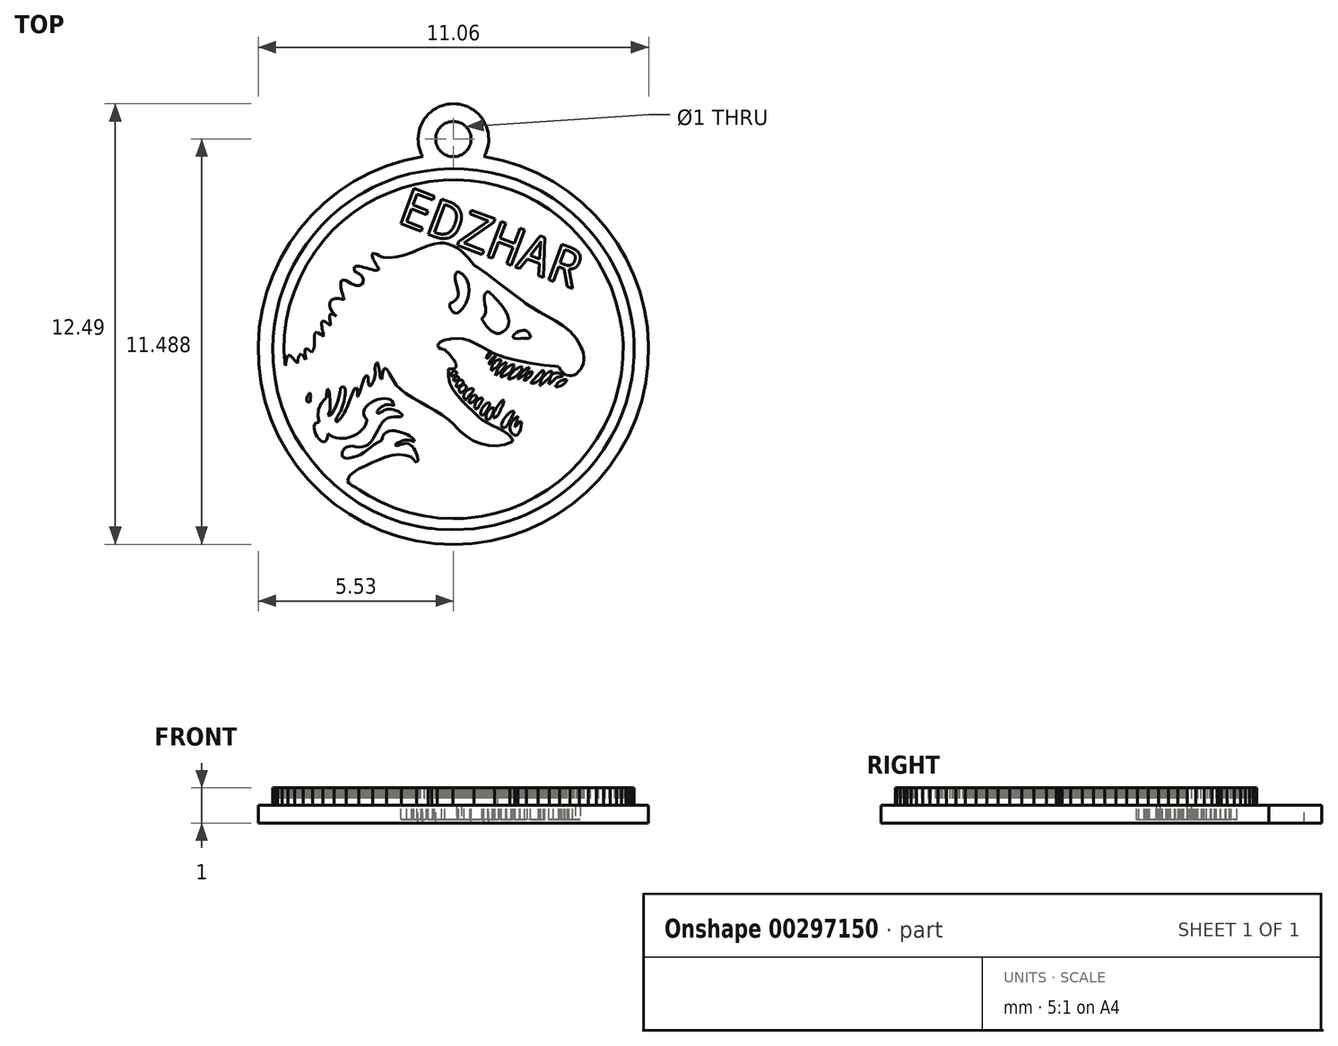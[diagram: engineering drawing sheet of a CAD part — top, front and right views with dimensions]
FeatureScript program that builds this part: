
annotation { "Feature Type Name" : "Feature", "Feature Type Description" : "" }
export const myFeature = defineFeature(function(context is Context, id is Id, definition is map)
    precondition{}
    {
        {
            var Q0;
            Q0=qCreatedBy(makeId("Top.planeOp"),FACE);
            var sketch = newSketch(context, id + "F0", { "sketchPlane" : qUnion([Q0])});
            skLineSegment(sketch, "E0", {"start": v(-0.6, -5.08) * mm, "end": v(-0.71, -5.07) * mm});
            skLineSegment(sketch, "E1", {"start": v(-0.71, -5.07) * mm, "end": v(-1.04, -5.02) * mm});
            skLineSegment(sketch, "E2", {"start": v(-1.04, -5.02) * mm, "end": v(-1.47, -4.9) * mm});
            skLineSegment(sketch, "E3", {"start": v(-1.47, -4.9) * mm, "end": v(-1.9, -4.76) * mm});
            skLineSegment(sketch, "E4", {"start": v(-1.9, -4.76) * mm, "end": v(-2.3, -4.58) * mm});
            skLineSegment(sketch, "E5", {"start": v(-2.3, -4.58) * mm, "end": v(-2.68, -4.36) * mm});
            skLineSegment(sketch, "E6", {"start": v(-2.68, -4.36) * mm, "end": v(-3.04, -4.11) * mm});
            skLineSegment(sketch, "E7", {"start": v(-3.04, -4.11) * mm, "end": v(-3.38, -3.83) * mm});
            skLineSegment(sketch, "E8", {"start": v(-3.38, -3.83) * mm, "end": v(-3.7, -3.52) * mm});
            skLineSegment(sketch, "E9", {"start": v(-3.7, -3.52) * mm, "end": v(-4, -3.2) * mm});
            skLineSegment(sketch, "E10", {"start": v(-4, -3.2) * mm, "end": v(-4.26, -2.84) * mm});
            skLineSegment(sketch, "E11", {"start": v(-4.26, -2.84) * mm, "end": v(-4.49, -2.46) * mm});
            skLineSegment(sketch, "E12", {"start": v(-4.49, -2.46) * mm, "end": v(-4.69, -2.06) * mm});
            skLineSegment(sketch, "E13", {"start": v(-4.69, -2.06) * mm, "end": v(-4.85, -1.65) * mm});
            skLineSegment(sketch, "E14", {"start": v(-4.85, -1.65) * mm, "end": v(-4.98, -1.23) * mm});
            skLineSegment(sketch, "E15", {"start": v(-4.98, -1.23) * mm, "end": v(-5.06, -0.8) * mm});
            skLineSegment(sketch, "E16", {"start": v(-5.06, -0.8) * mm, "end": v(-5.1, -0.46) * mm});
            skLineSegment(sketch, "E17", {"start": v(-5.1, -0.46) * mm, "end": v(-5.1, -0.35) * mm});
            skLineSegment(sketch, "E18", {"start": v(-5.1, -0.35) * mm, "end": v(-5.11, -0.26) * mm});
            skLineSegment(sketch, "E19", {"start": v(-5.11, -0.26) * mm, "end": v(-5.12, 0) * mm});
            skLineSegment(sketch, "E20", {"start": v(-5.12, 0) * mm, "end": v(-5.1, 0.36) * mm});
            skLineSegment(sketch, "E21", {"start": v(-5.1, 0.36) * mm, "end": v(-5.07, 0.7) * mm});
            skLineSegment(sketch, "E22", {"start": v(-5.07, 0.7) * mm, "end": v(-5, 1.05) * mm});
            skLineSegment(sketch, "E23", {"start": v(-5, 1.05) * mm, "end": v(-4.92, 1.4) * mm});
            skLineSegment(sketch, "E24", {"start": v(-4.92, 1.4) * mm, "end": v(-4.82, 1.73) * mm});
            skLineSegment(sketch, "E25", {"start": v(-4.82, 1.73) * mm, "end": v(-4.69, 2.06) * mm});
            skLineSegment(sketch, "E26", {"start": v(-4.69, 2.06) * mm, "end": v(-4.53, 2.38) * mm});
            skLineSegment(sketch, "E27", {"start": v(-4.53, 2.38) * mm, "end": v(-4.36, 2.68) * mm});
            skLineSegment(sketch, "E28", {"start": v(-4.36, 2.68) * mm, "end": v(-4.17, 2.98) * mm});
            skLineSegment(sketch, "E29", {"start": v(-4.17, 2.98) * mm, "end": v(-3.95, 3.26) * mm});
            skLineSegment(sketch, "E30", {"start": v(-3.95, 3.26) * mm, "end": v(-3.72, 3.52) * mm});
            skLineSegment(sketch, "E31", {"start": v(-3.72, 3.52) * mm, "end": v(-3.47, 3.77) * mm});
            skLineSegment(sketch, "E32", {"start": v(-3.47, 3.77) * mm, "end": v(-3.2, 4) * mm});
            skLineSegment(sketch, "E33", {"start": v(-3.2, 4) * mm, "end": v(-2.92, 4.21) * mm});
            skLineSegment(sketch, "E34", {"start": v(-2.92, 4.21) * mm, "end": v(-2.7, 4.36) * mm});
            skLineSegment(sketch, "E35", {"start": v(-2.7, 4.36) * mm, "end": v(-2.62, 4.4) * mm});
            skLineSegment(sketch, "E36", {"start": v(-2.62, 4.4) * mm, "end": v(-2.53, 4.45) * mm});
            skLineSegment(sketch, "E37", {"start": v(-2.53, 4.45) * mm, "end": v(-2.28, 4.59) * mm});
            skLineSegment(sketch, "E38", {"start": v(-2.28, 4.59) * mm, "end": v(-1.93, 4.74) * mm});
            skLineSegment(sketch, "E39", {"start": v(-1.93, 4.74) * mm, "end": v(-1.57, 4.87) * mm});
            skLineSegment(sketch, "E40", {"start": v(-1.57, 4.87) * mm, "end": v(-1.2, 4.98) * mm});
            skLineSegment(sketch, "E41", {"start": v(-1.2, 4.98) * mm, "end": v(-0.83, 5.05) * mm});
            skLineSegment(sketch, "E42", {"start": v(-0.83, 5.05) * mm, "end": v(-0.45, 5.1) * mm});
            skLineSegment(sketch, "E43", {"start": v(-0.45, 5.1) * mm, "end": v(-0.07, 5.12) * mm});
            skLineSegment(sketch, "E44", {"start": v(-0.07, 5.12) * mm, "end": v(0.3, 5.1) * mm});
            skLineSegment(sketch, "E45", {"start": v(0.3, 5.1) * mm, "end": v(0.69, 5.07) * mm});
            skLineSegment(sketch, "E46", {"start": v(0.69, 5.07) * mm, "end": v(1.06, 5.01) * mm});
            skLineSegment(sketch, "E47", {"start": v(1.06, 5.01) * mm, "end": v(1.43, 4.92) * mm});
            skLineSegment(sketch, "E48", {"start": v(1.43, 4.92) * mm, "end": v(1.8, 4.8) * mm});
            skLineSegment(sketch, "E49", {"start": v(1.8, 4.8) * mm, "end": v(2.15, 4.66) * mm});
            skLineSegment(sketch, "E50", {"start": v(2.15, 4.66) * mm, "end": v(2.49, 4.48) * mm});
            skLineSegment(sketch, "E51", {"start": v(2.49, 4.48) * mm, "end": v(2.81, 4.28) * mm});
            skLineSegment(sketch, "E52", {"start": v(2.81, 4.28) * mm, "end": v(3.05, 4.11) * mm});
            skLineSegment(sketch, "E53", {"start": v(3.05, 4.11) * mm, "end": v(3.12, 4.05) * mm});
            skLineSegment(sketch, "E54", {"start": v(3.12, 4.05) * mm, "end": v(3.19, 4) * mm});
            skLineSegment(sketch, "E55", {"start": v(3.19, 4) * mm, "end": v(3.37, 3.85) * mm});
            skLineSegment(sketch, "E56", {"start": v(3.37, 3.85) * mm, "end": v(3.61, 3.63) * mm});
            skLineSegment(sketch, "E57", {"start": v(3.61, 3.63) * mm, "end": v(3.83, 3.4) * mm});
            skLineSegment(sketch, "E58", {"start": v(3.83, 3.4) * mm, "end": v(4.04, 3.15) * mm});
            skLineSegment(sketch, "E59", {"start": v(4.04, 3.15) * mm, "end": v(4.23, 2.89) * mm});
            skLineSegment(sketch, "E60", {"start": v(4.23, 2.89) * mm, "end": v(4.4, 2.62) * mm});
            skLineSegment(sketch, "E61", {"start": v(4.4, 2.62) * mm, "end": v(4.56, 2.33) * mm});
            skLineSegment(sketch, "E62", {"start": v(4.56, 2.33) * mm, "end": v(4.7, 2.04) * mm});
            skLineSegment(sketch, "E63", {"start": v(4.7, 2.04) * mm, "end": v(4.81, 1.75) * mm});
            skLineSegment(sketch, "E64", {"start": v(4.81, 1.75) * mm, "end": v(4.91, 1.44) * mm});
            skLineSegment(sketch, "E65", {"start": v(4.91, 1.44) * mm, "end": v(5, 1.13) * mm});
            skLineSegment(sketch, "E66", {"start": v(5, 1.13) * mm, "end": v(5.06, 0.81) * mm});
            skLineSegment(sketch, "E67", {"start": v(5.06, 0.81) * mm, "end": v(5.1, 0.5) * mm});
            skLineSegment(sketch, "E68", {"start": v(5.1, 0.5) * mm, "end": v(5.12, 0.17) * mm});
            skLineSegment(sketch, "E69", {"start": v(5.12, 0.17) * mm, "end": v(5.12, -0.15) * mm});
            skLineSegment(sketch, "E70", {"start": v(5.12, -0.15) * mm, "end": v(5.1, -0.4) * mm});
            skLineSegment(sketch, "E71", {"start": v(5.1, -0.4) * mm, "end": v(5.1, -0.47) * mm});
            skLineSegment(sketch, "E72", {"start": v(5.1, -0.47) * mm, "end": v(5.09, -0.56) * mm});
            skLineSegment(sketch, "E73", {"start": v(5.09, -0.56) * mm, "end": v(5.05, -0.83) * mm});
            skLineSegment(sketch, "E74", {"start": v(5.05, -0.83) * mm, "end": v(4.98, -1.2) * mm});
            skLineSegment(sketch, "E75", {"start": v(4.98, -1.2) * mm, "end": v(4.89, -1.54) * mm});
            skLineSegment(sketch, "E76", {"start": v(4.89, -1.54) * mm, "end": v(4.76, -1.88) * mm});
            skLineSegment(sketch, "E77", {"start": v(4.76, -1.88) * mm, "end": v(4.62, -2.21) * mm});
            skLineSegment(sketch, "E78", {"start": v(4.62, -2.21) * mm, "end": v(4.45, -2.53) * mm});
            skLineSegment(sketch, "E79", {"start": v(4.45, -2.53) * mm, "end": v(4.26, -2.84) * mm});
            skLineSegment(sketch, "E80", {"start": v(4.26, -2.84) * mm, "end": v(4.05, -3.13) * mm});
            skLineSegment(sketch, "E81", {"start": v(4.05, -3.13) * mm, "end": v(3.82, -3.4) * mm});
            skLineSegment(sketch, "E82", {"start": v(3.82, -3.4) * mm, "end": v(3.57, -3.67) * mm});
            skLineSegment(sketch, "E83", {"start": v(3.57, -3.67) * mm, "end": v(3.3, -3.91) * mm});
            skLineSegment(sketch, "E84", {"start": v(3.3, -3.91) * mm, "end": v(3.02, -4.14) * mm});
            skLineSegment(sketch, "E85", {"start": v(3.02, -4.14) * mm, "end": v(2.72, -4.34) * mm});
            skLineSegment(sketch, "E86", {"start": v(2.72, -4.34) * mm, "end": v(2.4, -4.52) * mm});
            skLineSegment(sketch, "E87", {"start": v(2.4, -4.52) * mm, "end": v(2.08, -4.68) * mm});
            skLineSegment(sketch, "E88", {"start": v(2.08, -4.68) * mm, "end": v(1.82, -4.78) * mm});
            skLineSegment(sketch, "E89", {"start": v(1.82, -4.78) * mm, "end": v(1.74, -4.81) * mm});
            skLineSegment(sketch, "E90", {"start": v(1.74, -4.81) * mm, "end": v(1.6, -4.86) * mm});
            skLineSegment(sketch, "E91", {"start": v(1.6, -4.86) * mm, "end": v(1.17, -4.98) * mm});
            skLineSegment(sketch, "E92", {"start": v(1.17, -4.98) * mm, "end": v(0.58, -5.08) * mm});
            skLineSegment(sketch, "E93", {"start": v(0.58, -5.08) * mm, "end": v(-0.01, -5.12) * mm});
            skLineSegment(sketch, "E94", {"start": v(-0.01, -5.12) * mm, "end": v(-0.46, -5.1) * mm});
            skLineSegment(sketch, "E95", {"start": v(-0.46, -5.1) * mm, "end": v(-0.6, -5.08) * mm});
            skLineSegment(sketch, "E96", {"start": v(0.4, -4.78) * mm, "end": v(0.5, -4.78) * mm});
            skLineSegment(sketch, "E97", {"start": v(0.5, -4.78) * mm, "end": v(0.81, -4.74) * mm});
            skLineSegment(sketch, "E98", {"start": v(0.81, -4.74) * mm, "end": v(1.2, -4.65) * mm});
            skLineSegment(sketch, "E99", {"start": v(1.2, -4.65) * mm, "end": v(1.6, -4.53) * mm});
            skLineSegment(sketch, "E100", {"start": v(1.6, -4.53) * mm, "end": v(1.97, -4.38) * mm});
            skLineSegment(sketch, "E101", {"start": v(1.97, -4.38) * mm, "end": v(2.33, -4.2) * mm});
            skLineSegment(sketch, "E102", {"start": v(2.33, -4.2) * mm, "end": v(2.67, -3.98) * mm});
            skLineSegment(sketch, "E103", {"start": v(2.67, -3.98) * mm, "end": v(3, -3.74) * mm});
            skLineSegment(sketch, "E104", {"start": v(3, -3.74) * mm, "end": v(3.3, -3.47) * mm});
            skLineSegment(sketch, "E105", {"start": v(3.3, -3.47) * mm, "end": v(3.58, -3.18) * mm});
            skLineSegment(sketch, "E106", {"start": v(3.58, -3.18) * mm, "end": v(3.84, -2.87) * mm});
            skLineSegment(sketch, "E107", {"start": v(3.84, -2.87) * mm, "end": v(4.07, -2.54) * mm});
            skLineSegment(sketch, "E108", {"start": v(4.07, -2.54) * mm, "end": v(4.27, -2.19) * mm});
            skLineSegment(sketch, "E109", {"start": v(4.27, -2.19) * mm, "end": v(4.44, -1.82) * mm});
            skLineSegment(sketch, "E110", {"start": v(4.44, -1.82) * mm, "end": v(4.59, -1.45) * mm});
            skLineSegment(sketch, "E111", {"start": v(4.59, -1.45) * mm, "end": v(4.7, -1.06) * mm});
            skLineSegment(sketch, "E112", {"start": v(4.7, -1.06) * mm, "end": v(4.75, -0.76) * mm});
            skLineSegment(sketch, "E113", {"start": v(4.75, -0.76) * mm, "end": v(4.76, -0.65) * mm});
            skLineSegment(sketch, "E114", {"start": v(4.76, -0.65) * mm, "end": v(4.78, -0.55) * mm});
            skLineSegment(sketch, "E115", {"start": v(4.78, -0.55) * mm, "end": v(4.8, -0.25) * mm});
            skLineSegment(sketch, "E116", {"start": v(4.8, -0.25) * mm, "end": v(4.8, 0.16) * mm});
            skLineSegment(sketch, "E117", {"start": v(4.8, 0.16) * mm, "end": v(4.77, 0.57) * mm});
            skLineSegment(sketch, "E118", {"start": v(4.77, 0.57) * mm, "end": v(4.7, 0.97) * mm});
            skLineSegment(sketch, "E119", {"start": v(4.7, 0.97) * mm, "end": v(4.6, 1.36) * mm});
            skLineSegment(sketch, "E120", {"start": v(4.6, 1.36) * mm, "end": v(4.46, 1.75) * mm});
            skLineSegment(sketch, "E121", {"start": v(4.46, 1.75) * mm, "end": v(4.3, 2.12) * mm});
            skLineSegment(sketch, "E122", {"start": v(4.3, 2.12) * mm, "end": v(4.1, 2.48) * mm});
            skLineSegment(sketch, "E123", {"start": v(4.1, 2.48) * mm, "end": v(3.87, 2.82) * mm});
            skLineSegment(sketch, "E124", {"start": v(3.87, 2.82) * mm, "end": v(3.62, 3.14) * mm});
            skLineSegment(sketch, "E125", {"start": v(3.62, 3.14) * mm, "end": v(3.34, 3.44) * mm});
            skLineSegment(sketch, "E126", {"start": v(3.34, 3.44) * mm, "end": v(3.04, 3.71) * mm});
            skLineSegment(sketch, "E127", {"start": v(3.04, 3.71) * mm, "end": v(2.72, 3.96) * mm});
            skLineSegment(sketch, "E128", {"start": v(2.72, 3.96) * mm, "end": v(2.37, 4.18) * mm});
            skLineSegment(sketch, "E129", {"start": v(2.37, 4.18) * mm, "end": v(2, 4.37) * mm});
            skLineSegment(sketch, "E130", {"start": v(2, 4.37) * mm, "end": v(1.73, 4.49) * mm});
            skLineSegment(sketch, "E131", {"start": v(1.73, 4.49) * mm, "end": v(1.63, 4.52) * mm});
            skLineSegment(sketch, "E132", {"start": v(1.63, 4.52) * mm, "end": v(1.54, 4.55) * mm});
            skLineSegment(sketch, "E133", {"start": v(1.54, 4.55) * mm, "end": v(1.25, 4.64) * mm});
            skLineSegment(sketch, "E134", {"start": v(1.25, 4.64) * mm, "end": v(0.87, 4.73) * mm});
            skLineSegment(sketch, "E135", {"start": v(0.87, 4.73) * mm, "end": v(0.49, 4.78) * mm});
            skLineSegment(sketch, "E136", {"start": v(0.49, 4.78) * mm, "end": v(0.1, 4.8) * mm});
            skLineSegment(sketch, "E137", {"start": v(0.1, 4.8) * mm, "end": v(-0.3, 4.8) * mm});
            skLineSegment(sketch, "E138", {"start": v(-0.3, 4.8) * mm, "end": v(-0.68, 4.75) * mm});
            skLineSegment(sketch, "E139", {"start": v(-0.68, 4.75) * mm, "end": v(-1.07, 4.68) * mm});
            skLineSegment(sketch, "E140", {"start": v(-1.07, 4.68) * mm, "end": v(-1.45, 4.57) * mm});
            skLineSegment(sketch, "E141", {"start": v(-1.45, 4.57) * mm, "end": v(-1.81, 4.44) * mm});
            skLineSegment(sketch, "E142", {"start": v(-1.81, 4.44) * mm, "end": v(-2.17, 4.28) * mm});
            skLineSegment(sketch, "E143", {"start": v(-2.17, 4.28) * mm, "end": v(-2.51, 4.1) * mm});
            skLineSegment(sketch, "E144", {"start": v(-2.51, 4.1) * mm, "end": v(-2.84, 3.87) * mm});
            skLineSegment(sketch, "E145", {"start": v(-2.84, 3.87) * mm, "end": v(-3.14, 3.63) * mm});
            skLineSegment(sketch, "E146", {"start": v(-3.14, 3.63) * mm, "end": v(-3.43, 3.36) * mm});
            skLineSegment(sketch, "E147", {"start": v(-3.43, 3.36) * mm, "end": v(-3.69, 3.07) * mm});
            skLineSegment(sketch, "E148", {"start": v(-3.69, 3.07) * mm, "end": v(-3.87, 2.84) * mm});
            skLineSegment(sketch, "E149", {"start": v(-3.87, 2.84) * mm, "end": v(-3.92, 2.75) * mm});
            skLineSegment(sketch, "E150", {"start": v(-3.92, 2.75) * mm, "end": v(-3.98, 2.67) * mm});
            skLineSegment(sketch, "E151", {"start": v(-3.98, 2.67) * mm, "end": v(-4.15, 2.4) * mm});
            skLineSegment(sketch, "E152", {"start": v(-4.15, 2.4) * mm, "end": v(-4.35, 2.02) * mm});
            skLineSegment(sketch, "E153", {"start": v(-4.35, 2.02) * mm, "end": v(-4.51, 1.63) * mm});
            skLineSegment(sketch, "E154", {"start": v(-4.51, 1.63) * mm, "end": v(-4.64, 1.22) * mm});
            skLineSegment(sketch, "E155", {"start": v(-4.64, 1.22) * mm, "end": v(-4.74, 0.8) * mm});
            skLineSegment(sketch, "E156", {"start": v(-4.74, 0.8) * mm, "end": v(-4.79, 0.39) * mm});
            skLineSegment(sketch, "E157", {"start": v(-4.79, 0.39) * mm, "end": v(-4.8, -0.04) * mm});
            skLineSegment(sketch, "E158", {"start": v(-4.8, -0.04) * mm, "end": v(-4.77, -0.36) * mm});
            skLineSegment(sketch, "E159", {"start": v(-4.77, -0.36) * mm, "end": v(-4.76, -0.46) * mm});
            skLineSegment(sketch, "E160", {"start": v(-4.76, -0.46) * mm, "end": v(-4.75, -0.42) * mm});
            skLineSegment(sketch, "E161", {"start": v(-4.75, -0.42) * mm, "end": v(-4.74, -0.31) * mm});
            skLineSegment(sketch, "E162", {"start": v(-4.74, -0.31) * mm, "end": v(-4.71, -0.22) * mm});
            skLineSegment(sketch, "E163", {"start": v(-4.71, -0.22) * mm, "end": v(-4.68, -0.18) * mm});
            skLineSegment(sketch, "E164", {"start": v(-4.68, -0.18) * mm, "end": v(-4.64, -0.17) * mm});
            skLineSegment(sketch, "E165", {"start": v(-4.64, -0.17) * mm, "end": v(-4.6, -0.2) * mm});
            skLineSegment(sketch, "E166", {"start": v(-4.6, -0.2) * mm, "end": v(-4.55, -0.25) * mm});
            skLineSegment(sketch, "E167", {"start": v(-4.55, -0.25) * mm, "end": v(-4.49, -0.32) * mm});
            skLineSegment(sketch, "E168", {"start": v(-4.49, -0.32) * mm, "end": v(-4.44, -0.38) * mm});
            skLineSegment(sketch, "E169", {"start": v(-4.44, -0.38) * mm, "end": v(-4.42, -0.4) * mm});
            skLineSegment(sketch, "E170", {"start": v(-4.42, -0.4) * mm, "end": v(-4.42, -0.38) * mm});
            skLineSegment(sketch, "E171", {"start": v(-4.42, -0.38) * mm, "end": v(-4.4, -0.31) * mm});
            skLineSegment(sketch, "E172", {"start": v(-4.4, -0.31) * mm, "end": v(-4.39, -0.24) * mm});
            skLineSegment(sketch, "E173", {"start": v(-4.39, -0.24) * mm, "end": v(-4.37, -0.18) * mm});
            skLineSegment(sketch, "E174", {"start": v(-4.37, -0.18) * mm, "end": v(-4.35, -0.15) * mm});
            skLineSegment(sketch, "E175", {"start": v(-4.35, -0.15) * mm, "end": v(-4.32, -0.14) * mm});
            skLineSegment(sketch, "E176", {"start": v(-4.32, -0.14) * mm, "end": v(-4.28, -0.16) * mm});
            skLineSegment(sketch, "E177", {"start": v(-4.28, -0.16) * mm, "end": v(-4.23, -0.21) * mm});
            skLineSegment(sketch, "E178", {"start": v(-4.23, -0.21) * mm, "end": v(-4.19, -0.27) * mm});
            skLineSegment(sketch, "E179", {"start": v(-4.19, -0.27) * mm, "end": v(-4.17, -0.3) * mm});
            skLineSegment(sketch, "E180", {"start": v(-4.17, -0.3) * mm, "end": v(-4.18, -0.29) * mm});
            skLineSegment(sketch, "E181", {"start": v(-4.18, -0.29) * mm, "end": v(-4.18, -0.26) * mm});
            skLineSegment(sketch, "E182", {"start": v(-4.18, -0.26) * mm, "end": v(-4.19, -0.22) * mm});
            skLineSegment(sketch, "E183", {"start": v(-4.19, -0.22) * mm, "end": v(-4.2, -0.19) * mm});
            skLineSegment(sketch, "E184", {"start": v(-4.2, -0.19) * mm, "end": v(-4.2, -0.15) * mm});
            skLineSegment(sketch, "E185", {"start": v(-4.2, -0.15) * mm, "end": v(-4.2, -0.11) * mm});
            skLineSegment(sketch, "E186", {"start": v(-4.2, -0.11) * mm, "end": v(-4.2, -0.08) * mm});
            skLineSegment(sketch, "E187", {"start": v(-4.2, -0.08) * mm, "end": v(-4.2, -0.05) * mm});
            skLineSegment(sketch, "E188", {"start": v(-4.2, -0.05) * mm, "end": v(-4.2, -0.03) * mm});
            skLineSegment(sketch, "E189", {"start": v(-4.2, -0.03) * mm, "end": v(-4.2, 0) * mm});
            skLineSegment(sketch, "E190", {"start": v(-4.2, 0) * mm, "end": v(-4.2, 0) * mm});
            skLineSegment(sketch, "E191", {"start": v(-4.2, 0) * mm, "end": v(-4.18, 0.01) * mm});
            skLineSegment(sketch, "E192", {"start": v(-4.18, 0.01) * mm, "end": v(-4.16, 0.01) * mm});
            skLineSegment(sketch, "E193", {"start": v(-4.16, 0.01) * mm, "end": v(-4.14, 0) * mm});
            skLineSegment(sketch, "E194", {"start": v(-4.14, 0) * mm, "end": v(-4.1, -0.02) * mm});
            skLineSegment(sketch, "E195", {"start": v(-4.1, -0.02) * mm, "end": v(-4.06, -0.04) * mm});
            skLineSegment(sketch, "E196", {"start": v(-4.06, -0.04) * mm, "end": v(-4.03, -0.07) * mm});
            skLineSegment(sketch, "E197", {"start": v(-4.03, -0.07) * mm, "end": v(-4.02, -0.08) * mm});
            skLineSegment(sketch, "E198", {"start": v(-4.02, -0.08) * mm, "end": v(-4, -0.08) * mm});
            skLineSegment(sketch, "E199", {"start": v(-4, -0.08) * mm, "end": v(-3.98, -0.05) * mm});
            skLineSegment(sketch, "E200", {"start": v(-3.98, -0.05) * mm, "end": v(-3.96, -0.01) * mm});
            skLineSegment(sketch, "E201", {"start": v(-3.96, -0.01) * mm, "end": v(-3.94, 0.04) * mm});
            skLineSegment(sketch, "E202", {"start": v(-3.94, 0.04) * mm, "end": v(-3.94, 0.1) * mm});
            skLineSegment(sketch, "E203", {"start": v(-3.94, 0.1) * mm, "end": v(-3.94, 0.15) * mm});
            skLineSegment(sketch, "E204", {"start": v(-3.94, 0.15) * mm, "end": v(-3.94, 0.22) * mm});
            skLineSegment(sketch, "E205", {"start": v(-3.94, 0.22) * mm, "end": v(-3.94, 0.28) * mm});
            skLineSegment(sketch, "E206", {"start": v(-3.94, 0.28) * mm, "end": v(-3.94, 0.33) * mm});
            skLineSegment(sketch, "E207", {"start": v(-3.94, 0.33) * mm, "end": v(-3.94, 0.39) * mm});
            skLineSegment(sketch, "E208", {"start": v(-3.94, 0.39) * mm, "end": v(-3.93, 0.43) * mm});
            skLineSegment(sketch, "E209", {"start": v(-3.93, 0.43) * mm, "end": v(-3.92, 0.46) * mm});
            skLineSegment(sketch, "E210", {"start": v(-3.92, 0.46) * mm, "end": v(-3.9, 0.48) * mm});
            skLineSegment(sketch, "E211", {"start": v(-3.9, 0.48) * mm, "end": v(-3.86, 0.48) * mm});
            skLineSegment(sketch, "E212", {"start": v(-3.86, 0.48) * mm, "end": v(-3.82, 0.46) * mm});
            skLineSegment(sketch, "E213", {"start": v(-3.82, 0.46) * mm, "end": v(-3.76, 0.42) * mm});
            skLineSegment(sketch, "E214", {"start": v(-3.76, 0.42) * mm, "end": v(-3.7, 0.37) * mm});
            skLineSegment(sketch, "E215", {"start": v(-3.7, 0.37) * mm, "end": v(-3.68, 0.36) * mm});
            skLineSegment(sketch, "E216", {"start": v(-3.68, 0.36) * mm, "end": v(-3.68, 0.37) * mm});
            skLineSegment(sketch, "E217", {"start": v(-3.68, 0.37) * mm, "end": v(-3.68, 0.4) * mm});
            skLineSegment(sketch, "E218", {"start": v(-3.68, 0.4) * mm, "end": v(-3.69, 0.44) * mm});
            skLineSegment(sketch, "E219", {"start": v(-3.69, 0.44) * mm, "end": v(-3.7, 0.5) * mm});
            skLineSegment(sketch, "E220", {"start": v(-3.7, 0.5) * mm, "end": v(-3.7, 0.54) * mm});
            skLineSegment(sketch, "E221", {"start": v(-3.7, 0.54) * mm, "end": v(-3.72, 0.59) * mm});
            skLineSegment(sketch, "E222", {"start": v(-3.72, 0.59) * mm, "end": v(-3.72, 0.64) * mm});
            skLineSegment(sketch, "E223", {"start": v(-3.72, 0.64) * mm, "end": v(-3.73, 0.68) * mm});
            skLineSegment(sketch, "E224", {"start": v(-3.73, 0.68) * mm, "end": v(-3.73, 0.72) * mm});
            skLineSegment(sketch, "E225", {"start": v(-3.73, 0.72) * mm, "end": v(-3.73, 0.75) * mm});
            skLineSegment(sketch, "E226", {"start": v(-3.73, 0.75) * mm, "end": v(-3.72, 0.78) * mm});
            skLineSegment(sketch, "E227", {"start": v(-3.72, 0.78) * mm, "end": v(-3.7, 0.8) * mm});
            skLineSegment(sketch, "E228", {"start": v(-3.7, 0.8) * mm, "end": v(-3.69, 0.8) * mm});
            skLineSegment(sketch, "E229", {"start": v(-3.69, 0.8) * mm, "end": v(-3.65, 0.8) * mm});
            skLineSegment(sketch, "E230", {"start": v(-3.65, 0.8) * mm, "end": v(-3.6, 0.77) * mm});
            skLineSegment(sketch, "E231", {"start": v(-3.6, 0.77) * mm, "end": v(-3.55, 0.73) * mm});
            skLineSegment(sketch, "E232", {"start": v(-3.55, 0.73) * mm, "end": v(-3.5, 0.7) * mm});
            skLineSegment(sketch, "E233", {"start": v(-3.5, 0.7) * mm, "end": v(-3.48, 0.68) * mm});
            skLineSegment(sketch, "E234", {"start": v(-3.48, 0.68) * mm, "end": v(-3.48, 0.69) * mm});
            skLineSegment(sketch, "E235", {"start": v(-3.48, 0.69) * mm, "end": v(-3.48, 0.73) * mm});
            skLineSegment(sketch, "E236", {"start": v(-3.48, 0.73) * mm, "end": v(-3.49, 0.8) * mm});
            skLineSegment(sketch, "E237", {"start": v(-3.49, 0.8) * mm, "end": v(-3.5, 0.87) * mm});
            skLineSegment(sketch, "E238", {"start": v(-3.5, 0.87) * mm, "end": v(-3.5, 0.93) * mm});
            skLineSegment(sketch, "E239", {"start": v(-3.5, 0.93) * mm, "end": v(-3.5, 0.98) * mm});
            skLineSegment(sketch, "E240", {"start": v(-3.5, 0.98) * mm, "end": v(-3.47, 1) * mm});
            skLineSegment(sketch, "E241", {"start": v(-3.47, 1) * mm, "end": v(-3.41, 1) * mm});
            skLineSegment(sketch, "E242", {"start": v(-3.41, 1) * mm, "end": v(-3.34, 0.95) * mm});
            skLineSegment(sketch, "E243", {"start": v(-3.34, 0.95) * mm, "end": v(-3.32, 0.94) * mm});
            skLineSegment(sketch, "E244", {"start": v(-3.32, 0.94) * mm, "end": v(-3.35, 0.97) * mm});
            skLineSegment(sketch, "E245", {"start": v(-3.35, 0.97) * mm, "end": v(-3.43, 1.06) * mm});
            skLineSegment(sketch, "E246", {"start": v(-3.43, 1.06) * mm, "end": v(-3.49, 1.17) * mm});
            skLineSegment(sketch, "E247", {"start": v(-3.49, 1.17) * mm, "end": v(-3.5, 1.26) * mm});
            skLineSegment(sketch, "E248", {"start": v(-3.5, 1.26) * mm, "end": v(-3.49, 1.34) * mm});
            skLineSegment(sketch, "E249", {"start": v(-3.49, 1.34) * mm, "end": v(-3.44, 1.4) * mm});
            skLineSegment(sketch, "E250", {"start": v(-3.44, 1.4) * mm, "end": v(-3.35, 1.43) * mm});
            skLineSegment(sketch, "E251", {"start": v(-3.35, 1.43) * mm, "end": v(-3.24, 1.43) * mm});
            skLineSegment(sketch, "E252", {"start": v(-3.24, 1.43) * mm, "end": v(-3.13, 1.41) * mm});
            skLineSegment(sketch, "E253", {"start": v(-3.13, 1.41) * mm, "end": v(-3.1, 1.4) * mm});
            skLineSegment(sketch, "E254", {"start": v(-3.1, 1.4) * mm, "end": v(-3.1, 1.41) * mm});
            skLineSegment(sketch, "E255", {"start": v(-3.1, 1.41) * mm, "end": v(-3.11, 1.45) * mm});
            skLineSegment(sketch, "E256", {"start": v(-3.11, 1.45) * mm, "end": v(-3.13, 1.51) * mm});
            skLineSegment(sketch, "E257", {"start": v(-3.13, 1.51) * mm, "end": v(-3.14, 1.57) * mm});
            skLineSegment(sketch, "E258", {"start": v(-3.14, 1.57) * mm, "end": v(-3.16, 1.63) * mm});
            skLineSegment(sketch, "E259", {"start": v(-3.16, 1.63) * mm, "end": v(-3.17, 1.7) * mm});
            skLineSegment(sketch, "E260", {"start": v(-3.17, 1.7) * mm, "end": v(-3.18, 1.75) * mm});
            skLineSegment(sketch, "E261", {"start": v(-3.18, 1.75) * mm, "end": v(-3.2, 1.8) * mm});
            skLineSegment(sketch, "E262", {"start": v(-3.2, 1.8) * mm, "end": v(-3.2, 1.85) * mm});
            skLineSegment(sketch, "E263", {"start": v(-3.2, 1.85) * mm, "end": v(-3.19, 1.9) * mm});
            skLineSegment(sketch, "E264", {"start": v(-3.19, 1.9) * mm, "end": v(-3.18, 1.93) * mm});
            skLineSegment(sketch, "E265", {"start": v(-3.18, 1.93) * mm, "end": v(-3.16, 1.95) * mm});
            skLineSegment(sketch, "E266", {"start": v(-3.16, 1.95) * mm, "end": v(-3.13, 1.96) * mm});
            skLineSegment(sketch, "E267", {"start": v(-3.13, 1.96) * mm, "end": v(-3.09, 1.96) * mm});
            skLineSegment(sketch, "E268", {"start": v(-3.09, 1.96) * mm, "end": v(-3.03, 1.94) * mm});
            skLineSegment(sketch, "E269", {"start": v(-3.03, 1.94) * mm, "end": v(-2.97, 1.91) * mm});
            skLineSegment(sketch, "E270", {"start": v(-2.97, 1.91) * mm, "end": v(-2.9, 1.87) * mm});
            skLineSegment(sketch, "E271", {"start": v(-2.9, 1.87) * mm, "end": v(-2.89, 1.86) * mm});
            skLineSegment(sketch, "E272", {"start": v(-2.89, 1.86) * mm, "end": v(-2.86, 1.84) * mm});
            skLineSegment(sketch, "E273", {"start": v(-2.86, 1.84) * mm, "end": v(-2.76, 1.8) * mm});
            skLineSegment(sketch, "E274", {"start": v(-2.76, 1.8) * mm, "end": v(-2.66, 1.8) * mm});
            skLineSegment(sketch, "E275", {"start": v(-2.66, 1.8) * mm, "end": v(-2.6, 1.84) * mm});
            skLineSegment(sketch, "E276", {"start": v(-2.6, 1.84) * mm, "end": v(-2.56, 1.9) * mm});
            skLineSegment(sketch, "E277", {"start": v(-2.56, 1.9) * mm, "end": v(-2.55, 1.98) * mm});
            skLineSegment(sketch, "E278", {"start": v(-2.55, 1.98) * mm, "end": v(-2.6, 2.07) * mm});
            skLineSegment(sketch, "E279", {"start": v(-2.6, 2.07) * mm, "end": v(-2.67, 2.14) * mm});
            skLineSegment(sketch, "E280", {"start": v(-2.67, 2.14) * mm, "end": v(-2.76, 2.18) * mm});
            skLineSegment(sketch, "E281", {"start": v(-2.76, 2.18) * mm, "end": v(-2.79, 2.2) * mm});
            skLineSegment(sketch, "E282", {"start": v(-2.79, 2.2) * mm, "end": v(-2.8, 2.2) * mm});
            skLineSegment(sketch, "E283", {"start": v(-2.8, 2.2) * mm, "end": v(-2.81, 2.26) * mm});
            skLineSegment(sketch, "E284", {"start": v(-2.81, 2.26) * mm, "end": v(-2.81, 2.3) * mm});
            skLineSegment(sketch, "E285", {"start": v(-2.81, 2.3) * mm, "end": v(-2.8, 2.34) * mm});
            skLineSegment(sketch, "E286", {"start": v(-2.8, 2.34) * mm, "end": v(-2.76, 2.35) * mm});
            skLineSegment(sketch, "E287", {"start": v(-2.76, 2.35) * mm, "end": v(-2.72, 2.36) * mm});
            skLineSegment(sketch, "E288", {"start": v(-2.72, 2.36) * mm, "end": v(-2.66, 2.35) * mm});
            skLineSegment(sketch, "E289", {"start": v(-2.66, 2.35) * mm, "end": v(-2.6, 2.34) * mm});
            skLineSegment(sketch, "E290", {"start": v(-2.6, 2.34) * mm, "end": v(-2.52, 2.32) * mm});
            skLineSegment(sketch, "E291", {"start": v(-2.52, 2.32) * mm, "end": v(-2.45, 2.3) * mm});
            skLineSegment(sketch, "E292", {"start": v(-2.45, 2.3) * mm, "end": v(-2.38, 2.28) * mm});
            skLineSegment(sketch, "E293", {"start": v(-2.38, 2.28) * mm, "end": v(-2.3, 2.26) * mm});
            skLineSegment(sketch, "E294", {"start": v(-2.3, 2.26) * mm, "end": v(-2.25, 2.24) * mm});
            skLineSegment(sketch, "E295", {"start": v(-2.25, 2.24) * mm, "end": v(-2.2, 2.24) * mm});
            skLineSegment(sketch, "E296", {"start": v(-2.2, 2.24) * mm, "end": v(-2.15, 2.24) * mm});
            skLineSegment(sketch, "E297", {"start": v(-2.15, 2.24) * mm, "end": v(-2.12, 2.26) * mm});
            skLineSegment(sketch, "E298", {"start": v(-2.12, 2.26) * mm, "end": v(-2.11, 2.28) * mm});
            skLineSegment(sketch, "E299", {"start": v(-2.11, 2.28) * mm, "end": v(-2.11, 2.29) * mm});
            skLineSegment(sketch, "E300", {"start": v(-2.11, 2.29) * mm, "end": v(-2.12, 2.3) * mm});
            skLineSegment(sketch, "E301", {"start": v(-2.12, 2.3) * mm, "end": v(-2.14, 2.33) * mm});
            skLineSegment(sketch, "E302", {"start": v(-2.14, 2.33) * mm, "end": v(-2.17, 2.37) * mm});
            skLineSegment(sketch, "E303", {"start": v(-2.17, 2.37) * mm, "end": v(-2.2, 2.42) * mm});
            skLineSegment(sketch, "E304", {"start": v(-2.2, 2.42) * mm, "end": v(-2.23, 2.47) * mm});
            skLineSegment(sketch, "E305", {"start": v(-2.23, 2.47) * mm, "end": v(-2.25, 2.51) * mm});
            skLineSegment(sketch, "E306", {"start": v(-2.25, 2.51) * mm, "end": v(-2.27, 2.56) * mm});
            skLineSegment(sketch, "E307", {"start": v(-2.27, 2.56) * mm, "end": v(-2.29, 2.6) * mm});
            skLineSegment(sketch, "E308", {"start": v(-2.29, 2.6) * mm, "end": v(-2.3, 2.64) * mm});
            skLineSegment(sketch, "E309", {"start": v(-2.3, 2.64) * mm, "end": v(-2.3, 2.67) * mm});
            skLineSegment(sketch, "E310", {"start": v(-2.3, 2.67) * mm, "end": v(-2.3, 2.7) * mm});
            skLineSegment(sketch, "E311", {"start": v(-2.3, 2.7) * mm, "end": v(-2.28, 2.7) * mm});
            skLineSegment(sketch, "E312", {"start": v(-2.28, 2.7) * mm, "end": v(-2.26, 2.72) * mm});
            skLineSegment(sketch, "E313", {"start": v(-2.26, 2.72) * mm, "end": v(-2.22, 2.71) * mm});
            skLineSegment(sketch, "E314", {"start": v(-2.22, 2.71) * mm, "end": v(-2.18, 2.7) * mm});
            skLineSegment(sketch, "E315", {"start": v(-2.18, 2.7) * mm, "end": v(-2.11, 2.66) * mm});
            skLineSegment(sketch, "E316", {"start": v(-2.11, 2.66) * mm, "end": v(-2.06, 2.63) * mm});
            skLineSegment(sketch, "E317", {"start": v(-2.06, 2.63) * mm, "end": v(-2.04, 2.61) * mm});
            skLineSegment(sketch, "E318", {"start": v(-2.04, 2.61) * mm, "end": v(-1.99, 2.6) * mm});
            skLineSegment(sketch, "E319", {"start": v(-1.99, 2.6) * mm, "end": v(-1.82, 2.59) * mm});
            skLineSegment(sketch, "E320", {"start": v(-1.82, 2.59) * mm, "end": v(-1.6, 2.61) * mm});
            skLineSegment(sketch, "E321", {"start": v(-1.6, 2.61) * mm, "end": v(-1.39, 2.67) * mm});
            skLineSegment(sketch, "E322", {"start": v(-1.39, 2.67) * mm, "end": v(-1.17, 2.75) * mm});
            skLineSegment(sketch, "E323", {"start": v(-1.17, 2.75) * mm, "end": v(-0.96, 2.84) * mm});
            skLineSegment(sketch, "E324", {"start": v(-0.96, 2.84) * mm, "end": v(-0.75, 2.92) * mm});
            skLineSegment(sketch, "E325", {"start": v(-0.75, 2.92) * mm, "end": v(-0.53, 2.99) * mm});
            skLineSegment(sketch, "E326", {"start": v(-0.53, 2.99) * mm, "end": v(-0.36, 3.02) * mm});
            skLineSegment(sketch, "E327", {"start": v(-0.36, 3.02) * mm, "end": v(-0.3, 3.02) * mm});
            skLineSegment(sketch, "E328", {"start": v(-0.3, 3.02) * mm, "end": v(-0.27, 3.01) * mm});
            skLineSegment(sketch, "E329", {"start": v(-0.27, 3.01) * mm, "end": v(-0.16, 2.99) * mm});
            skLineSegment(sketch, "E330", {"start": v(-0.16, 2.99) * mm, "end": v(-0.03, 2.94) * mm});
            skLineSegment(sketch, "E331", {"start": v(-0.03, 2.94) * mm, "end": v(0.1, 2.87) * mm});
            skLineSegment(sketch, "E332", {"start": v(0.1, 2.87) * mm, "end": v(0.2, 2.8) * mm});
            skLineSegment(sketch, "E333", {"start": v(0.2, 2.8) * mm, "end": v(0.32, 2.7) * mm});
            skLineSegment(sketch, "E334", {"start": v(0.32, 2.7) * mm, "end": v(0.42, 2.6) * mm});
            skLineSegment(sketch, "E335", {"start": v(0.42, 2.6) * mm, "end": v(0.51, 2.48) * mm});
            skLineSegment(sketch, "E336", {"start": v(0.51, 2.48) * mm, "end": v(0.58, 2.4) * mm});
            skLineSegment(sketch, "E337", {"start": v(0.58, 2.4) * mm, "end": v(0.6, 2.37) * mm});
            skLineSegment(sketch, "E338", {"start": v(0.6, 2.37) * mm, "end": v(0.7, 2.31) * mm});
            skLineSegment(sketch, "E339", {"start": v(0.7, 2.31) * mm, "end": v(0.95, 2.13) * mm});
            skLineSegment(sketch, "E340", {"start": v(0.95, 2.13) * mm, "end": v(1.3, 1.87) * mm});
            skLineSegment(sketch, "E341", {"start": v(1.3, 1.87) * mm, "end": v(1.65, 1.6) * mm});
            skLineSegment(sketch, "E342", {"start": v(1.65, 1.6) * mm, "end": v(1.9, 1.4) * mm});
            skLineSegment(sketch, "E343", {"start": v(1.9, 1.4) * mm, "end": v(2, 1.34) * mm});
            skLineSegment(sketch, "E344", {"start": v(2, 1.34) * mm, "end": v(2.05, 1.3) * mm});
            skLineSegment(sketch, "E345", {"start": v(2.05, 1.3) * mm, "end": v(2.2, 1.2) * mm});
            skLineSegment(sketch, "E346", {"start": v(2.2, 1.2) * mm, "end": v(2.43, 1.06) * mm});
            skLineSegment(sketch, "E347", {"start": v(2.43, 1.06) * mm, "end": v(2.66, 0.93) * mm});
            skLineSegment(sketch, "E348", {"start": v(2.66, 0.93) * mm, "end": v(2.9, 0.8) * mm});
            skLineSegment(sketch, "E349", {"start": v(2.9, 0.8) * mm, "end": v(3.11, 0.66) * mm});
            skLineSegment(sketch, "E350", {"start": v(3.11, 0.66) * mm, "end": v(3.31, 0.5) * mm});
            skLineSegment(sketch, "E351", {"start": v(3.31, 0.5) * mm, "end": v(3.48, 0.3) * mm});
            skLineSegment(sketch, "E352", {"start": v(3.48, 0.3) * mm, "end": v(3.58, 0.13) * mm});
            skLineSegment(sketch, "E353", {"start": v(3.58, 0.13) * mm, "end": v(3.6, 0.07) * mm});
            skLineSegment(sketch, "E354", {"start": v(3.6, 0.07) * mm, "end": v(3.62, 0.05) * mm});
            skLineSegment(sketch, "E355", {"start": v(3.62, 0.05) * mm, "end": v(3.66, -0.02) * mm});
            skLineSegment(sketch, "E356", {"start": v(3.66, -0.02) * mm, "end": v(3.69, -0.12) * mm});
            skLineSegment(sketch, "E357", {"start": v(3.69, -0.12) * mm, "end": v(3.7, -0.21) * mm});
            skLineSegment(sketch, "E358", {"start": v(3.7, -0.21) * mm, "end": v(3.7, -0.3) * mm});
            skLineSegment(sketch, "E359", {"start": v(3.7, -0.3) * mm, "end": v(3.68, -0.4) * mm});
            skLineSegment(sketch, "E360", {"start": v(3.68, -0.4) * mm, "end": v(3.64, -0.49) * mm});
            skLineSegment(sketch, "E361", {"start": v(3.64, -0.49) * mm, "end": v(3.6, -0.57) * mm});
            skLineSegment(sketch, "E362", {"start": v(3.6, -0.57) * mm, "end": v(3.55, -0.64) * mm});
            skLineSegment(sketch, "E363", {"start": v(3.55, -0.64) * mm, "end": v(3.49, -0.7) * mm});
            skLineSegment(sketch, "E364", {"start": v(3.49, -0.7) * mm, "end": v(3.42, -0.73) * mm});
            skLineSegment(sketch, "E365", {"start": v(3.42, -0.73) * mm, "end": v(3.35, -0.75) * mm});
            skLineSegment(sketch, "E366", {"start": v(3.35, -0.75) * mm, "end": v(3.27, -0.75) * mm});
            skLineSegment(sketch, "E367", {"start": v(3.27, -0.75) * mm, "end": v(3.2, -0.73) * mm});
            skLineSegment(sketch, "E368", {"start": v(3.2, -0.73) * mm, "end": v(3.12, -0.68) * mm});
            skLineSegment(sketch, "E369", {"start": v(3.12, -0.68) * mm, "end": v(3.05, -0.6) * mm});
            skLineSegment(sketch, "E370", {"start": v(3.05, -0.6) * mm, "end": v(3, -0.52) * mm});
            skLineSegment(sketch, "E371", {"start": v(3, -0.52) * mm, "end": v(2.98, -0.5) * mm});
            skLineSegment(sketch, "E372", {"start": v(2.98, -0.5) * mm, "end": v(2.88, -0.49) * mm});
            skLineSegment(sketch, "E373", {"start": v(2.88, -0.49) * mm, "end": v(2.58, -0.45) * mm});
            skLineSegment(sketch, "E374", {"start": v(2.58, -0.45) * mm, "end": v(2.16, -0.4) * mm});
            skLineSegment(sketch, "E375", {"start": v(2.16, -0.4) * mm, "end": v(1.75, -0.3) * mm});
            skLineSegment(sketch, "E376", {"start": v(1.75, -0.3) * mm, "end": v(1.44, -0.23) * mm});
            skLineSegment(sketch, "E377", {"start": v(1.44, -0.23) * mm, "end": v(1.34, -0.2) * mm});
            skLineSegment(sketch, "E378", {"start": v(1.34, -0.2) * mm, "end": v(1.3, -0.18) * mm});
            skLineSegment(sketch, "E379", {"start": v(1.3, -0.18) * mm, "end": v(1.16, -0.12) * mm});
            skLineSegment(sketch, "E380", {"start": v(1.16, -0.12) * mm, "end": v(0.98, -0.03) * mm});
            skLineSegment(sketch, "E381", {"start": v(0.98, -0.03) * mm, "end": v(0.81, 0.06) * mm});
            skLineSegment(sketch, "E382", {"start": v(0.81, 0.06) * mm, "end": v(0.64, 0.16) * mm});
            skLineSegment(sketch, "E383", {"start": v(0.64, 0.16) * mm, "end": v(0.46, 0.24) * mm});
            skLineSegment(sketch, "E384", {"start": v(0.46, 0.24) * mm, "end": v(0.28, 0.3) * mm});
            skLineSegment(sketch, "E385", {"start": v(0.28, 0.3) * mm, "end": v(0.08, 0.3) * mm});
            skLineSegment(sketch, "E386", {"start": v(0.08, 0.3) * mm, "end": v(-0.07, 0.29) * mm});
            skLineSegment(sketch, "E387", {"start": v(-0.07, 0.29) * mm, "end": v(-0.12, 0.27) * mm});
            skLineSegment(sketch, "E388", {"start": v(-0.12, 0.27) * mm, "end": v(-0.14, 0.28) * mm});
            skLineSegment(sketch, "E389", {"start": v(-0.14, 0.28) * mm, "end": v(-0.21, 0.27) * mm});
            skLineSegment(sketch, "E390", {"start": v(-0.21, 0.27) * mm, "end": v(-0.3, 0.25) * mm});
            skLineSegment(sketch, "E391", {"start": v(-0.3, 0.25) * mm, "end": v(-0.37, 0.2) * mm});
            skLineSegment(sketch, "E392", {"start": v(-0.37, 0.2) * mm, "end": v(-0.42, 0.16) * mm});
            skLineSegment(sketch, "E393", {"start": v(-0.42, 0.16) * mm, "end": v(-0.44, 0.1) * mm});
            skLineSegment(sketch, "E394", {"start": v(-0.44, 0.1) * mm, "end": v(-0.42, 0.06) * mm});
            skLineSegment(sketch, "E395", {"start": v(-0.42, 0.06) * mm, "end": v(-0.36, 0.01) * mm});
            skLineSegment(sketch, "E396", {"start": v(-0.36, 0.01) * mm, "end": v(-0.27, -0.01) * mm});
            skLineSegment(sketch, "E397", {"start": v(-0.27, -0.01) * mm, "end": v(-0.24, -0.02) * mm});
            skLineSegment(sketch, "E398", {"start": v(-0.24, -0.02) * mm, "end": v(-0.23, -0.03) * mm});
            skLineSegment(sketch, "E399", {"start": v(-0.23, -0.03) * mm, "end": v(-0.2, -0.05) * mm});
            skLineSegment(sketch, "E400", {"start": v(-0.2, -0.05) * mm, "end": v(-0.16, -0.1) * mm});
            skLineSegment(sketch, "E401", {"start": v(-0.16, -0.1) * mm, "end": v(-0.12, -0.14) * mm});
            skLineSegment(sketch, "E402", {"start": v(-0.12, -0.14) * mm, "end": v(-0.07, -0.19) * mm});
            skLineSegment(sketch, "E403", {"start": v(-0.07, -0.19) * mm, "end": v(-0.04, -0.24) * mm});
            skLineSegment(sketch, "E404", {"start": v(-0.04, -0.24) * mm, "end": v(0, -0.28) * mm});
            skLineSegment(sketch, "E405", {"start": v(0, -0.28) * mm, "end": v(0.03, -0.33) * mm});
            skLineSegment(sketch, "E406", {"start": v(0.03, -0.33) * mm, "end": v(0.06, -0.38) * mm});
            skLineSegment(sketch, "E407", {"start": v(0.06, -0.38) * mm, "end": v(0.07, -0.42) * mm});
            skLineSegment(sketch, "E408", {"start": v(0.07, -0.42) * mm, "end": v(0.08, -0.46) * mm});
            skLineSegment(sketch, "E409", {"start": v(0.08, -0.46) * mm, "end": v(0.08, -0.5) * mm});
            skLineSegment(sketch, "E410", {"start": v(0.08, -0.5) * mm, "end": v(0.06, -0.52) * mm});
            skLineSegment(sketch, "E411", {"start": v(0.06, -0.52) * mm, "end": v(0.04, -0.54) * mm});
            skLineSegment(sketch, "E412", {"start": v(0.04, -0.54) * mm, "end": v(0, -0.56) * mm});
            skLineSegment(sketch, "E413", {"start": v(0, -0.56) * mm, "end": v(-0.06, -0.56) * mm});
            skLineSegment(sketch, "E414", {"start": v(-0.06, -0.56) * mm, "end": v(-0.12, -0.56) * mm});
            skLineSegment(sketch, "E415", {"start": v(-0.12, -0.56) * mm, "end": v(-0.14, -0.56) * mm});
            skLineSegment(sketch, "E416", {"start": v(-0.14, -0.56) * mm, "end": v(-0.15, -0.6) * mm});
            skLineSegment(sketch, "E417", {"start": v(-0.15, -0.6) * mm, "end": v(-0.15, -0.76) * mm});
            skLineSegment(sketch, "E418", {"start": v(-0.15, -0.76) * mm, "end": v(-0.1, -0.96) * mm});
            skLineSegment(sketch, "E419", {"start": v(-0.1, -0.96) * mm, "end": v(-0.01, -1.14) * mm});
            skLineSegment(sketch, "E420", {"start": v(-0.01, -1.14) * mm, "end": v(0.1, -1.3) * mm});
            skLineSegment(sketch, "E421", {"start": v(0.1, -1.3) * mm, "end": v(0.25, -1.47) * mm});
            skLineSegment(sketch, "E422", {"start": v(0.25, -1.47) * mm, "end": v(0.4, -1.62) * mm});
            skLineSegment(sketch, "E423", {"start": v(0.4, -1.62) * mm, "end": v(0.55, -1.76) * mm});
            skLineSegment(sketch, "E424", {"start": v(0.55, -1.76) * mm, "end": v(0.66, -1.87) * mm});
            skLineSegment(sketch, "E425", {"start": v(0.66, -1.87) * mm, "end": v(0.7, -1.9) * mm});
            skLineSegment(sketch, "E426", {"start": v(0.7, -1.9) * mm, "end": v(0.72, -1.93) * mm});
            skLineSegment(sketch, "E427", {"start": v(0.72, -1.93) * mm, "end": v(0.81, -2) * mm});
            skLineSegment(sketch, "E428", {"start": v(0.81, -2) * mm, "end": v(0.96, -2.09) * mm});
            skLineSegment(sketch, "E429", {"start": v(0.96, -2.09) * mm, "end": v(1.12, -2.16) * mm});
            skLineSegment(sketch, "E430", {"start": v(1.12, -2.16) * mm, "end": v(1.28, -2.24) * mm});
            skLineSegment(sketch, "E431", {"start": v(1.28, -2.24) * mm, "end": v(1.43, -2.32) * mm});
            skLineSegment(sketch, "E432", {"start": v(1.43, -2.32) * mm, "end": v(1.55, -2.4) * mm});
            skLineSegment(sketch, "E433", {"start": v(1.55, -2.4) * mm, "end": v(1.64, -2.5) * mm});
            skLineSegment(sketch, "E434", {"start": v(1.64, -2.5) * mm, "end": v(1.67, -2.59) * mm});
            skLineSegment(sketch, "E435", {"start": v(1.67, -2.59) * mm, "end": v(1.67, -2.62) * mm});
            skLineSegment(sketch, "E436", {"start": v(1.67, -2.62) * mm, "end": v(1.62, -2.64) * mm});
            skLineSegment(sketch, "E437", {"start": v(1.62, -2.64) * mm, "end": v(1.46, -2.7) * mm});
            skLineSegment(sketch, "E438", {"start": v(1.46, -2.7) * mm, "end": v(1.23, -2.74) * mm});
            skLineSegment(sketch, "E439", {"start": v(1.23, -2.74) * mm, "end": v(1, -2.73) * mm});
            skLineSegment(sketch, "E440", {"start": v(1, -2.73) * mm, "end": v(0.79, -2.68) * mm});
            skLineSegment(sketch, "E441", {"start": v(0.79, -2.68) * mm, "end": v(0.57, -2.6) * mm});
            skLineSegment(sketch, "E442", {"start": v(0.57, -2.6) * mm, "end": v(0.38, -2.48) * mm});
            skLineSegment(sketch, "E443", {"start": v(0.38, -2.48) * mm, "end": v(0.2, -2.33) * mm});
            skLineSegment(sketch, "E444", {"start": v(0.2, -2.33) * mm, "end": v(0.08, -2.2) * mm});
            skLineSegment(sketch, "E445", {"start": v(0.08, -2.2) * mm, "end": v(0.04, -2.16) * mm});
            skLineSegment(sketch, "E446", {"start": v(0.04, -2.16) * mm, "end": v(0, -2.12) * mm});
            skLineSegment(sketch, "E447", {"start": v(0, -2.12) * mm, "end": v(-0.13, -2) * mm});
            skLineSegment(sketch, "E448", {"start": v(-0.13, -2) * mm, "end": v(-0.32, -1.86) * mm});
            skLineSegment(sketch, "E449", {"start": v(-0.32, -1.86) * mm, "end": v(-0.52, -1.74) * mm});
            skLineSegment(sketch, "E450", {"start": v(-0.52, -1.74) * mm, "end": v(-0.73, -1.62) * mm});
            skLineSegment(sketch, "E451", {"start": v(-0.73, -1.62) * mm, "end": v(-0.94, -1.5) * mm});
            skLineSegment(sketch, "E452", {"start": v(-0.94, -1.5) * mm, "end": v(-1.15, -1.38) * mm});
            skLineSegment(sketch, "E453", {"start": v(-1.15, -1.38) * mm, "end": v(-1.34, -1.25) * mm});
            skLineSegment(sketch, "E454", {"start": v(-1.34, -1.25) * mm, "end": v(-1.49, -1.14) * mm});
            skLineSegment(sketch, "E455", {"start": v(-1.49, -1.14) * mm, "end": v(-1.53, -1.1) * mm});
            skLineSegment(sketch, "E456", {"start": v(-1.53, -1.1) * mm, "end": v(-1.54, -1.1) * mm});
            skLineSegment(sketch, "E457", {"start": v(-1.54, -1.1) * mm, "end": v(-1.57, -1.07) * mm});
            skLineSegment(sketch, "E458", {"start": v(-1.57, -1.07) * mm, "end": v(-1.61, -1.02) * mm});
            skLineSegment(sketch, "E459", {"start": v(-1.61, -1.02) * mm, "end": v(-1.65, -0.97) * mm});
            skLineSegment(sketch, "E460", {"start": v(-1.65, -0.97) * mm, "end": v(-1.69, -0.9) * mm});
            skLineSegment(sketch, "E461", {"start": v(-1.69, -0.9) * mm, "end": v(-1.73, -0.84) * mm});
            skLineSegment(sketch, "E462", {"start": v(-1.73, -0.84) * mm, "end": v(-1.76, -0.77) * mm});
            skLineSegment(sketch, "E463", {"start": v(-1.76, -0.77) * mm, "end": v(-1.8, -0.7) * mm});
            skLineSegment(sketch, "E464", {"start": v(-1.8, -0.7) * mm, "end": v(-1.83, -0.65) * mm});
            skLineSegment(sketch, "E465", {"start": v(-1.83, -0.65) * mm, "end": v(-1.86, -0.6) * mm});
            skLineSegment(sketch, "E466", {"start": v(-1.86, -0.6) * mm, "end": v(-1.9, -0.56) * mm});
            skLineSegment(sketch, "E467", {"start": v(-1.9, -0.56) * mm, "end": v(-1.92, -0.55) * mm});
            skLineSegment(sketch, "E468", {"start": v(-1.92, -0.55) * mm, "end": v(-1.95, -0.55) * mm});
            skLineSegment(sketch, "E469", {"start": v(-1.95, -0.55) * mm, "end": v(-1.97, -0.57) * mm});
            skLineSegment(sketch, "E470", {"start": v(-1.97, -0.57) * mm, "end": v(-2, -0.62) * mm});
            skLineSegment(sketch, "E471", {"start": v(-2, -0.62) * mm, "end": v(-2, -0.7) * mm});
            skLineSegment(sketch, "E472", {"start": v(-2, -0.7) * mm, "end": v(-2.02, -0.79) * mm});
            skLineSegment(sketch, "E473", {"start": v(-2.02, -0.79) * mm, "end": v(-2.02, -0.82) * mm});
            skLineSegment(sketch, "E474", {"start": v(-2.02, -0.82) * mm, "end": v(-2.03, -0.82) * mm});
            skLineSegment(sketch, "E475", {"start": v(-2.03, -0.82) * mm, "end": v(-2.04, -0.84) * mm});
            skLineSegment(sketch, "E476", {"start": v(-2.04, -0.84) * mm, "end": v(-2.05, -0.84) * mm});
            skLineSegment(sketch, "E477", {"start": v(-2.05, -0.84) * mm, "end": v(-2.06, -0.82) * mm});
            skLineSegment(sketch, "E478", {"start": v(-2.06, -0.82) * mm, "end": v(-2.07, -0.79) * mm});
            skLineSegment(sketch, "E479", {"start": v(-2.07, -0.79) * mm, "end": v(-2.08, -0.73) * mm});
            skLineSegment(sketch, "E480", {"start": v(-2.08, -0.73) * mm, "end": v(-2.09, -0.67) * mm});
            skLineSegment(sketch, "E481", {"start": v(-2.09, -0.67) * mm, "end": v(-2.1, -0.61) * mm});
            skLineSegment(sketch, "E482", {"start": v(-2.1, -0.61) * mm, "end": v(-2.1, -0.55) * mm});
            skLineSegment(sketch, "E483", {"start": v(-2.1, -0.55) * mm, "end": v(-2.12, -0.49) * mm});
            skLineSegment(sketch, "E484", {"start": v(-2.12, -0.49) * mm, "end": v(-2.13, -0.44) * mm});
            skLineSegment(sketch, "E485", {"start": v(-2.13, -0.44) * mm, "end": v(-2.14, -0.4) * mm});
            skLineSegment(sketch, "E486", {"start": v(-2.14, -0.4) * mm, "end": v(-2.16, -0.38) * mm});
            skLineSegment(sketch, "E487", {"start": v(-2.16, -0.38) * mm, "end": v(-2.17, -0.38) * mm});
            skLineSegment(sketch, "E488", {"start": v(-2.17, -0.38) * mm, "end": v(-2.2, -0.4) * mm});
            skLineSegment(sketch, "E489", {"start": v(-2.2, -0.4) * mm, "end": v(-2.21, -0.46) * mm});
            skLineSegment(sketch, "E490", {"start": v(-2.21, -0.46) * mm, "end": v(-2.23, -0.53) * mm});
            skLineSegment(sketch, "E491", {"start": v(-2.23, -0.53) * mm, "end": v(-2.23, -0.55) * mm});
            skLineSegment(sketch, "E492", {"start": v(-2.23, -0.55) * mm, "end": v(-2.23, -0.56) * mm});
            skLineSegment(sketch, "E493", {"start": v(-2.23, -0.56) * mm, "end": v(-2.22, -0.6) * mm});
            skLineSegment(sketch, "E494", {"start": v(-2.22, -0.6) * mm, "end": v(-2.21, -0.64) * mm});
            skLineSegment(sketch, "E495", {"start": v(-2.21, -0.64) * mm, "end": v(-2.21, -0.7) * mm});
            skLineSegment(sketch, "E496", {"start": v(-2.21, -0.7) * mm, "end": v(-2.22, -0.76) * mm});
            skLineSegment(sketch, "E497", {"start": v(-2.22, -0.76) * mm, "end": v(-2.24, -0.81) * mm});
            skLineSegment(sketch, "E498", {"start": v(-2.24, -0.81) * mm, "end": v(-2.25, -0.87) * mm});
            skLineSegment(sketch, "E499", {"start": v(-2.25, -0.87) * mm, "end": v(-2.27, -0.92) * mm});
            skLineSegment(sketch, "E500", {"start": v(-2.27, -0.92) * mm, "end": v(-2.3, -0.97) * mm});
            skLineSegment(sketch, "E501", {"start": v(-2.3, -0.97) * mm, "end": v(-2.32, -1) * mm});
            skLineSegment(sketch, "E502", {"start": v(-2.32, -1) * mm, "end": v(-2.34, -1.03) * mm});
            skLineSegment(sketch, "E503", {"start": v(-2.34, -1.03) * mm, "end": v(-2.36, -1.04) * mm});
            skLineSegment(sketch, "E504", {"start": v(-2.36, -1.04) * mm, "end": v(-2.38, -1.04) * mm});
            skLineSegment(sketch, "E505", {"start": v(-2.38, -1.04) * mm, "end": v(-2.4, -1.01) * mm});
            skLineSegment(sketch, "E506", {"start": v(-2.4, -1.01) * mm, "end": v(-2.4, -0.97) * mm});
            skLineSegment(sketch, "E507", {"start": v(-2.4, -0.97) * mm, "end": v(-2.4, -0.91) * mm});
            skLineSegment(sketch, "E508", {"start": v(-2.4, -0.91) * mm, "end": v(-2.4, -0.85) * mm});
            skLineSegment(sketch, "E509", {"start": v(-2.4, -0.85) * mm, "end": v(-2.4, -0.82) * mm});
            skLineSegment(sketch, "E510", {"start": v(-2.4, -0.82) * mm, "end": v(-2.41, -0.8) * mm});
            skLineSegment(sketch, "E511", {"start": v(-2.41, -0.8) * mm, "end": v(-2.43, -0.76) * mm});
            skLineSegment(sketch, "E512", {"start": v(-2.43, -0.76) * mm, "end": v(-2.45, -0.74) * mm});
            skLineSegment(sketch, "E513", {"start": v(-2.45, -0.74) * mm, "end": v(-2.48, -0.76) * mm});
            skLineSegment(sketch, "E514", {"start": v(-2.48, -0.76) * mm, "end": v(-2.5, -0.8) * mm});
            skLineSegment(sketch, "E515", {"start": v(-2.5, -0.8) * mm, "end": v(-2.54, -0.86) * mm});
            skLineSegment(sketch, "E516", {"start": v(-2.54, -0.86) * mm, "end": v(-2.57, -0.93) * mm});
            skLineSegment(sketch, "E517", {"start": v(-2.57, -0.93) * mm, "end": v(-2.6, -1.02) * mm});
            skLineSegment(sketch, "E518", {"start": v(-2.6, -1.02) * mm, "end": v(-2.62, -1.1) * mm});
            skLineSegment(sketch, "E519", {"start": v(-2.62, -1.1) * mm, "end": v(-2.65, -1.18) * mm});
            skLineSegment(sketch, "E520", {"start": v(-2.65, -1.18) * mm, "end": v(-2.67, -1.25) * mm});
            skLineSegment(sketch, "E521", {"start": v(-2.67, -1.25) * mm, "end": v(-2.69, -1.3) * mm});
            skLineSegment(sketch, "E522", {"start": v(-2.69, -1.3) * mm, "end": v(-2.7, -1.34) * mm});
            skLineSegment(sketch, "E523", {"start": v(-2.7, -1.34) * mm, "end": v(-2.71, -1.35) * mm});
            skLineSegment(sketch, "E524", {"start": v(-2.71, -1.35) * mm, "end": v(-2.72, -1.31) * mm});
            skLineSegment(sketch, "E525", {"start": v(-2.72, -1.31) * mm, "end": v(-2.72, -1.24) * mm});
            skLineSegment(sketch, "E526", {"start": v(-2.72, -1.24) * mm, "end": v(-2.71, -1.15) * mm});
            skLineSegment(sketch, "E527", {"start": v(-2.71, -1.15) * mm, "end": v(-2.71, -1.12) * mm});
            skLineSegment(sketch, "E528", {"start": v(-2.71, -1.12) * mm, "end": v(-2.72, -1.11) * mm});
            skLineSegment(sketch, "E529", {"start": v(-2.72, -1.11) * mm, "end": v(-2.76, -1.1) * mm});
            skLineSegment(sketch, "E530", {"start": v(-2.76, -1.1) * mm, "end": v(-2.8, -1.13) * mm});
            skLineSegment(sketch, "E531", {"start": v(-2.8, -1.13) * mm, "end": v(-2.85, -1.22) * mm});
            skLineSegment(sketch, "E532", {"start": v(-2.85, -1.22) * mm, "end": v(-2.9, -1.34) * mm});
            skLineSegment(sketch, "E533", {"start": v(-2.9, -1.34) * mm, "end": v(-2.95, -1.48) * mm});
            skLineSegment(sketch, "E534", {"start": v(-2.95, -1.48) * mm, "end": v(-3, -1.6) * mm});
            skLineSegment(sketch, "E535", {"start": v(-3, -1.6) * mm, "end": v(-3.05, -1.72) * mm});
            skLineSegment(sketch, "E536", {"start": v(-3.05, -1.72) * mm, "end": v(-3.09, -1.78) * mm});
            skLineSegment(sketch, "E537", {"start": v(-3.09, -1.78) * mm, "end": v(-3.1, -1.8) * mm});
            skLineSegment(sketch, "E538", {"start": v(-3.1, -1.8) * mm, "end": v(-3.1, -1.8) * mm});
            skLineSegment(sketch, "E539", {"start": v(-3.1, -1.8) * mm, "end": v(-3.12, -1.84) * mm});
            skLineSegment(sketch, "E540", {"start": v(-3.12, -1.84) * mm, "end": v(-3.14, -1.88) * mm});
            skLineSegment(sketch, "E541", {"start": v(-3.14, -1.88) * mm, "end": v(-3.16, -1.91) * mm});
            skLineSegment(sketch, "E542", {"start": v(-3.16, -1.91) * mm, "end": v(-3.18, -1.95) * mm});
            skLineSegment(sketch, "E543", {"start": v(-3.18, -1.95) * mm, "end": v(-3.21, -1.98) * mm});
            skLineSegment(sketch, "E544", {"start": v(-3.21, -1.98) * mm, "end": v(-3.24, -2) * mm});
            skLineSegment(sketch, "E545", {"start": v(-3.24, -2) * mm, "end": v(-3.26, -2.03) * mm});
            skLineSegment(sketch, "E546", {"start": v(-3.26, -2.03) * mm, "end": v(-3.28, -2.04) * mm});
            skLineSegment(sketch, "E547", {"start": v(-3.28, -2.04) * mm, "end": v(-3.3, -2.05) * mm});
            skLineSegment(sketch, "E548", {"start": v(-3.3, -2.05) * mm, "end": v(-3.32, -2.05) * mm});
            skLineSegment(sketch, "E549", {"start": v(-3.32, -2.05) * mm, "end": v(-3.33, -2.05) * mm});
            skLineSegment(sketch, "E550", {"start": v(-3.33, -2.05) * mm, "end": v(-3.33, -2.03) * mm});
            skLineSegment(sketch, "E551", {"start": v(-3.33, -2.03) * mm, "end": v(-3.33, -2) * mm});
            skLineSegment(sketch, "E552", {"start": v(-3.33, -2) * mm, "end": v(-3.31, -1.97) * mm});
            skLineSegment(sketch, "E553", {"start": v(-3.31, -1.97) * mm, "end": v(-3.3, -1.92) * mm});
            skLineSegment(sketch, "E554", {"start": v(-3.3, -1.92) * mm, "end": v(-3.27, -1.87) * mm});
            skLineSegment(sketch, "E555", {"start": v(-3.27, -1.87) * mm, "end": v(-3.26, -1.86) * mm});
            skLineSegment(sketch, "E556", {"start": v(-3.26, -1.86) * mm, "end": v(-3.25, -1.85) * mm});
            skLineSegment(sketch, "E557", {"start": v(-3.25, -1.85) * mm, "end": v(-3.23, -1.82) * mm});
            skLineSegment(sketch, "E558", {"start": v(-3.23, -1.82) * mm, "end": v(-3.2, -1.77) * mm});
            skLineSegment(sketch, "E559", {"start": v(-3.2, -1.77) * mm, "end": v(-3.18, -1.7) * mm});
            skLineSegment(sketch, "E560", {"start": v(-3.18, -1.7) * mm, "end": v(-3.15, -1.64) * mm});
            skLineSegment(sketch, "E561", {"start": v(-3.15, -1.64) * mm, "end": v(-3.13, -1.56) * mm});
            skLineSegment(sketch, "E562", {"start": v(-3.13, -1.56) * mm, "end": v(-3.1, -1.49) * mm});
            skLineSegment(sketch, "E563", {"start": v(-3.1, -1.49) * mm, "end": v(-3.08, -1.41) * mm});
            skLineSegment(sketch, "E564", {"start": v(-3.08, -1.41) * mm, "end": v(-3.07, -1.33) * mm});
            skLineSegment(sketch, "E565", {"start": v(-3.07, -1.33) * mm, "end": v(-3.06, -1.26) * mm});
            skLineSegment(sketch, "E566", {"start": v(-3.06, -1.26) * mm, "end": v(-3.06, -1.2) * mm});
            skLineSegment(sketch, "E567", {"start": v(-3.06, -1.2) * mm, "end": v(-3.06, -1.15) * mm});
            skLineSegment(sketch, "E568", {"start": v(-3.06, -1.15) * mm, "end": v(-3.07, -1.1) * mm});
            skLineSegment(sketch, "E569", {"start": v(-3.07, -1.1) * mm, "end": v(-3.1, -1.08) * mm});
            skLineSegment(sketch, "E570", {"start": v(-3.1, -1.08) * mm, "end": v(-3.12, -1.07) * mm});
            skLineSegment(sketch, "E571", {"start": v(-3.12, -1.07) * mm, "end": v(-3.16, -1.08) * mm});
            skLineSegment(sketch, "E572", {"start": v(-3.16, -1.08) * mm, "end": v(-3.2, -1.1) * mm});
            skLineSegment(sketch, "E573", {"start": v(-3.2, -1.1) * mm, "end": v(-3.2, -1.11) * mm});
            skLineSegment(sketch, "E574", {"start": v(-3.2, -1.11) * mm, "end": v(-3.2, -1.14) * mm});
            skLineSegment(sketch, "E575", {"start": v(-3.2, -1.14) * mm, "end": v(-3.2, -1.21) * mm});
            skLineSegment(sketch, "E576", {"start": v(-3.2, -1.21) * mm, "end": v(-3.23, -1.34) * mm});
            skLineSegment(sketch, "E577", {"start": v(-3.23, -1.34) * mm, "end": v(-3.28, -1.48) * mm});
            skLineSegment(sketch, "E578", {"start": v(-3.28, -1.48) * mm, "end": v(-3.33, -1.62) * mm});
            skLineSegment(sketch, "E579", {"start": v(-3.33, -1.62) * mm, "end": v(-3.39, -1.74) * mm});
            skLineSegment(sketch, "E580", {"start": v(-3.39, -1.74) * mm, "end": v(-3.45, -1.84) * mm});
            skLineSegment(sketch, "E581", {"start": v(-3.45, -1.84) * mm, "end": v(-3.5, -1.88) * mm});
            skLineSegment(sketch, "E582", {"start": v(-3.5, -1.88) * mm, "end": v(-3.54, -1.88) * mm});
            skLineSegment(sketch, "E583", {"start": v(-3.54, -1.88) * mm, "end": v(-3.55, -1.87) * mm});
            skLineSegment(sketch, "E584", {"start": v(-3.55, -1.87) * mm, "end": v(-3.54, -1.86) * mm});
            skLineSegment(sketch, "E585", {"start": v(-3.54, -1.86) * mm, "end": v(-3.53, -1.82) * mm});
            skLineSegment(sketch, "E586", {"start": v(-3.53, -1.82) * mm, "end": v(-3.5, -1.76) * mm});
            skLineSegment(sketch, "E587", {"start": v(-3.5, -1.76) * mm, "end": v(-3.5, -1.68) * mm});
            skLineSegment(sketch, "E588", {"start": v(-3.5, -1.68) * mm, "end": v(-3.5, -1.6) * mm});
            skLineSegment(sketch, "E589", {"start": v(-3.5, -1.6) * mm, "end": v(-3.5, -1.52) * mm});
            skLineSegment(sketch, "E590", {"start": v(-3.5, -1.52) * mm, "end": v(-3.5, -1.43) * mm});
            skLineSegment(sketch, "E591", {"start": v(-3.5, -1.43) * mm, "end": v(-3.5, -1.35) * mm});
            skLineSegment(sketch, "E592", {"start": v(-3.5, -1.35) * mm, "end": v(-3.51, -1.28) * mm});
            skLineSegment(sketch, "E593", {"start": v(-3.51, -1.28) * mm, "end": v(-3.52, -1.21) * mm});
            skLineSegment(sketch, "E594", {"start": v(-3.52, -1.21) * mm, "end": v(-3.54, -1.17) * mm});
            skLineSegment(sketch, "E595", {"start": v(-3.54, -1.17) * mm, "end": v(-3.55, -1.14) * mm});
            skLineSegment(sketch, "E596", {"start": v(-3.55, -1.14) * mm, "end": v(-3.56, -1.13) * mm});
            skLineSegment(sketch, "E597", {"start": v(-3.56, -1.13) * mm, "end": v(-3.58, -1.14) * mm});
            skLineSegment(sketch, "E598", {"start": v(-3.58, -1.14) * mm, "end": v(-3.59, -1.2) * mm});
            skLineSegment(sketch, "E599", {"start": v(-3.59, -1.2) * mm, "end": v(-3.6, -1.27) * mm});
            skLineSegment(sketch, "E600", {"start": v(-3.6, -1.27) * mm, "end": v(-3.6, -1.35) * mm});
            skLineSegment(sketch, "E601", {"start": v(-3.6, -1.35) * mm, "end": v(-3.6, -1.38) * mm});
            skLineSegment(sketch, "E602", {"start": v(-3.6, -1.38) * mm, "end": v(-3.64, -1.42) * mm});
            skLineSegment(sketch, "E603", {"start": v(-3.64, -1.42) * mm, "end": v(-3.75, -1.54) * mm});
            skLineSegment(sketch, "E604", {"start": v(-3.75, -1.54) * mm, "end": v(-3.83, -1.71) * mm});
            skLineSegment(sketch, "E605", {"start": v(-3.83, -1.71) * mm, "end": v(-3.84, -1.9) * mm});
            skLineSegment(sketch, "E606", {"start": v(-3.84, -1.9) * mm, "end": v(-3.81, -2.03) * mm});
            skLineSegment(sketch, "E607", {"start": v(-3.81, -2.03) * mm, "end": v(-3.8, -2.07) * mm});
            skLineSegment(sketch, "E608", {"start": v(-3.8, -2.07) * mm, "end": v(-3.81, -2.07) * mm});
            skLineSegment(sketch, "E609", {"start": v(-3.81, -2.07) * mm, "end": v(-3.86, -2.07) * mm});
            skLineSegment(sketch, "E610", {"start": v(-3.86, -2.07) * mm, "end": v(-3.91, -2.1) * mm});
            skLineSegment(sketch, "E611", {"start": v(-3.91, -2.1) * mm, "end": v(-3.94, -2.15) * mm});
            skLineSegment(sketch, "E612", {"start": v(-3.94, -2.15) * mm, "end": v(-3.95, -2.2) * mm});
            skLineSegment(sketch, "E613", {"start": v(-3.95, -2.2) * mm, "end": v(-3.94, -2.27) * mm});
            skLineSegment(sketch, "E614", {"start": v(-3.94, -2.27) * mm, "end": v(-3.93, -2.34) * mm});
            skLineSegment(sketch, "E615", {"start": v(-3.93, -2.34) * mm, "end": v(-3.9, -2.4) * mm});
            skLineSegment(sketch, "E616", {"start": v(-3.9, -2.4) * mm, "end": v(-3.86, -2.47) * mm});
            skLineSegment(sketch, "E617", {"start": v(-3.86, -2.47) * mm, "end": v(-3.82, -2.53) * mm});
            skLineSegment(sketch, "E618", {"start": v(-3.82, -2.53) * mm, "end": v(-3.77, -2.58) * mm});
            skLineSegment(sketch, "E619", {"start": v(-3.77, -2.58) * mm, "end": v(-3.73, -2.6) * mm});
            skLineSegment(sketch, "E620", {"start": v(-3.73, -2.6) * mm, "end": v(-3.68, -2.62) * mm});
            skLineSegment(sketch, "E621", {"start": v(-3.68, -2.62) * mm, "end": v(-3.64, -2.61) * mm});
            skLineSegment(sketch, "E622", {"start": v(-3.64, -2.61) * mm, "end": v(-3.6, -2.57) * mm});
            skLineSegment(sketch, "E623", {"start": v(-3.6, -2.57) * mm, "end": v(-3.57, -2.5) * mm});
            skLineSegment(sketch, "E624", {"start": v(-3.57, -2.5) * mm, "end": v(-3.56, -2.43) * mm});
            skLineSegment(sketch, "E625", {"start": v(-3.56, -2.43) * mm, "end": v(-3.55, -2.4) * mm});
            skLineSegment(sketch, "E626", {"start": v(-3.55, -2.4) * mm, "end": v(-3.54, -2.41) * mm});
            skLineSegment(sketch, "E627", {"start": v(-3.54, -2.41) * mm, "end": v(-3.48, -2.45) * mm});
            skLineSegment(sketch, "E628", {"start": v(-3.48, -2.45) * mm, "end": v(-3.4, -2.49) * mm});
            skLineSegment(sketch, "E629", {"start": v(-3.4, -2.49) * mm, "end": v(-3.32, -2.52) * mm});
            skLineSegment(sketch, "E630", {"start": v(-3.32, -2.52) * mm, "end": v(-3.23, -2.53) * mm});
            skLineSegment(sketch, "E631", {"start": v(-3.23, -2.53) * mm, "end": v(-3.14, -2.53) * mm});
            skLineSegment(sketch, "E632", {"start": v(-3.14, -2.53) * mm, "end": v(-3.05, -2.52) * mm});
            skLineSegment(sketch, "E633", {"start": v(-3.05, -2.52) * mm, "end": v(-2.96, -2.5) * mm});
            skLineSegment(sketch, "E634", {"start": v(-2.96, -2.5) * mm, "end": v(-2.88, -2.47) * mm});
            skLineSegment(sketch, "E635", {"start": v(-2.88, -2.47) * mm, "end": v(-2.8, -2.44) * mm});
            skLineSegment(sketch, "E636", {"start": v(-2.8, -2.44) * mm, "end": v(-2.72, -2.4) * mm});
            skLineSegment(sketch, "E637", {"start": v(-2.72, -2.4) * mm, "end": v(-2.65, -2.34) * mm});
            skLineSegment(sketch, "E638", {"start": v(-2.65, -2.34) * mm, "end": v(-2.59, -2.28) * mm});
            skLineSegment(sketch, "E639", {"start": v(-2.59, -2.28) * mm, "end": v(-2.53, -2.22) * mm});
            skLineSegment(sketch, "E640", {"start": v(-2.53, -2.22) * mm, "end": v(-2.5, -2.15) * mm});
            skLineSegment(sketch, "E641", {"start": v(-2.5, -2.15) * mm, "end": v(-2.47, -2.07) * mm});
            skLineSegment(sketch, "E642", {"start": v(-2.47, -2.07) * mm, "end": v(-2.45, -2.02) * mm});
            skLineSegment(sketch, "E643", {"start": v(-2.45, -2.02) * mm, "end": v(-2.45, -2) * mm});
            skLineSegment(sketch, "E644", {"start": v(-2.45, -2) * mm, "end": v(-2.47, -1.98) * mm});
            skLineSegment(sketch, "E645", {"start": v(-2.47, -1.98) * mm, "end": v(-2.52, -1.92) * mm});
            skLineSegment(sketch, "E646", {"start": v(-2.52, -1.92) * mm, "end": v(-2.55, -1.84) * mm});
            skLineSegment(sketch, "E647", {"start": v(-2.55, -1.84) * mm, "end": v(-2.54, -1.76) * mm});
            skLineSegment(sketch, "E648", {"start": v(-2.54, -1.76) * mm, "end": v(-2.52, -1.69) * mm});
            skLineSegment(sketch, "E649", {"start": v(-2.52, -1.69) * mm, "end": v(-2.47, -1.62) * mm});
            skLineSegment(sketch, "E650", {"start": v(-2.47, -1.62) * mm, "end": v(-2.4, -1.56) * mm});
            skLineSegment(sketch, "E651", {"start": v(-2.4, -1.56) * mm, "end": v(-2.32, -1.5) * mm});
            skLineSegment(sketch, "E652", {"start": v(-2.32, -1.5) * mm, "end": v(-2.23, -1.46) * mm});
            skLineSegment(sketch, "E653", {"start": v(-2.23, -1.46) * mm, "end": v(-2.14, -1.42) * mm});
            skLineSegment(sketch, "E654", {"start": v(-2.14, -1.42) * mm, "end": v(-2.05, -1.4) * mm});
            skLineSegment(sketch, "E655", {"start": v(-2.05, -1.4) * mm, "end": v(-1.95, -1.4) * mm});
            skLineSegment(sketch, "E656", {"start": v(-1.95, -1.4) * mm, "end": v(-1.87, -1.4) * mm});
            skLineSegment(sketch, "E657", {"start": v(-1.87, -1.4) * mm, "end": v(-1.8, -1.43) * mm});
            skLineSegment(sketch, "E658", {"start": v(-1.8, -1.43) * mm, "end": v(-1.74, -1.47) * mm});
            skLineSegment(sketch, "E659", {"start": v(-1.74, -1.47) * mm, "end": v(-1.7, -1.53) * mm});
            skLineSegment(sketch, "E660", {"start": v(-1.7, -1.53) * mm, "end": v(-1.69, -1.6) * mm});
            skLineSegment(sketch, "E661", {"start": v(-1.69, -1.6) * mm, "end": v(-1.69, -1.61) * mm});
            skLineSegment(sketch, "E662", {"start": v(-1.69, -1.61) * mm, "end": v(-1.7, -1.6) * mm});
            skLineSegment(sketch, "E663", {"start": v(-1.7, -1.6) * mm, "end": v(-1.74, -1.58) * mm});
            skLineSegment(sketch, "E664", {"start": v(-1.74, -1.58) * mm, "end": v(-1.8, -1.57) * mm});
            skLineSegment(sketch, "E665", {"start": v(-1.8, -1.57) * mm, "end": v(-1.86, -1.57) * mm});
            skLineSegment(sketch, "E666", {"start": v(-1.86, -1.57) * mm, "end": v(-1.91, -1.58) * mm});
            skLineSegment(sketch, "E667", {"start": v(-1.91, -1.58) * mm, "end": v(-1.97, -1.6) * mm});
            skLineSegment(sketch, "E668", {"start": v(-1.97, -1.6) * mm, "end": v(-2.02, -1.63) * mm});
            skLineSegment(sketch, "E669", {"start": v(-2.02, -1.63) * mm, "end": v(-2.07, -1.66) * mm});
            skLineSegment(sketch, "E670", {"start": v(-2.07, -1.66) * mm, "end": v(-2.1, -1.7) * mm});
            skLineSegment(sketch, "E671", {"start": v(-2.1, -1.7) * mm, "end": v(-2.14, -1.73) * mm});
            skLineSegment(sketch, "E672", {"start": v(-2.14, -1.73) * mm, "end": v(-2.16, -1.76) * mm});
            skLineSegment(sketch, "E673", {"start": v(-2.16, -1.76) * mm, "end": v(-2.17, -1.79) * mm});
            skLineSegment(sketch, "E674", {"start": v(-2.17, -1.79) * mm, "end": v(-2.16, -1.8) * mm});
            skLineSegment(sketch, "E675", {"start": v(-2.16, -1.8) * mm, "end": v(-2.14, -1.81) * mm});
            skLineSegment(sketch, "E676", {"start": v(-2.14, -1.81) * mm, "end": v(-2.11, -1.8) * mm});
            skLineSegment(sketch, "E677", {"start": v(-2.11, -1.8) * mm, "end": v(-2.06, -1.79) * mm});
            skLineSegment(sketch, "E678", {"start": v(-2.06, -1.79) * mm, "end": v(-2, -1.76) * mm});
            skLineSegment(sketch, "E679", {"start": v(-2, -1.76) * mm, "end": v(-1.99, -1.75) * mm});
            skLineSegment(sketch, "E680", {"start": v(-1.99, -1.75) * mm, "end": v(-1.98, -1.74) * mm});
            skLineSegment(sketch, "E681", {"start": v(-1.98, -1.74) * mm, "end": v(-1.94, -1.72) * mm});
            skLineSegment(sketch, "E682", {"start": v(-1.94, -1.72) * mm, "end": v(-1.89, -1.7) * mm});
            skLineSegment(sketch, "E683", {"start": v(-1.89, -1.7) * mm, "end": v(-1.83, -1.7) * mm});
            skLineSegment(sketch, "E684", {"start": v(-1.83, -1.7) * mm, "end": v(-1.76, -1.7) * mm});
            skLineSegment(sketch, "E685", {"start": v(-1.76, -1.7) * mm, "end": v(-1.7, -1.72) * mm});
            skLineSegment(sketch, "E686", {"start": v(-1.7, -1.72) * mm, "end": v(-1.64, -1.73) * mm});
            skLineSegment(sketch, "E687", {"start": v(-1.64, -1.73) * mm, "end": v(-1.58, -1.76) * mm});
            skLineSegment(sketch, "E688", {"start": v(-1.58, -1.76) * mm, "end": v(-1.53, -1.78) * mm});
            skLineSegment(sketch, "E689", {"start": v(-1.53, -1.78) * mm, "end": v(-1.5, -1.8) * mm});
            skLineSegment(sketch, "E690", {"start": v(-1.5, -1.8) * mm, "end": v(-1.47, -1.83) * mm});
            skLineSegment(sketch, "E691", {"start": v(-1.47, -1.83) * mm, "end": v(-1.45, -1.86) * mm});
            skLineSegment(sketch, "E692", {"start": v(-1.45, -1.86) * mm, "end": v(-1.45, -1.88) * mm});
            skLineSegment(sketch, "E693", {"start": v(-1.45, -1.88) * mm, "end": v(-1.47, -1.9) * mm});
            skLineSegment(sketch, "E694", {"start": v(-1.47, -1.9) * mm, "end": v(-1.51, -1.91) * mm});
            skLineSegment(sketch, "E695", {"start": v(-1.51, -1.91) * mm, "end": v(-1.58, -1.92) * mm});
            skLineSegment(sketch, "E696", {"start": v(-1.58, -1.92) * mm, "end": v(-1.65, -1.92) * mm});
            skLineSegment(sketch, "E697", {"start": v(-1.65, -1.92) * mm, "end": v(-1.67, -1.92) * mm});
            skLineSegment(sketch, "E698", {"start": v(-1.67, -1.92) * mm, "end": v(-1.7, -1.92) * mm});
            skLineSegment(sketch, "E699", {"start": v(-1.7, -1.92) * mm, "end": v(-1.77, -1.93) * mm});
            skLineSegment(sketch, "E700", {"start": v(-1.77, -1.93) * mm, "end": v(-1.86, -1.96) * mm});
            skLineSegment(sketch, "E701", {"start": v(-1.86, -1.96) * mm, "end": v(-1.94, -2) * mm});
            skLineSegment(sketch, "E702", {"start": v(-1.94, -2) * mm, "end": v(-2, -2.07) * mm});
            skLineSegment(sketch, "E703", {"start": v(-2, -2.07) * mm, "end": v(-2.06, -2.15) * mm});
            skLineSegment(sketch, "E704", {"start": v(-2.06, -2.15) * mm, "end": v(-2.1, -2.23) * mm});
            skLineSegment(sketch, "E705", {"start": v(-2.1, -2.23) * mm, "end": v(-2.15, -2.31) * mm});
            skLineSegment(sketch, "E706", {"start": v(-2.15, -2.31) * mm, "end": v(-2.2, -2.4) * mm});
            skLineSegment(sketch, "E707", {"start": v(-2.2, -2.4) * mm, "end": v(-2.24, -2.49) * mm});
            skLineSegment(sketch, "E708", {"start": v(-2.24, -2.49) * mm, "end": v(-2.3, -2.57) * mm});
            skLineSegment(sketch, "E709", {"start": v(-2.3, -2.57) * mm, "end": v(-2.35, -2.64) * mm});
            skLineSegment(sketch, "E710", {"start": v(-2.35, -2.64) * mm, "end": v(-2.41, -2.7) * mm});
            skLineSegment(sketch, "E711", {"start": v(-2.41, -2.7) * mm, "end": v(-2.49, -2.74) * mm});
            skLineSegment(sketch, "E712", {"start": v(-2.49, -2.74) * mm, "end": v(-2.58, -2.77) * mm});
            skLineSegment(sketch, "E713", {"start": v(-2.58, -2.77) * mm, "end": v(-2.68, -2.78) * mm});
            skLineSegment(sketch, "E714", {"start": v(-2.68, -2.78) * mm, "end": v(-2.77, -2.77) * mm});
            skLineSegment(sketch, "E715", {"start": v(-2.77, -2.77) * mm, "end": v(-2.8, -2.76) * mm});
            skLineSegment(sketch, "E716", {"start": v(-2.8, -2.76) * mm, "end": v(-2.82, -2.75) * mm});
            skLineSegment(sketch, "E717", {"start": v(-2.82, -2.75) * mm, "end": v(-2.87, -2.75) * mm});
            skLineSegment(sketch, "E718", {"start": v(-2.87, -2.75) * mm, "end": v(-2.94, -2.75) * mm});
            skLineSegment(sketch, "E719", {"start": v(-2.94, -2.75) * mm, "end": v(-3, -2.76) * mm});
            skLineSegment(sketch, "E720", {"start": v(-3, -2.76) * mm, "end": v(-3.04, -2.78) * mm});
            skLineSegment(sketch, "E721", {"start": v(-3.04, -2.78) * mm, "end": v(-3.08, -2.81) * mm});
            skLineSegment(sketch, "E722", {"start": v(-3.08, -2.81) * mm, "end": v(-3.11, -2.85) * mm});
            skLineSegment(sketch, "E723", {"start": v(-3.11, -2.85) * mm, "end": v(-3.14, -2.89) * mm});
            skLineSegment(sketch, "E724", {"start": v(-3.14, -2.89) * mm, "end": v(-3.15, -2.93) * mm});
            skLineSegment(sketch, "E725", {"start": v(-3.15, -2.93) * mm, "end": v(-3.15, -2.97) * mm});
            skLineSegment(sketch, "E726", {"start": v(-3.15, -2.97) * mm, "end": v(-3.15, -3) * mm});
            skLineSegment(sketch, "E727", {"start": v(-3.15, -3) * mm, "end": v(-3.13, -3.04) * mm});
            skLineSegment(sketch, "E728", {"start": v(-3.13, -3.04) * mm, "end": v(-3.1, -3.07) * mm});
            skLineSegment(sketch, "E729", {"start": v(-3.1, -3.07) * mm, "end": v(-3.06, -3.08) * mm});
            skLineSegment(sketch, "E730", {"start": v(-3.06, -3.08) * mm, "end": v(-3.01, -3.1) * mm});
            skLineSegment(sketch, "E731", {"start": v(-3.01, -3.1) * mm, "end": v(-2.95, -3.08) * mm});
            skLineSegment(sketch, "E732", {"start": v(-2.95, -3.08) * mm, "end": v(-2.89, -3.07) * mm});
            skLineSegment(sketch, "E733", {"start": v(-2.89, -3.07) * mm, "end": v(-2.87, -3.06) * mm});
            skLineSegment(sketch, "E734", {"start": v(-2.87, -3.06) * mm, "end": v(-2.84, -3.06) * mm});
            skLineSegment(sketch, "E735", {"start": v(-2.84, -3.06) * mm, "end": v(-2.75, -3.04) * mm});
            skLineSegment(sketch, "E736", {"start": v(-2.75, -3.04) * mm, "end": v(-2.64, -2.99) * mm});
            skLineSegment(sketch, "E737", {"start": v(-2.64, -2.99) * mm, "end": v(-2.54, -2.93) * mm});
            skLineSegment(sketch, "E738", {"start": v(-2.54, -2.93) * mm, "end": v(-2.44, -2.85) * mm});
            skLineSegment(sketch, "E739", {"start": v(-2.44, -2.85) * mm, "end": v(-2.34, -2.77) * mm});
            skLineSegment(sketch, "E740", {"start": v(-2.34, -2.77) * mm, "end": v(-2.24, -2.7) * mm});
            skLineSegment(sketch, "E741", {"start": v(-2.24, -2.7) * mm, "end": v(-2.14, -2.63) * mm});
            skLineSegment(sketch, "E742", {"start": v(-2.14, -2.63) * mm, "end": v(-2.05, -2.6) * mm});
            skLineSegment(sketch, "E743", {"start": v(-2.05, -2.6) * mm, "end": v(-2.02, -2.58) * mm});
            skLineSegment(sketch, "E744", {"start": v(-2.02, -2.58) * mm, "end": v(-2.02, -2.56) * mm});
            skLineSegment(sketch, "E745", {"start": v(-2.02, -2.56) * mm, "end": v(-2, -2.48) * mm});
            skLineSegment(sketch, "E746", {"start": v(-2, -2.48) * mm, "end": v(-1.96, -2.4) * mm});
            skLineSegment(sketch, "E747", {"start": v(-1.96, -2.4) * mm, "end": v(-1.9, -2.35) * mm});
            skLineSegment(sketch, "E748", {"start": v(-1.9, -2.35) * mm, "end": v(-1.83, -2.32) * mm});
            skLineSegment(sketch, "E749", {"start": v(-1.83, -2.32) * mm, "end": v(-1.75, -2.31) * mm});
            skLineSegment(sketch, "E750", {"start": v(-1.75, -2.31) * mm, "end": v(-1.66, -2.31) * mm});
            skLineSegment(sketch, "E751", {"start": v(-1.66, -2.31) * mm, "end": v(-1.57, -2.33) * mm});
            skLineSegment(sketch, "E752", {"start": v(-1.57, -2.33) * mm, "end": v(-1.47, -2.35) * mm});
            skLineSegment(sketch, "E753", {"start": v(-1.47, -2.35) * mm, "end": v(-1.38, -2.39) * mm});
            skLineSegment(sketch, "E754", {"start": v(-1.38, -2.39) * mm, "end": v(-1.3, -2.43) * mm});
            skLineSegment(sketch, "E755", {"start": v(-1.3, -2.43) * mm, "end": v(-1.23, -2.47) * mm});
            skLineSegment(sketch, "E756", {"start": v(-1.23, -2.47) * mm, "end": v(-1.17, -2.5) * mm});
            skLineSegment(sketch, "E757", {"start": v(-1.17, -2.5) * mm, "end": v(-1.12, -2.54) * mm});
            skLineSegment(sketch, "E758", {"start": v(-1.12, -2.54) * mm, "end": v(-1.1, -2.58) * mm});
            skLineSegment(sketch, "E759", {"start": v(-1.1, -2.58) * mm, "end": v(-1.1, -2.6) * mm});
            skLineSegment(sketch, "E760", {"start": v(-1.1, -2.6) * mm, "end": v(-1.13, -2.62) * mm});
            skLineSegment(sketch, "E761", {"start": v(-1.13, -2.62) * mm, "end": v(-1.14, -2.62) * mm});
            skLineSegment(sketch, "E762", {"start": v(-1.14, -2.62) * mm, "end": v(-1.15, -2.6) * mm});
            skLineSegment(sketch, "E763", {"start": v(-1.15, -2.6) * mm, "end": v(-1.2, -2.6) * mm});
            skLineSegment(sketch, "E764", {"start": v(-1.2, -2.6) * mm, "end": v(-1.25, -2.58) * mm});
            skLineSegment(sketch, "E765", {"start": v(-1.25, -2.58) * mm, "end": v(-1.3, -2.58) * mm});
            skLineSegment(sketch, "E766", {"start": v(-1.3, -2.58) * mm, "end": v(-1.37, -2.58) * mm});
            skLineSegment(sketch, "E767", {"start": v(-1.37, -2.58) * mm, "end": v(-1.43, -2.6) * mm});
            skLineSegment(sketch, "E768", {"start": v(-1.43, -2.6) * mm, "end": v(-1.49, -2.61) * mm});
            skLineSegment(sketch, "E769", {"start": v(-1.49, -2.61) * mm, "end": v(-1.54, -2.63) * mm});
            skLineSegment(sketch, "E770", {"start": v(-1.54, -2.63) * mm, "end": v(-1.58, -2.66) * mm});
            skLineSegment(sketch, "E771", {"start": v(-1.58, -2.66) * mm, "end": v(-1.62, -2.68) * mm});
            skLineSegment(sketch, "E772", {"start": v(-1.62, -2.68) * mm, "end": v(-1.64, -2.7) * mm});
            skLineSegment(sketch, "E773", {"start": v(-1.64, -2.7) * mm, "end": v(-1.65, -2.72) * mm});
            skLineSegment(sketch, "E774", {"start": v(-1.65, -2.72) * mm, "end": v(-1.64, -2.73) * mm});
            skLineSegment(sketch, "E775", {"start": v(-1.64, -2.73) * mm, "end": v(-1.61, -2.73) * mm});
            skLineSegment(sketch, "E776", {"start": v(-1.61, -2.73) * mm, "end": v(-1.57, -2.73) * mm});
            skLineSegment(sketch, "E777", {"start": v(-1.57, -2.73) * mm, "end": v(-1.5, -2.7) * mm});
            skLineSegment(sketch, "E778", {"start": v(-1.5, -2.7) * mm, "end": v(-1.43, -2.69) * mm});
            skLineSegment(sketch, "E779", {"start": v(-1.43, -2.69) * mm, "end": v(-1.4, -2.68) * mm});
            skLineSegment(sketch, "E780", {"start": v(-1.4, -2.68) * mm, "end": v(-1.4, -2.67) * mm});
            skLineSegment(sketch, "E781", {"start": v(-1.4, -2.67) * mm, "end": v(-1.34, -2.67) * mm});
            skLineSegment(sketch, "E782", {"start": v(-1.34, -2.67) * mm, "end": v(-1.28, -2.68) * mm});
            skLineSegment(sketch, "E783", {"start": v(-1.28, -2.68) * mm, "end": v(-1.22, -2.71) * mm});
            skLineSegment(sketch, "E784", {"start": v(-1.22, -2.71) * mm, "end": v(-1.17, -2.76) * mm});
            skLineSegment(sketch, "E785", {"start": v(-1.17, -2.76) * mm, "end": v(-1.12, -2.81) * mm});
            skLineSegment(sketch, "E786", {"start": v(-1.12, -2.81) * mm, "end": v(-1.08, -2.88) * mm});
            skLineSegment(sketch, "E787", {"start": v(-1.08, -2.88) * mm, "end": v(-1.05, -2.94) * mm});
            skLineSegment(sketch, "E788", {"start": v(-1.05, -2.94) * mm, "end": v(-1.03, -3) * mm});
            skLineSegment(sketch, "E789", {"start": v(-1.03, -3) * mm, "end": v(-1.01, -3.07) * mm});
            skLineSegment(sketch, "E790", {"start": v(-1.01, -3.07) * mm, "end": v(-1, -3.12) * mm});
            skLineSegment(sketch, "E791", {"start": v(-1, -3.12) * mm, "end": v(-1, -3.16) * mm});
            skLineSegment(sketch, "E792", {"start": v(-1, -3.16) * mm, "end": v(-1.02, -3.19) * mm});
            skLineSegment(sketch, "E793", {"start": v(-1.02, -3.19) * mm, "end": v(-1.05, -3.2) * mm});
            skLineSegment(sketch, "E794", {"start": v(-1.05, -3.2) * mm, "end": v(-1.08, -3.18) * mm});
            skLineSegment(sketch, "E795", {"start": v(-1.08, -3.18) * mm, "end": v(-1.12, -3.14) * mm});
            skLineSegment(sketch, "E796", {"start": v(-1.12, -3.14) * mm, "end": v(-1.17, -3.08) * mm});
            skLineSegment(sketch, "E797", {"start": v(-1.17, -3.08) * mm, "end": v(-1.18, -3.06) * mm});
            skLineSegment(sketch, "E798", {"start": v(-1.18, -3.06) * mm, "end": v(-1.22, -3.04) * mm});
            skLineSegment(sketch, "E799", {"start": v(-1.22, -3.04) * mm, "end": v(-1.37, -3) * mm});
            skLineSegment(sketch, "E800", {"start": v(-1.37, -3) * mm, "end": v(-1.55, -2.99) * mm});
            skLineSegment(sketch, "E801", {"start": v(-1.55, -2.99) * mm, "end": v(-1.74, -3) * mm});
            skLineSegment(sketch, "E802", {"start": v(-1.74, -3) * mm, "end": v(-1.93, -3.06) * mm});
            skLineSegment(sketch, "E803", {"start": v(-1.93, -3.06) * mm, "end": v(-2.11, -3.13) * mm});
            skLineSegment(sketch, "E804", {"start": v(-2.11, -3.13) * mm, "end": v(-2.3, -3.21) * mm});
            skLineSegment(sketch, "E805", {"start": v(-2.3, -3.21) * mm, "end": v(-2.48, -3.3) * mm});
            skLineSegment(sketch, "E806", {"start": v(-2.48, -3.3) * mm, "end": v(-2.61, -3.36) * mm});
            skLineSegment(sketch, "E807", {"start": v(-2.61, -3.36) * mm, "end": v(-2.66, -3.38) * mm});
            skLineSegment(sketch, "E808", {"start": v(-2.66, -3.38) * mm, "end": v(-2.68, -3.4) * mm});
            skLineSegment(sketch, "E809", {"start": v(-2.68, -3.4) * mm, "end": v(-2.76, -3.44) * mm});
            skLineSegment(sketch, "E810", {"start": v(-2.76, -3.44) * mm, "end": v(-2.85, -3.51) * mm});
            skLineSegment(sketch, "E811", {"start": v(-2.85, -3.51) * mm, "end": v(-2.93, -3.58) * mm});
            skLineSegment(sketch, "E812", {"start": v(-2.93, -3.58) * mm, "end": v(-2.98, -3.65) * mm});
            skLineSegment(sketch, "E813", {"start": v(-2.98, -3.65) * mm, "end": v(-3, -3.73) * mm});
            skLineSegment(sketch, "E814", {"start": v(-3, -3.73) * mm, "end": v(-2.96, -3.8) * mm});
            skLineSegment(sketch, "E815", {"start": v(-2.96, -3.8) * mm, "end": v(-2.89, -3.86) * mm});
            skLineSegment(sketch, "E816", {"start": v(-2.89, -3.86) * mm, "end": v(-2.79, -3.91) * mm});
            skLineSegment(sketch, "E817", {"start": v(-2.79, -3.91) * mm, "end": v(-2.75, -3.92) * mm});
            skLineSegment(sketch, "E818", {"start": v(-2.75, -3.92) * mm, "end": v(-2.67, -3.98) * mm});
            skLineSegment(sketch, "E819", {"start": v(-2.67, -3.98) * mm, "end": v(-2.4, -4.15) * mm});
            skLineSegment(sketch, "E820", {"start": v(-2.4, -4.15) * mm, "end": v(-2.03, -4.35) * mm});
            skLineSegment(sketch, "E821", {"start": v(-2.03, -4.35) * mm, "end": v(-1.65, -4.5) * mm});
            skLineSegment(sketch, "E822", {"start": v(-1.65, -4.5) * mm, "end": v(-1.25, -4.64) * mm});
            skLineSegment(sketch, "E823", {"start": v(-1.25, -4.64) * mm, "end": v(-0.84, -4.73) * mm});
            skLineSegment(sketch, "E824", {"start": v(-0.84, -4.73) * mm, "end": v(-0.43, -4.78) * mm});
            skLineSegment(sketch, "E825", {"start": v(-0.43, -4.78) * mm, "end": v(0, -4.8) * mm});
            skLineSegment(sketch, "E826", {"start": v(0, -4.8) * mm, "end": v(0.3, -4.8) * mm});
            skLineSegment(sketch, "E827", {"start": v(0.3, -4.8) * mm, "end": v(0.4, -4.78) * mm});
            skLineSegment(sketch, "E828", {"start": v(1.7, -2.42) * mm, "end": v(1.69, -2.4) * mm});
            skLineSegment(sketch, "E829", {"start": v(1.69, -2.4) * mm, "end": v(1.64, -2.36) * mm});
            skLineSegment(sketch, "E830", {"start": v(1.64, -2.36) * mm, "end": v(1.6, -2.3) * mm});
            skLineSegment(sketch, "E831", {"start": v(1.6, -2.3) * mm, "end": v(1.6, -2.23) * mm});
            skLineSegment(sketch, "E832", {"start": v(1.6, -2.23) * mm, "end": v(1.6, -2.15) * mm});
            skLineSegment(sketch, "E833", {"start": v(1.6, -2.15) * mm, "end": v(1.64, -2.08) * mm});
            skLineSegment(sketch, "E834", {"start": v(1.64, -2.08) * mm, "end": v(1.69, -2.01) * mm});
            skLineSegment(sketch, "E835", {"start": v(1.69, -2.01) * mm, "end": v(1.75, -1.95) * mm});
            skLineSegment(sketch, "E836", {"start": v(1.75, -1.95) * mm, "end": v(1.8, -1.91) * mm});
            skLineSegment(sketch, "E837", {"start": v(1.8, -1.91) * mm, "end": v(1.82, -1.9) * mm});
            skLineSegment(sketch, "E838", {"start": v(1.82, -1.9) * mm, "end": v(1.82, -1.91) * mm});
            skLineSegment(sketch, "E839", {"start": v(1.82, -1.91) * mm, "end": v(1.82, -1.94) * mm});
            skLineSegment(sketch, "E840", {"start": v(1.82, -1.94) * mm, "end": v(1.8, -1.98) * mm});
            skLineSegment(sketch, "E841", {"start": v(1.8, -1.98) * mm, "end": v(1.8, -2.01) * mm});
            skLineSegment(sketch, "E842", {"start": v(1.8, -2.01) * mm, "end": v(1.79, -2.05) * mm});
            skLineSegment(sketch, "E843", {"start": v(1.79, -2.05) * mm, "end": v(1.78, -2.08) * mm});
            skLineSegment(sketch, "E844", {"start": v(1.78, -2.08) * mm, "end": v(1.76, -2.12) * mm});
            skLineSegment(sketch, "E845", {"start": v(1.76, -2.12) * mm, "end": v(1.76, -2.14) * mm});
            skLineSegment(sketch, "E846", {"start": v(1.76, -2.14) * mm, "end": v(1.75, -2.16) * mm});
            skLineSegment(sketch, "E847", {"start": v(1.75, -2.16) * mm, "end": v(1.74, -2.18) * mm});
            skLineSegment(sketch, "E848", {"start": v(1.74, -2.18) * mm, "end": v(1.75, -2.19) * mm});
            skLineSegment(sketch, "E849", {"start": v(1.75, -2.19) * mm, "end": v(1.75, -2.2) * mm});
            skLineSegment(sketch, "E850", {"start": v(1.75, -2.2) * mm, "end": v(1.76, -2.18) * mm});
            skLineSegment(sketch, "E851", {"start": v(1.76, -2.18) * mm, "end": v(1.78, -2.17) * mm});
            skLineSegment(sketch, "E852", {"start": v(1.78, -2.17) * mm, "end": v(1.8, -2.14) * mm});
            skLineSegment(sketch, "E853", {"start": v(1.8, -2.14) * mm, "end": v(1.84, -2.1) * mm});
            skLineSegment(sketch, "E854", {"start": v(1.84, -2.1) * mm, "end": v(1.87, -2.06) * mm});
            skLineSegment(sketch, "E855", {"start": v(1.87, -2.06) * mm, "end": v(1.88, -2.05) * mm});
            skLineSegment(sketch, "E856", {"start": v(1.88, -2.05) * mm, "end": v(1.89, -2.05) * mm});
            skLineSegment(sketch, "E857", {"start": v(1.89, -2.05) * mm, "end": v(1.91, -2.06) * mm});
            skLineSegment(sketch, "E858", {"start": v(1.91, -2.06) * mm, "end": v(1.93, -2.1) * mm});
            skLineSegment(sketch, "E859", {"start": v(1.93, -2.1) * mm, "end": v(1.92, -2.18) * mm});
            skLineSegment(sketch, "E860", {"start": v(1.92, -2.18) * mm, "end": v(1.9, -2.27) * mm});
            skLineSegment(sketch, "E861", {"start": v(1.9, -2.27) * mm, "end": v(1.86, -2.36) * mm});
            skLineSegment(sketch, "E862", {"start": v(1.86, -2.36) * mm, "end": v(1.82, -2.42) * mm});
            skLineSegment(sketch, "E863", {"start": v(1.82, -2.42) * mm, "end": v(1.76, -2.44) * mm});
            skLineSegment(sketch, "E864", {"start": v(1.76, -2.44) * mm, "end": v(1.71, -2.43) * mm});
            skLineSegment(sketch, "E865", {"start": v(1.71, -2.43) * mm, "end": v(1.7, -2.42) * mm});
            skLineSegment(sketch, "E866", {"start": v(1.37, -2.2) * mm, "end": v(1.37, -2.2) * mm});
            skLineSegment(sketch, "E867", {"start": v(1.37, -2.2) * mm, "end": v(1.36, -2.16) * mm});
            skLineSegment(sketch, "E868", {"start": v(1.36, -2.16) * mm, "end": v(1.37, -2.1) * mm});
            skLineSegment(sketch, "E869", {"start": v(1.37, -2.1) * mm, "end": v(1.4, -2.05) * mm});
            skLineSegment(sketch, "E870", {"start": v(1.4, -2.05) * mm, "end": v(1.42, -2) * mm});
            skLineSegment(sketch, "E871", {"start": v(1.42, -2) * mm, "end": v(1.46, -1.94) * mm});
            skLineSegment(sketch, "E872", {"start": v(1.46, -1.94) * mm, "end": v(1.5, -1.89) * mm});
            skLineSegment(sketch, "E873", {"start": v(1.5, -1.89) * mm, "end": v(1.55, -1.84) * mm});
            skLineSegment(sketch, "E874", {"start": v(1.55, -1.84) * mm, "end": v(1.59, -1.8) * mm});
            skLineSegment(sketch, "E875", {"start": v(1.59, -1.8) * mm, "end": v(1.63, -1.78) * mm});
            skLineSegment(sketch, "E876", {"start": v(1.63, -1.78) * mm, "end": v(1.66, -1.76) * mm});
            skLineSegment(sketch, "E877", {"start": v(1.66, -1.76) * mm, "end": v(1.7, -1.75) * mm});
            skLineSegment(sketch, "E878", {"start": v(1.7, -1.75) * mm, "end": v(1.7, -1.76) * mm});
            skLineSegment(sketch, "E879", {"start": v(1.7, -1.76) * mm, "end": v(1.71, -1.79) * mm});
            skLineSegment(sketch, "E880", {"start": v(1.71, -1.79) * mm, "end": v(1.7, -1.83) * mm});
            skLineSegment(sketch, "E881", {"start": v(1.7, -1.83) * mm, "end": v(1.67, -1.9) * mm});
            skLineSegment(sketch, "E882", {"start": v(1.67, -1.9) * mm, "end": v(1.64, -1.96) * mm});
            skLineSegment(sketch, "E883", {"start": v(1.64, -1.96) * mm, "end": v(1.63, -1.98) * mm});
            skLineSegment(sketch, "E884", {"start": v(1.63, -1.98) * mm, "end": v(1.62, -1.98) * mm});
            skLineSegment(sketch, "E885", {"start": v(1.62, -1.98) * mm, "end": v(1.6, -2.01) * mm});
            skLineSegment(sketch, "E886", {"start": v(1.6, -2.01) * mm, "end": v(1.58, -2.06) * mm});
            skLineSegment(sketch, "E887", {"start": v(1.58, -2.06) * mm, "end": v(1.56, -2.1) * mm});
            skLineSegment(sketch, "E888", {"start": v(1.56, -2.1) * mm, "end": v(1.53, -2.15) * mm});
            skLineSegment(sketch, "E889", {"start": v(1.53, -2.15) * mm, "end": v(1.5, -2.2) * mm});
            skLineSegment(sketch, "E890", {"start": v(1.5, -2.2) * mm, "end": v(1.46, -2.22) * mm});
            skLineSegment(sketch, "E891", {"start": v(1.46, -2.22) * mm, "end": v(1.42, -2.22) * mm});
            skLineSegment(sketch, "E892", {"start": v(1.42, -2.22) * mm, "end": v(1.38, -2.21) * mm});
            skLineSegment(sketch, "E893", {"start": v(1.38, -2.21) * mm, "end": v(1.37, -2.2) * mm});
            skLineSegment(sketch, "E894", {"start": v(1.12, -2.12) * mm, "end": v(1.12, -2.11) * mm});
            skLineSegment(sketch, "E895", {"start": v(1.12, -2.11) * mm, "end": v(1.1, -2.08) * mm});
            skLineSegment(sketch, "E896", {"start": v(1.1, -2.08) * mm, "end": v(1.11, -2.03) * mm});
            skLineSegment(sketch, "E897", {"start": v(1.11, -2.03) * mm, "end": v(1.13, -1.99) * mm});
            skLineSegment(sketch, "E898", {"start": v(1.13, -1.99) * mm, "end": v(1.17, -1.95) * mm});
            skLineSegment(sketch, "E899", {"start": v(1.17, -1.95) * mm, "end": v(1.2, -1.92) * mm});
            skLineSegment(sketch, "E900", {"start": v(1.2, -1.92) * mm, "end": v(1.25, -1.89) * mm});
            skLineSegment(sketch, "E901", {"start": v(1.25, -1.89) * mm, "end": v(1.3, -1.86) * mm});
            skLineSegment(sketch, "E902", {"start": v(1.3, -1.86) * mm, "end": v(1.35, -1.85) * mm});
            skLineSegment(sketch, "E903", {"start": v(1.35, -1.85) * mm, "end": v(1.4, -1.84) * mm});
            skLineSegment(sketch, "E904", {"start": v(1.4, -1.84) * mm, "end": v(1.43, -1.84) * mm});
            skLineSegment(sketch, "E905", {"start": v(1.43, -1.84) * mm, "end": v(1.46, -1.84) * mm});
            skLineSegment(sketch, "E906", {"start": v(1.46, -1.84) * mm, "end": v(1.48, -1.86) * mm});
            skLineSegment(sketch, "E907", {"start": v(1.48, -1.86) * mm, "end": v(1.48, -1.89) * mm});
            skLineSegment(sketch, "E908", {"start": v(1.48, -1.89) * mm, "end": v(1.46, -1.92) * mm});
            skLineSegment(sketch, "E909", {"start": v(1.46, -1.92) * mm, "end": v(1.42, -1.97) * mm});
            skLineSegment(sketch, "E910", {"start": v(1.42, -1.97) * mm, "end": v(1.37, -2.02) * mm});
            skLineSegment(sketch, "E911", {"start": v(1.37, -2.02) * mm, "end": v(1.36, -2.03) * mm});
            skLineSegment(sketch, "E912", {"start": v(1.36, -2.03) * mm, "end": v(1.35, -2.05) * mm});
            skLineSegment(sketch, "E913", {"start": v(1.35, -2.05) * mm, "end": v(1.31, -2.08) * mm});
            skLineSegment(sketch, "E914", {"start": v(1.31, -2.08) * mm, "end": v(1.25, -2.13) * mm});
            skLineSegment(sketch, "E915", {"start": v(1.25, -2.13) * mm, "end": v(1.19, -2.14) * mm});
            skLineSegment(sketch, "E916", {"start": v(1.19, -2.14) * mm, "end": v(1.14, -2.13) * mm});
            skLineSegment(sketch, "E917", {"start": v(1.14, -2.13) * mm, "end": v(1.12, -2.12) * mm});
            skLineSegment(sketch, "E918", {"start": v(0.93, -1.98) * mm, "end": v(0.93, -1.97) * mm});
            skLineSegment(sketch, "E919", {"start": v(0.93, -1.97) * mm, "end": v(0.92, -1.93) * mm});
            skLineSegment(sketch, "E920", {"start": v(0.92, -1.93) * mm, "end": v(0.93, -1.87) * mm});
            skLineSegment(sketch, "E921", {"start": v(0.93, -1.87) * mm, "end": v(0.94, -1.83) * mm});
            skLineSegment(sketch, "E922", {"start": v(0.94, -1.83) * mm, "end": v(0.96, -1.78) * mm});
            skLineSegment(sketch, "E923", {"start": v(0.96, -1.78) * mm, "end": v(0.99, -1.74) * mm});
            skLineSegment(sketch, "E924", {"start": v(0.99, -1.74) * mm, "end": v(1.02, -1.71) * mm});
            skLineSegment(sketch, "E925", {"start": v(1.02, -1.71) * mm, "end": v(1.04, -1.69) * mm});
            skLineSegment(sketch, "E926", {"start": v(1.04, -1.69) * mm, "end": v(1.07, -1.67) * mm});
            skLineSegment(sketch, "E927", {"start": v(1.07, -1.67) * mm, "end": v(1.1, -1.66) * mm});
            skLineSegment(sketch, "E928", {"start": v(1.1, -1.66) * mm, "end": v(1.12, -1.66) * mm});
            skLineSegment(sketch, "E929", {"start": v(1.12, -1.66) * mm, "end": v(1.14, -1.67) * mm});
            skLineSegment(sketch, "E930", {"start": v(1.14, -1.67) * mm, "end": v(1.15, -1.7) * mm});
            skLineSegment(sketch, "E931", {"start": v(1.15, -1.7) * mm, "end": v(1.15, -1.73) * mm});
            skLineSegment(sketch, "E932", {"start": v(1.15, -1.73) * mm, "end": v(1.13, -1.77) * mm});
            skLineSegment(sketch, "E933", {"start": v(1.13, -1.77) * mm, "end": v(1.11, -1.83) * mm});
            skLineSegment(sketch, "E934", {"start": v(1.11, -1.83) * mm, "end": v(1.08, -1.88) * mm});
            skLineSegment(sketch, "E935", {"start": v(1.08, -1.88) * mm, "end": v(1.07, -1.9) * mm});
            skLineSegment(sketch, "E936", {"start": v(1.07, -1.9) * mm, "end": v(1.07, -1.9) * mm});
            skLineSegment(sketch, "E937", {"start": v(1.07, -1.9) * mm, "end": v(1.06, -1.92) * mm});
            skLineSegment(sketch, "E938", {"start": v(1.06, -1.92) * mm, "end": v(1.05, -1.94) * mm});
            skLineSegment(sketch, "E939", {"start": v(1.05, -1.94) * mm, "end": v(1.04, -1.96) * mm});
            skLineSegment(sketch, "E940", {"start": v(1.04, -1.96) * mm, "end": v(1.02, -1.98) * mm});
            skLineSegment(sketch, "E941", {"start": v(1.02, -1.98) * mm, "end": v(1, -1.99) * mm});
            skLineSegment(sketch, "E942", {"start": v(1, -1.99) * mm, "end": v(0.98, -2) * mm});
            skLineSegment(sketch, "E943", {"start": v(0.98, -2) * mm, "end": v(0.95, -2) * mm});
            skLineSegment(sketch, "E944", {"start": v(0.95, -2) * mm, "end": v(0.93, -1.99) * mm});
            skLineSegment(sketch, "E945", {"start": v(0.93, -1.99) * mm, "end": v(0.93, -1.98) * mm});
            skLineSegment(sketch, "E946", {"start": v(1.13, -1.95) * mm, "end": v(1.13, -1.94) * mm});
            skLineSegment(sketch, "E947", {"start": v(1.13, -1.94) * mm, "end": v(1.12, -1.9) * mm});
            skLineSegment(sketch, "E948", {"start": v(1.12, -1.9) * mm, "end": v(1.13, -1.85) * mm});
            skLineSegment(sketch, "E949", {"start": v(1.13, -1.85) * mm, "end": v(1.15, -1.8) * mm});
            skLineSegment(sketch, "E950", {"start": v(1.15, -1.8) * mm, "end": v(1.17, -1.73) * mm});
            skLineSegment(sketch, "E951", {"start": v(1.17, -1.73) * mm, "end": v(1.2, -1.68) * mm});
            skLineSegment(sketch, "E952", {"start": v(1.2, -1.68) * mm, "end": v(1.24, -1.62) * mm});
            skLineSegment(sketch, "E953", {"start": v(1.24, -1.62) * mm, "end": v(1.28, -1.57) * mm});
            skLineSegment(sketch, "E954", {"start": v(1.28, -1.57) * mm, "end": v(1.31, -1.52) * mm});
            skLineSegment(sketch, "E955", {"start": v(1.31, -1.52) * mm, "end": v(1.35, -1.48) * mm});
            skLineSegment(sketch, "E956", {"start": v(1.35, -1.48) * mm, "end": v(1.38, -1.46) * mm});
            skLineSegment(sketch, "E957", {"start": v(1.38, -1.46) * mm, "end": v(1.4, -1.44) * mm});
            skLineSegment(sketch, "E958", {"start": v(1.4, -1.44) * mm, "end": v(1.43, -1.44) * mm});
            skLineSegment(sketch, "E959", {"start": v(1.43, -1.44) * mm, "end": v(1.43, -1.46) * mm});
            skLineSegment(sketch, "E960", {"start": v(1.43, -1.46) * mm, "end": v(1.43, -1.5) * mm});
            skLineSegment(sketch, "E961", {"start": v(1.43, -1.5) * mm, "end": v(1.4, -1.56) * mm});
            skLineSegment(sketch, "E962", {"start": v(1.4, -1.56) * mm, "end": v(1.38, -1.63) * mm});
            skLineSegment(sketch, "E963", {"start": v(1.38, -1.63) * mm, "end": v(1.37, -1.65) * mm});
            skLineSegment(sketch, "E964", {"start": v(1.37, -1.65) * mm, "end": v(1.36, -1.66) * mm});
            skLineSegment(sketch, "E965", {"start": v(1.36, -1.66) * mm, "end": v(1.35, -1.69) * mm});
            skLineSegment(sketch, "E966", {"start": v(1.35, -1.69) * mm, "end": v(1.33, -1.74) * mm});
            skLineSegment(sketch, "E967", {"start": v(1.33, -1.74) * mm, "end": v(1.3, -1.79) * mm});
            skLineSegment(sketch, "E968", {"start": v(1.3, -1.79) * mm, "end": v(1.29, -1.84) * mm});
            skLineSegment(sketch, "E969", {"start": v(1.29, -1.84) * mm, "end": v(1.26, -1.88) * mm});
            skLineSegment(sketch, "E970", {"start": v(1.26, -1.88) * mm, "end": v(1.23, -1.92) * mm});
            skLineSegment(sketch, "E971", {"start": v(1.23, -1.92) * mm, "end": v(1.18, -1.94) * mm});
            skLineSegment(sketch, "E972", {"start": v(1.18, -1.94) * mm, "end": v(1.14, -1.95) * mm});
            skLineSegment(sketch, "E973", {"start": v(1.14, -1.95) * mm, "end": v(1.13, -1.95) * mm});
            skLineSegment(sketch, "E974", {"start": v(0.78, -1.85) * mm, "end": v(0.78, -1.84) * mm});
            skLineSegment(sketch, "E975", {"start": v(0.78, -1.84) * mm, "end": v(0.78, -1.8) * mm});
            skLineSegment(sketch, "E976", {"start": v(0.78, -1.8) * mm, "end": v(0.79, -1.75) * mm});
            skLineSegment(sketch, "E977", {"start": v(0.79, -1.75) * mm, "end": v(0.8, -1.7) * mm});
            skLineSegment(sketch, "E978", {"start": v(0.8, -1.7) * mm, "end": v(0.83, -1.66) * mm});
            skLineSegment(sketch, "E979", {"start": v(0.83, -1.66) * mm, "end": v(0.85, -1.62) * mm});
            skLineSegment(sketch, "E980", {"start": v(0.85, -1.62) * mm, "end": v(0.88, -1.58) * mm});
            skLineSegment(sketch, "E981", {"start": v(0.88, -1.58) * mm, "end": v(0.92, -1.55) * mm});
            skLineSegment(sketch, "E982", {"start": v(0.92, -1.55) * mm, "end": v(0.95, -1.53) * mm});
            skLineSegment(sketch, "E983", {"start": v(0.95, -1.53) * mm, "end": v(0.97, -1.52) * mm});
            skLineSegment(sketch, "E984", {"start": v(0.97, -1.52) * mm, "end": v(1, -1.51) * mm});
            skLineSegment(sketch, "E985", {"start": v(1, -1.51) * mm, "end": v(1.01, -1.52) * mm});
            skLineSegment(sketch, "E986", {"start": v(1.01, -1.52) * mm, "end": v(1.02, -1.54) * mm});
            skLineSegment(sketch, "E987", {"start": v(1.02, -1.54) * mm, "end": v(1.02, -1.56) * mm});
            skLineSegment(sketch, "E988", {"start": v(1.02, -1.56) * mm, "end": v(1.01, -1.6) * mm});
            skLineSegment(sketch, "E989", {"start": v(1.01, -1.6) * mm, "end": v(0.99, -1.66) * mm});
            skLineSegment(sketch, "E990", {"start": v(0.99, -1.66) * mm, "end": v(0.96, -1.71) * mm});
            skLineSegment(sketch, "E991", {"start": v(0.96, -1.71) * mm, "end": v(0.95, -1.73) * mm});
            skLineSegment(sketch, "E992", {"start": v(0.95, -1.73) * mm, "end": v(0.95, -1.74) * mm});
            skLineSegment(sketch, "E993", {"start": v(0.95, -1.74) * mm, "end": v(0.94, -1.75) * mm});
            skLineSegment(sketch, "E994", {"start": v(0.94, -1.75) * mm, "end": v(0.92, -1.78) * mm});
            skLineSegment(sketch, "E995", {"start": v(0.92, -1.78) * mm, "end": v(0.9, -1.81) * mm});
            skLineSegment(sketch, "E996", {"start": v(0.9, -1.81) * mm, "end": v(0.88, -1.84) * mm});
            skLineSegment(sketch, "E997", {"start": v(0.88, -1.84) * mm, "end": v(0.86, -1.86) * mm});
            skLineSegment(sketch, "E998", {"start": v(0.86, -1.86) * mm, "end": v(0.84, -1.87) * mm});
            skLineSegment(sketch, "E999", {"start": v(0.84, -1.87) * mm, "end": v(0.8, -1.87) * mm});
            skLineSegment(sketch, "E1000", {"start": v(0.8, -1.87) * mm, "end": v(0.79, -1.86) * mm});
            skLineSegment(sketch, "E1001", {"start": v(0.79, -1.86) * mm, "end": v(0.78, -1.85) * mm});
            skLineSegment(sketch, "E1002", {"start": v(0.6, -1.67) * mm, "end": v(0.6, -1.66) * mm});
            skLineSegment(sketch, "E1003", {"start": v(0.6, -1.66) * mm, "end": v(0.6, -1.62) * mm});
            skLineSegment(sketch, "E1004", {"start": v(0.6, -1.62) * mm, "end": v(0.6, -1.58) * mm});
            skLineSegment(sketch, "E1005", {"start": v(0.6, -1.58) * mm, "end": v(0.62, -1.54) * mm});
            skLineSegment(sketch, "E1006", {"start": v(0.62, -1.54) * mm, "end": v(0.64, -1.5) * mm});
            skLineSegment(sketch, "E1007", {"start": v(0.64, -1.5) * mm, "end": v(0.66, -1.47) * mm});
            skLineSegment(sketch, "E1008", {"start": v(0.66, -1.47) * mm, "end": v(0.7, -1.44) * mm});
            skLineSegment(sketch, "E1009", {"start": v(0.7, -1.44) * mm, "end": v(0.72, -1.41) * mm});
            skLineSegment(sketch, "E1010", {"start": v(0.72, -1.41) * mm, "end": v(0.75, -1.4) * mm});
            skLineSegment(sketch, "E1011", {"start": v(0.75, -1.4) * mm, "end": v(0.78, -1.38) * mm});
            skLineSegment(sketch, "E1012", {"start": v(0.78, -1.38) * mm, "end": v(0.8, -1.38) * mm});
            skLineSegment(sketch, "E1013", {"start": v(0.8, -1.38) * mm, "end": v(0.82, -1.39) * mm});
            skLineSegment(sketch, "E1014", {"start": v(0.82, -1.39) * mm, "end": v(0.83, -1.4) * mm});
            skLineSegment(sketch, "E1015", {"start": v(0.83, -1.4) * mm, "end": v(0.83, -1.43) * mm});
            skLineSegment(sketch, "E1016", {"start": v(0.83, -1.43) * mm, "end": v(0.82, -1.46) * mm});
            skLineSegment(sketch, "E1017", {"start": v(0.82, -1.46) * mm, "end": v(0.79, -1.51) * mm});
            skLineSegment(sketch, "E1018", {"start": v(0.79, -1.51) * mm, "end": v(0.76, -1.56) * mm});
            skLineSegment(sketch, "E1019", {"start": v(0.76, -1.56) * mm, "end": v(0.75, -1.57) * mm});
            skLineSegment(sketch, "E1020", {"start": v(0.75, -1.57) * mm, "end": v(0.75, -1.58) * mm});
            skLineSegment(sketch, "E1021", {"start": v(0.75, -1.58) * mm, "end": v(0.74, -1.6) * mm});
            skLineSegment(sketch, "E1022", {"start": v(0.74, -1.6) * mm, "end": v(0.73, -1.62) * mm});
            skLineSegment(sketch, "E1023", {"start": v(0.73, -1.62) * mm, "end": v(0.71, -1.64) * mm});
            skLineSegment(sketch, "E1024", {"start": v(0.71, -1.64) * mm, "end": v(0.7, -1.66) * mm});
            skLineSegment(sketch, "E1025", {"start": v(0.7, -1.66) * mm, "end": v(0.68, -1.68) * mm});
            skLineSegment(sketch, "E1026", {"start": v(0.68, -1.68) * mm, "end": v(0.66, -1.7) * mm});
            skLineSegment(sketch, "E1027", {"start": v(0.66, -1.7) * mm, "end": v(0.63, -1.69) * mm});
            skLineSegment(sketch, "E1028", {"start": v(0.63, -1.69) * mm, "end": v(0.61, -1.68) * mm});
            skLineSegment(sketch, "E1029", {"start": v(0.61, -1.68) * mm, "end": v(0.6, -1.67) * mm});
            skLineSegment(sketch, "E1030", {"start": v(0.44, -1.52) * mm, "end": v(0.44, -1.5) * mm});
            skLineSegment(sketch, "E1031", {"start": v(0.44, -1.5) * mm, "end": v(0.46, -1.45) * mm});
            skLineSegment(sketch, "E1032", {"start": v(0.46, -1.45) * mm, "end": v(0.48, -1.4) * mm});
            skLineSegment(sketch, "E1033", {"start": v(0.48, -1.4) * mm, "end": v(0.51, -1.36) * mm});
            skLineSegment(sketch, "E1034", {"start": v(0.51, -1.36) * mm, "end": v(0.54, -1.33) * mm});
            skLineSegment(sketch, "E1035", {"start": v(0.54, -1.33) * mm, "end": v(0.57, -1.31) * mm});
            skLineSegment(sketch, "E1036", {"start": v(0.57, -1.31) * mm, "end": v(0.6, -1.3) * mm});
            skLineSegment(sketch, "E1037", {"start": v(0.6, -1.3) * mm, "end": v(0.62, -1.3) * mm});
            skLineSegment(sketch, "E1038", {"start": v(0.62, -1.3) * mm, "end": v(0.64, -1.3) * mm});
            skLineSegment(sketch, "E1039", {"start": v(0.64, -1.3) * mm, "end": v(0.65, -1.32) * mm});
            skLineSegment(sketch, "E1040", {"start": v(0.65, -1.32) * mm, "end": v(0.66, -1.34) * mm});
            skLineSegment(sketch, "E1041", {"start": v(0.66, -1.34) * mm, "end": v(0.66, -1.36) * mm});
            skLineSegment(sketch, "E1042", {"start": v(0.66, -1.36) * mm, "end": v(0.65, -1.4) * mm});
            skLineSegment(sketch, "E1043", {"start": v(0.65, -1.4) * mm, "end": v(0.63, -1.42) * mm});
            skLineSegment(sketch, "E1044", {"start": v(0.63, -1.42) * mm, "end": v(0.6, -1.46) * mm});
            skLineSegment(sketch, "E1045", {"start": v(0.6, -1.46) * mm, "end": v(0.55, -1.5) * mm});
            skLineSegment(sketch, "E1046", {"start": v(0.55, -1.5) * mm, "end": v(0.5, -1.52) * mm});
            skLineSegment(sketch, "E1047", {"start": v(0.5, -1.52) * mm, "end": v(0.48, -1.53) * mm});
            skLineSegment(sketch, "E1048", {"start": v(0.48, -1.53) * mm, "end": v(0.44, -1.52) * mm});
            skLineSegment(sketch, "E1049", {"start": v(0.32, -1.41) * mm, "end": v(0.3, -1.4) * mm});
            skLineSegment(sketch, "E1050", {"start": v(0.3, -1.4) * mm, "end": v(0.3, -1.36) * mm});
            skLineSegment(sketch, "E1051", {"start": v(0.3, -1.36) * mm, "end": v(0.3, -1.31) * mm});
            skLineSegment(sketch, "E1052", {"start": v(0.3, -1.31) * mm, "end": v(0.3, -1.27) * mm});
            skLineSegment(sketch, "E1053", {"start": v(0.3, -1.27) * mm, "end": v(0.32, -1.23) * mm});
            skLineSegment(sketch, "E1054", {"start": v(0.32, -1.23) * mm, "end": v(0.35, -1.2) * mm});
            skLineSegment(sketch, "E1055", {"start": v(0.35, -1.2) * mm, "end": v(0.4, -1.16) * mm});
            skLineSegment(sketch, "E1056", {"start": v(0.4, -1.16) * mm, "end": v(0.43, -1.14) * mm});
            skLineSegment(sketch, "E1057", {"start": v(0.43, -1.14) * mm, "end": v(0.47, -1.12) * mm});
            skLineSegment(sketch, "E1058", {"start": v(0.47, -1.12) * mm, "end": v(0.5, -1.12) * mm});
            skLineSegment(sketch, "E1059", {"start": v(0.5, -1.12) * mm, "end": v(0.54, -1.11) * mm});
            skLineSegment(sketch, "E1060", {"start": v(0.54, -1.11) * mm, "end": v(0.56, -1.12) * mm});
            skLineSegment(sketch, "E1061", {"start": v(0.56, -1.12) * mm, "end": v(0.57, -1.14) * mm});
            skLineSegment(sketch, "E1062", {"start": v(0.57, -1.14) * mm, "end": v(0.57, -1.17) * mm});
            skLineSegment(sketch, "E1063", {"start": v(0.57, -1.17) * mm, "end": v(0.55, -1.2) * mm});
            skLineSegment(sketch, "E1064", {"start": v(0.55, -1.2) * mm, "end": v(0.51, -1.26) * mm});
            skLineSegment(sketch, "E1065", {"start": v(0.51, -1.26) * mm, "end": v(0.46, -1.3) * mm});
            skLineSegment(sketch, "E1066", {"start": v(0.46, -1.3) * mm, "end": v(0.45, -1.32) * mm});
            skLineSegment(sketch, "E1067", {"start": v(0.45, -1.32) * mm, "end": v(0.44, -1.32) * mm});
            skLineSegment(sketch, "E1068", {"start": v(0.44, -1.32) * mm, "end": v(0.44, -1.33) * mm});
            skLineSegment(sketch, "E1069", {"start": v(0.44, -1.33) * mm, "end": v(0.42, -1.35) * mm});
            skLineSegment(sketch, "E1070", {"start": v(0.42, -1.35) * mm, "end": v(0.41, -1.38) * mm});
            skLineSegment(sketch, "E1071", {"start": v(0.41, -1.38) * mm, "end": v(0.4, -1.4) * mm});
            skLineSegment(sketch, "E1072", {"start": v(0.4, -1.4) * mm, "end": v(0.38, -1.42) * mm});
            skLineSegment(sketch, "E1073", {"start": v(0.38, -1.42) * mm, "end": v(0.36, -1.43) * mm});
            skLineSegment(sketch, "E1074", {"start": v(0.36, -1.43) * mm, "end": v(0.34, -1.43) * mm});
            skLineSegment(sketch, "E1075", {"start": v(0.34, -1.43) * mm, "end": v(0.32, -1.42) * mm});
            skLineSegment(sketch, "E1076", {"start": v(0.32, -1.42) * mm, "end": v(0.32, -1.41) * mm});
            skLineSegment(sketch, "E1077", {"start": v(0.16, -1.2) * mm, "end": v(0.16, -1.18) * mm});
            skLineSegment(sketch, "E1078", {"start": v(0.16, -1.18) * mm, "end": v(0.16, -1.14) * mm});
            skLineSegment(sketch, "E1079", {"start": v(0.16, -1.14) * mm, "end": v(0.17, -1.1) * mm});
            skLineSegment(sketch, "E1080", {"start": v(0.17, -1.1) * mm, "end": v(0.19, -1.07) * mm});
            skLineSegment(sketch, "E1081", {"start": v(0.19, -1.07) * mm, "end": v(0.21, -1.05) * mm});
            skLineSegment(sketch, "E1082", {"start": v(0.21, -1.05) * mm, "end": v(0.24, -1.03) * mm});
            skLineSegment(sketch, "E1083", {"start": v(0.24, -1.03) * mm, "end": v(0.27, -1.02) * mm});
            skLineSegment(sketch, "E1084", {"start": v(0.27, -1.02) * mm, "end": v(0.3, -1.02) * mm});
            skLineSegment(sketch, "E1085", {"start": v(0.3, -1.02) * mm, "end": v(0.32, -1.02) * mm});
            skLineSegment(sketch, "E1086", {"start": v(0.32, -1.02) * mm, "end": v(0.34, -1.03) * mm});
            skLineSegment(sketch, "E1087", {"start": v(0.34, -1.03) * mm, "end": v(0.36, -1.04) * mm});
            skLineSegment(sketch, "E1088", {"start": v(0.36, -1.04) * mm, "end": v(0.37, -1.06) * mm});
            skLineSegment(sketch, "E1089", {"start": v(0.37, -1.06) * mm, "end": v(0.36, -1.09) * mm});
            skLineSegment(sketch, "E1090", {"start": v(0.36, -1.09) * mm, "end": v(0.35, -1.12) * mm});
            skLineSegment(sketch, "E1091", {"start": v(0.35, -1.12) * mm, "end": v(0.33, -1.15) * mm});
            skLineSegment(sketch, "E1092", {"start": v(0.33, -1.15) * mm, "end": v(0.29, -1.19) * mm});
            skLineSegment(sketch, "E1093", {"start": v(0.29, -1.19) * mm, "end": v(0.24, -1.22) * mm});
            skLineSegment(sketch, "E1094", {"start": v(0.24, -1.22) * mm, "end": v(0.23, -1.23) * mm});
            skLineSegment(sketch, "E1095", {"start": v(0.23, -1.23) * mm, "end": v(0.2, -1.23) * mm});
            skLineSegment(sketch, "E1096", {"start": v(0.2, -1.23) * mm, "end": v(0.16, -1.2) * mm});
            skLineSegment(sketch, "E1097", {"start": v(0.07, -1.07) * mm, "end": v(0.07, -1.05) * mm});
            skLineSegment(sketch, "E1098", {"start": v(0.07, -1.05) * mm, "end": v(0.08, -1) * mm});
            skLineSegment(sketch, "E1099", {"start": v(0.08, -1) * mm, "end": v(0.1, -0.95) * mm});
            skLineSegment(sketch, "E1100", {"start": v(0.1, -0.95) * mm, "end": v(0.12, -0.91) * mm});
            skLineSegment(sketch, "E1101", {"start": v(0.12, -0.91) * mm, "end": v(0.15, -0.89) * mm});
            skLineSegment(sketch, "E1102", {"start": v(0.15, -0.89) * mm, "end": v(0.18, -0.87) * mm});
            skLineSegment(sketch, "E1103", {"start": v(0.18, -0.87) * mm, "end": v(0.2, -0.87) * mm});
            skLineSegment(sketch, "E1104", {"start": v(0.2, -0.87) * mm, "end": v(0.23, -0.88) * mm});
            skLineSegment(sketch, "E1105", {"start": v(0.23, -0.88) * mm, "end": v(0.25, -0.89) * mm});
            skLineSegment(sketch, "E1106", {"start": v(0.25, -0.89) * mm, "end": v(0.27, -0.9) * mm});
            skLineSegment(sketch, "E1107", {"start": v(0.27, -0.9) * mm, "end": v(0.28, -0.93) * mm});
            skLineSegment(sketch, "E1108", {"start": v(0.28, -0.93) * mm, "end": v(0.28, -0.95) * mm});
            skLineSegment(sketch, "E1109", {"start": v(0.28, -0.95) * mm, "end": v(0.27, -0.98) * mm});
            skLineSegment(sketch, "E1110", {"start": v(0.27, -0.98) * mm, "end": v(0.24, -1) * mm});
            skLineSegment(sketch, "E1111", {"start": v(0.24, -1) * mm, "end": v(0.2, -1.03) * mm});
            skLineSegment(sketch, "E1112", {"start": v(0.2, -1.03) * mm, "end": v(0.15, -1.05) * mm});
            skLineSegment(sketch, "E1113", {"start": v(0.15, -1.05) * mm, "end": v(0.1, -1.06) * mm});
            skLineSegment(sketch, "E1114", {"start": v(0.1, -1.06) * mm, "end": v(0.07, -1.07) * mm});
            skLineSegment(sketch, "E1115", {"start": v(2.9, -1.06) * mm, "end": v(2.9, -1.05) * mm});
            skLineSegment(sketch, "E1116", {"start": v(2.9, -1.05) * mm, "end": v(2.9, -1.02) * mm});
            skLineSegment(sketch, "E1117", {"start": v(2.9, -1.02) * mm, "end": v(2.93, -0.99) * mm});
            skLineSegment(sketch, "E1118", {"start": v(2.93, -0.99) * mm, "end": v(2.96, -0.95) * mm});
            skLineSegment(sketch, "E1119", {"start": v(2.96, -0.95) * mm, "end": v(3, -0.93) * mm});
            skLineSegment(sketch, "E1120", {"start": v(3, -0.93) * mm, "end": v(3.03, -0.9) * mm});
            skLineSegment(sketch, "E1121", {"start": v(3.03, -0.9) * mm, "end": v(3.07, -0.88) * mm});
            skLineSegment(sketch, "E1122", {"start": v(3.07, -0.88) * mm, "end": v(3.1, -0.87) * mm});
            skLineSegment(sketch, "E1123", {"start": v(3.1, -0.87) * mm, "end": v(3.14, -0.86) * mm});
            skLineSegment(sketch, "E1124", {"start": v(3.14, -0.86) * mm, "end": v(3.17, -0.86) * mm});
            skLineSegment(sketch, "E1125", {"start": v(3.17, -0.86) * mm, "end": v(3.2, -0.86) * mm});
            skLineSegment(sketch, "E1126", {"start": v(3.2, -0.86) * mm, "end": v(3.2, -0.87) * mm});
            skLineSegment(sketch, "E1127", {"start": v(3.2, -0.87) * mm, "end": v(3.21, -0.88) * mm});
            skLineSegment(sketch, "E1128", {"start": v(3.21, -0.88) * mm, "end": v(3.2, -0.9) * mm});
            skLineSegment(sketch, "E1129", {"start": v(3.2, -0.9) * mm, "end": v(3.18, -0.93) * mm});
            skLineSegment(sketch, "E1130", {"start": v(3.18, -0.93) * mm, "end": v(3.15, -0.97) * mm});
            skLineSegment(sketch, "E1131", {"start": v(3.15, -0.97) * mm, "end": v(3.1, -1) * mm});
            skLineSegment(sketch, "E1132", {"start": v(3.1, -1) * mm, "end": v(3.1, -1) * mm});
            skLineSegment(sketch, "E1133", {"start": v(3.1, -1) * mm, "end": v(3.08, -1.02) * mm});
            skLineSegment(sketch, "E1134", {"start": v(3.08, -1.02) * mm, "end": v(3.05, -1.03) * mm});
            skLineSegment(sketch, "E1135", {"start": v(3.05, -1.03) * mm, "end": v(3, -1.06) * mm});
            skLineSegment(sketch, "E1136", {"start": v(3, -1.06) * mm, "end": v(2.94, -1.07) * mm});
            skLineSegment(sketch, "E1137", {"start": v(2.94, -1.07) * mm, "end": v(2.9, -1.07) * mm});
            skLineSegment(sketch, "E1138", {"start": v(2.9, -1.07) * mm, "end": v(2.9, -1.06) * mm});
            skLineSegment(sketch, "E1139", {"start": v(2.46, -0.99) * mm, "end": v(2.46, -0.97) * mm});
            skLineSegment(sketch, "E1140", {"start": v(2.46, -0.97) * mm, "end": v(2.47, -0.93) * mm});
            skLineSegment(sketch, "E1141", {"start": v(2.47, -0.93) * mm, "end": v(2.49, -0.87) * mm});
            skLineSegment(sketch, "E1142", {"start": v(2.49, -0.87) * mm, "end": v(2.52, -0.82) * mm});
            skLineSegment(sketch, "E1143", {"start": v(2.52, -0.82) * mm, "end": v(2.55, -0.77) * mm});
            skLineSegment(sketch, "E1144", {"start": v(2.55, -0.77) * mm, "end": v(2.59, -0.73) * mm});
            skLineSegment(sketch, "E1145", {"start": v(2.59, -0.73) * mm, "end": v(2.63, -0.7) * mm});
            skLineSegment(sketch, "E1146", {"start": v(2.63, -0.7) * mm, "end": v(2.67, -0.67) * mm});
            skLineSegment(sketch, "E1147", {"start": v(2.67, -0.67) * mm, "end": v(2.7, -0.64) * mm});
            skLineSegment(sketch, "E1148", {"start": v(2.7, -0.64) * mm, "end": v(2.74, -0.63) * mm});
            skLineSegment(sketch, "E1149", {"start": v(2.74, -0.63) * mm, "end": v(2.77, -0.62) * mm});
            skLineSegment(sketch, "E1150", {"start": v(2.77, -0.62) * mm, "end": v(2.79, -0.63) * mm});
            skLineSegment(sketch, "E1151", {"start": v(2.79, -0.63) * mm, "end": v(2.8, -0.64) * mm});
            skLineSegment(sketch, "E1152", {"start": v(2.8, -0.64) * mm, "end": v(2.8, -0.67) * mm});
            skLineSegment(sketch, "E1153", {"start": v(2.8, -0.67) * mm, "end": v(2.78, -0.7) * mm});
            skLineSegment(sketch, "E1154", {"start": v(2.78, -0.7) * mm, "end": v(2.75, -0.76) * mm});
            skLineSegment(sketch, "E1155", {"start": v(2.75, -0.76) * mm, "end": v(2.71, -0.81) * mm});
            skLineSegment(sketch, "E1156", {"start": v(2.71, -0.81) * mm, "end": v(2.7, -0.83) * mm});
            skLineSegment(sketch, "E1157", {"start": v(2.7, -0.83) * mm, "end": v(2.7, -0.83) * mm});
            skLineSegment(sketch, "E1158", {"start": v(2.7, -0.83) * mm, "end": v(2.68, -0.84) * mm});
            skLineSegment(sketch, "E1159", {"start": v(2.68, -0.84) * mm, "end": v(2.64, -0.88) * mm});
            skLineSegment(sketch, "E1160", {"start": v(2.64, -0.88) * mm, "end": v(2.59, -0.92) * mm});
            skLineSegment(sketch, "E1161", {"start": v(2.59, -0.92) * mm, "end": v(2.53, -0.97) * mm});
            skLineSegment(sketch, "E1162", {"start": v(2.53, -0.97) * mm, "end": v(2.48, -1) * mm});
            skLineSegment(sketch, "E1163", {"start": v(2.48, -1) * mm, "end": v(2.45, -1.03) * mm});
            skLineSegment(sketch, "E1164", {"start": v(2.45, -1.03) * mm, "end": v(2.44, -1.03) * mm});
            skLineSegment(sketch, "E1165", {"start": v(2.44, -1.03) * mm, "end": v(2.46, -1) * mm});
            skLineSegment(sketch, "E1166", {"start": v(2.46, -1) * mm, "end": v(2.46, -0.99) * mm});
            skLineSegment(sketch, "E1167", {"start": v(2.73, -0.9) * mm, "end": v(2.73, -0.89) * mm});
            skLineSegment(sketch, "E1168", {"start": v(2.73, -0.89) * mm, "end": v(2.73, -0.83) * mm});
            skLineSegment(sketch, "E1169", {"start": v(2.73, -0.83) * mm, "end": v(2.75, -0.77) * mm});
            skLineSegment(sketch, "E1170", {"start": v(2.75, -0.77) * mm, "end": v(2.78, -0.73) * mm});
            skLineSegment(sketch, "E1171", {"start": v(2.78, -0.73) * mm, "end": v(2.81, -0.7) * mm});
            skLineSegment(sketch, "E1172", {"start": v(2.81, -0.7) * mm, "end": v(2.86, -0.68) * mm});
            skLineSegment(sketch, "E1173", {"start": v(2.86, -0.68) * mm, "end": v(2.9, -0.67) * mm});
            skLineSegment(sketch, "E1174", {"start": v(2.9, -0.67) * mm, "end": v(2.95, -0.67) * mm});
            skLineSegment(sketch, "E1175", {"start": v(2.95, -0.67) * mm, "end": v(3, -0.68) * mm});
            skLineSegment(sketch, "E1176", {"start": v(3, -0.68) * mm, "end": v(3.03, -0.7) * mm});
            skLineSegment(sketch, "E1177", {"start": v(3.03, -0.7) * mm, "end": v(3.07, -0.7) * mm});
            skLineSegment(sketch, "E1178", {"start": v(3.07, -0.7) * mm, "end": v(3.09, -0.72) * mm});
            skLineSegment(sketch, "E1179", {"start": v(3.09, -0.72) * mm, "end": v(3.1, -0.74) * mm});
            skLineSegment(sketch, "E1180", {"start": v(3.1, -0.74) * mm, "end": v(3.1, -0.76) * mm});
            skLineSegment(sketch, "E1181", {"start": v(3.1, -0.76) * mm, "end": v(3.07, -0.77) * mm});
            skLineSegment(sketch, "E1182", {"start": v(3.07, -0.77) * mm, "end": v(3.02, -0.78) * mm});
            skLineSegment(sketch, "E1183", {"start": v(3.02, -0.78) * mm, "end": v(2.97, -0.79) * mm});
            skLineSegment(sketch, "E1184", {"start": v(2.97, -0.79) * mm, "end": v(2.96, -0.79) * mm});
            skLineSegment(sketch, "E1185", {"start": v(2.96, -0.79) * mm, "end": v(2.95, -0.79) * mm});
            skLineSegment(sketch, "E1186", {"start": v(2.95, -0.79) * mm, "end": v(2.93, -0.8) * mm});
            skLineSegment(sketch, "E1187", {"start": v(2.93, -0.8) * mm, "end": v(2.89, -0.84) * mm});
            skLineSegment(sketch, "E1188", {"start": v(2.89, -0.84) * mm, "end": v(2.83, -0.89) * mm});
            skLineSegment(sketch, "E1189", {"start": v(2.83, -0.89) * mm, "end": v(2.78, -0.94) * mm});
            skLineSegment(sketch, "E1190", {"start": v(2.78, -0.94) * mm, "end": v(2.73, -0.97) * mm});
            skLineSegment(sketch, "E1191", {"start": v(2.73, -0.97) * mm, "end": v(2.7, -0.98) * mm});
            skLineSegment(sketch, "E1192", {"start": v(2.7, -0.98) * mm, "end": v(2.7, -0.97) * mm});
            skLineSegment(sketch, "E1193", {"start": v(2.7, -0.97) * mm, "end": v(2.72, -0.92) * mm});
            skLineSegment(sketch, "E1194", {"start": v(2.72, -0.92) * mm, "end": v(2.73, -0.9) * mm});
            skLineSegment(sketch, "E1195", {"start": v(2.2, -0.96) * mm, "end": v(2.2, -0.95) * mm});
            skLineSegment(sketch, "E1196", {"start": v(2.2, -0.95) * mm, "end": v(2.22, -0.93) * mm});
            skLineSegment(sketch, "E1197", {"start": v(2.22, -0.93) * mm, "end": v(2.25, -0.9) * mm});
            skLineSegment(sketch, "E1198", {"start": v(2.25, -0.9) * mm, "end": v(2.28, -0.85) * mm});
            skLineSegment(sketch, "E1199", {"start": v(2.28, -0.85) * mm, "end": v(2.32, -0.8) * mm});
            skLineSegment(sketch, "E1200", {"start": v(2.32, -0.8) * mm, "end": v(2.36, -0.77) * mm});
            skLineSegment(sketch, "E1201", {"start": v(2.36, -0.77) * mm, "end": v(2.4, -0.72) * mm});
            skLineSegment(sketch, "E1202", {"start": v(2.4, -0.72) * mm, "end": v(2.44, -0.68) * mm});
            skLineSegment(sketch, "E1203", {"start": v(2.44, -0.68) * mm, "end": v(2.47, -0.65) * mm});
            skLineSegment(sketch, "E1204", {"start": v(2.47, -0.65) * mm, "end": v(2.5, -0.63) * mm});
            skLineSegment(sketch, "E1205", {"start": v(2.5, -0.63) * mm, "end": v(2.53, -0.6) * mm});
            skLineSegment(sketch, "E1206", {"start": v(2.53, -0.6) * mm, "end": v(2.55, -0.6) * mm});
            skLineSegment(sketch, "E1207", {"start": v(2.55, -0.6) * mm, "end": v(2.56, -0.61) * mm});
            skLineSegment(sketch, "E1208", {"start": v(2.56, -0.61) * mm, "end": v(2.57, -0.63) * mm});
            skLineSegment(sketch, "E1209", {"start": v(2.57, -0.63) * mm, "end": v(2.56, -0.67) * mm});
            skLineSegment(sketch, "E1210", {"start": v(2.56, -0.67) * mm, "end": v(2.54, -0.73) * mm});
            skLineSegment(sketch, "E1211", {"start": v(2.54, -0.73) * mm, "end": v(2.51, -0.8) * mm});
            skLineSegment(sketch, "E1212", {"start": v(2.51, -0.8) * mm, "end": v(2.5, -0.81) * mm});
            skLineSegment(sketch, "E1213", {"start": v(2.5, -0.81) * mm, "end": v(2.49, -0.83) * mm});
            skLineSegment(sketch, "E1214", {"start": v(2.49, -0.83) * mm, "end": v(2.44, -0.87) * mm});
            skLineSegment(sketch, "E1215", {"start": v(2.44, -0.87) * mm, "end": v(2.37, -0.92) * mm});
            skLineSegment(sketch, "E1216", {"start": v(2.37, -0.92) * mm, "end": v(2.28, -0.96) * mm});
            skLineSegment(sketch, "E1217", {"start": v(2.28, -0.96) * mm, "end": v(2.22, -0.96) * mm});
            skLineSegment(sketch, "E1218", {"start": v(2.22, -0.96) * mm, "end": v(2.2, -0.96) * mm});
            skLineSegment(sketch, "E1219", {"start": v(0, -0.9) * mm, "end": v(0, -0.89) * mm});
            skLineSegment(sketch, "E1220", {"start": v(0, -0.89) * mm, "end": v(0.02, -0.85) * mm});
            skLineSegment(sketch, "E1221", {"start": v(0.02, -0.85) * mm, "end": v(0.03, -0.82) * mm});
            skLineSegment(sketch, "E1222", {"start": v(0.03, -0.82) * mm, "end": v(0.04, -0.8) * mm});
            skLineSegment(sketch, "E1223", {"start": v(0.04, -0.8) * mm, "end": v(0.06, -0.78) * mm});
            skLineSegment(sketch, "E1224", {"start": v(0.06, -0.78) * mm, "end": v(0.08, -0.77) * mm});
            skLineSegment(sketch, "E1225", {"start": v(0.08, -0.77) * mm, "end": v(0.1, -0.77) * mm});
            skLineSegment(sketch, "E1226", {"start": v(0.1, -0.77) * mm, "end": v(0.12, -0.77) * mm});
            skLineSegment(sketch, "E1227", {"start": v(0.12, -0.77) * mm, "end": v(0.14, -0.78) * mm});
            skLineSegment(sketch, "E1228", {"start": v(0.14, -0.78) * mm, "end": v(0.15, -0.8) * mm});
            skLineSegment(sketch, "E1229", {"start": v(0.15, -0.8) * mm, "end": v(0.15, -0.81) * mm});
            skLineSegment(sketch, "E1230", {"start": v(0.15, -0.81) * mm, "end": v(0.15, -0.83) * mm});
            skLineSegment(sketch, "E1231", {"start": v(0.15, -0.83) * mm, "end": v(0.15, -0.85) * mm});
            skLineSegment(sketch, "E1232", {"start": v(0.15, -0.85) * mm, "end": v(0.13, -0.87) * mm});
            skLineSegment(sketch, "E1233", {"start": v(0.13, -0.87) * mm, "end": v(0.1, -0.88) * mm});
            skLineSegment(sketch, "E1234", {"start": v(0.1, -0.88) * mm, "end": v(0.06, -0.9) * mm});
            skLineSegment(sketch, "E1235", {"start": v(0.06, -0.9) * mm, "end": v(0.02, -0.9) * mm});
            skLineSegment(sketch, "E1236", {"start": v(0.02, -0.9) * mm, "end": v(0, -0.9) * mm});
            skLineSegment(sketch, "E1237", {"start": v(2, -0.88) * mm, "end": v(2.01, -0.87) * mm});
            skLineSegment(sketch, "E1238", {"start": v(2.01, -0.87) * mm, "end": v(2.02, -0.84) * mm});
            skLineSegment(sketch, "E1239", {"start": v(2.02, -0.84) * mm, "end": v(2.04, -0.8) * mm});
            skLineSegment(sketch, "E1240", {"start": v(2.04, -0.8) * mm, "end": v(2.06, -0.76) * mm});
            skLineSegment(sketch, "E1241", {"start": v(2.06, -0.76) * mm, "end": v(2.09, -0.72) * mm});
            skLineSegment(sketch, "E1242", {"start": v(2.09, -0.72) * mm, "end": v(2.12, -0.7) * mm});
            skLineSegment(sketch, "E1243", {"start": v(2.12, -0.7) * mm, "end": v(2.14, -0.67) * mm});
            skLineSegment(sketch, "E1244", {"start": v(2.14, -0.67) * mm, "end": v(2.17, -0.65) * mm});
            skLineSegment(sketch, "E1245", {"start": v(2.17, -0.65) * mm, "end": v(2.2, -0.64) * mm});
            skLineSegment(sketch, "E1246", {"start": v(2.2, -0.64) * mm, "end": v(2.22, -0.64) * mm});
            skLineSegment(sketch, "E1247", {"start": v(2.22, -0.64) * mm, "end": v(2.23, -0.64) * mm});
            skLineSegment(sketch, "E1248", {"start": v(2.23, -0.64) * mm, "end": v(2.24, -0.65) * mm});
            skLineSegment(sketch, "E1249", {"start": v(2.24, -0.65) * mm, "end": v(2.24, -0.66) * mm});
            skLineSegment(sketch, "E1250", {"start": v(2.24, -0.66) * mm, "end": v(2.23, -0.69) * mm});
            skLineSegment(sketch, "E1251", {"start": v(2.23, -0.69) * mm, "end": v(2.21, -0.72) * mm});
            skLineSegment(sketch, "E1252", {"start": v(2.21, -0.72) * mm, "end": v(2.18, -0.76) * mm});
            skLineSegment(sketch, "E1253", {"start": v(2.18, -0.76) * mm, "end": v(2.14, -0.8) * mm});
            skLineSegment(sketch, "E1254", {"start": v(2.14, -0.8) * mm, "end": v(2.13, -0.8) * mm});
            skLineSegment(sketch, "E1255", {"start": v(2.13, -0.8) * mm, "end": v(2.13, -0.8) * mm});
            skLineSegment(sketch, "E1256", {"start": v(2.13, -0.8) * mm, "end": v(2.12, -0.81) * mm});
            skLineSegment(sketch, "E1257", {"start": v(2.12, -0.81) * mm, "end": v(2.1, -0.83) * mm});
            skLineSegment(sketch, "E1258", {"start": v(2.1, -0.83) * mm, "end": v(2.09, -0.84) * mm});
            skLineSegment(sketch, "E1259", {"start": v(2.09, -0.84) * mm, "end": v(2.07, -0.86) * mm});
            skLineSegment(sketch, "E1260", {"start": v(2.07, -0.86) * mm, "end": v(2.05, -0.88) * mm});
            skLineSegment(sketch, "E1261", {"start": v(2.05, -0.88) * mm, "end": v(2.03, -0.9) * mm});
            skLineSegment(sketch, "E1262", {"start": v(2.03, -0.9) * mm, "end": v(2.02, -0.9) * mm});
            skLineSegment(sketch, "E1263", {"start": v(2.02, -0.9) * mm, "end": v(2, -0.89) * mm});
            skLineSegment(sketch, "E1264", {"start": v(2, -0.89) * mm, "end": v(2, -0.88) * mm});
            skLineSegment(sketch, "E1265", {"start": v(1.56, -0.85) * mm, "end": v(1.56, -0.84) * mm});
            skLineSegment(sketch, "E1266", {"start": v(1.56, -0.84) * mm, "end": v(1.57, -0.8) * mm});
            skLineSegment(sketch, "E1267", {"start": v(1.57, -0.8) * mm, "end": v(1.6, -0.75) * mm});
            skLineSegment(sketch, "E1268", {"start": v(1.6, -0.75) * mm, "end": v(1.63, -0.7) * mm});
            skLineSegment(sketch, "E1269", {"start": v(1.63, -0.7) * mm, "end": v(1.67, -0.65) * mm});
            skLineSegment(sketch, "E1270", {"start": v(1.67, -0.65) * mm, "end": v(1.72, -0.6) * mm});
            skLineSegment(sketch, "E1271", {"start": v(1.72, -0.6) * mm, "end": v(1.76, -0.57) * mm});
            skLineSegment(sketch, "E1272", {"start": v(1.76, -0.57) * mm, "end": v(1.8, -0.54) * mm});
            skLineSegment(sketch, "E1273", {"start": v(1.8, -0.54) * mm, "end": v(1.85, -0.52) * mm});
            skLineSegment(sketch, "E1274", {"start": v(1.85, -0.52) * mm, "end": v(1.9, -0.5) * mm});
            skLineSegment(sketch, "E1275", {"start": v(1.9, -0.5) * mm, "end": v(1.92, -0.5) * mm});
            skLineSegment(sketch, "E1276", {"start": v(1.92, -0.5) * mm, "end": v(1.94, -0.5) * mm});
            skLineSegment(sketch, "E1277", {"start": v(1.94, -0.5) * mm, "end": v(1.95, -0.52) * mm});
            skLineSegment(sketch, "E1278", {"start": v(1.95, -0.52) * mm, "end": v(1.95, -0.55) * mm});
            skLineSegment(sketch, "E1279", {"start": v(1.95, -0.55) * mm, "end": v(1.93, -0.59) * mm});
            skLineSegment(sketch, "E1280", {"start": v(1.93, -0.59) * mm, "end": v(1.89, -0.65) * mm});
            skLineSegment(sketch, "E1281", {"start": v(1.89, -0.65) * mm, "end": v(1.85, -0.7) * mm});
            skLineSegment(sketch, "E1282", {"start": v(1.85, -0.7) * mm, "end": v(1.83, -0.72) * mm});
            skLineSegment(sketch, "E1283", {"start": v(1.83, -0.72) * mm, "end": v(1.81, -0.74) * mm});
            skLineSegment(sketch, "E1284", {"start": v(1.81, -0.74) * mm, "end": v(1.7, -0.8) * mm});
            skLineSegment(sketch, "E1285", {"start": v(1.7, -0.8) * mm, "end": v(1.58, -0.85) * mm});
            skLineSegment(sketch, "E1286", {"start": v(1.58, -0.85) * mm, "end": v(1.56, -0.85) * mm});
            skLineSegment(sketch, "E1287", {"start": v(1.82, -0.85) * mm, "end": v(1.82, -0.84) * mm});
            skLineSegment(sketch, "E1288", {"start": v(1.82, -0.84) * mm, "end": v(1.84, -0.8) * mm});
            skLineSegment(sketch, "E1289", {"start": v(1.84, -0.8) * mm, "end": v(1.86, -0.76) * mm});
            skLineSegment(sketch, "E1290", {"start": v(1.86, -0.76) * mm, "end": v(1.9, -0.72) * mm});
            skLineSegment(sketch, "E1291", {"start": v(1.9, -0.72) * mm, "end": v(1.93, -0.67) * mm});
            skLineSegment(sketch, "E1292", {"start": v(1.93, -0.67) * mm, "end": v(1.97, -0.63) * mm});
            skLineSegment(sketch, "E1293", {"start": v(1.97, -0.63) * mm, "end": v(2, -0.6) * mm});
            skLineSegment(sketch, "E1294", {"start": v(2, -0.6) * mm, "end": v(2.04, -0.57) * mm});
            skLineSegment(sketch, "E1295", {"start": v(2.04, -0.57) * mm, "end": v(2.07, -0.55) * mm});
            skLineSegment(sketch, "E1296", {"start": v(2.07, -0.55) * mm, "end": v(2.1, -0.53) * mm});
            skLineSegment(sketch, "E1297", {"start": v(2.1, -0.53) * mm, "end": v(2.13, -0.52) * mm});
            skLineSegment(sketch, "E1298", {"start": v(2.13, -0.52) * mm, "end": v(2.14, -0.52) * mm});
            skLineSegment(sketch, "E1299", {"start": v(2.14, -0.52) * mm, "end": v(2.15, -0.54) * mm});
            skLineSegment(sketch, "E1300", {"start": v(2.15, -0.54) * mm, "end": v(2.14, -0.56) * mm});
            skLineSegment(sketch, "E1301", {"start": v(2.14, -0.56) * mm, "end": v(2.12, -0.6) * mm});
            skLineSegment(sketch, "E1302", {"start": v(2.12, -0.6) * mm, "end": v(2.08, -0.64) * mm});
            skLineSegment(sketch, "E1303", {"start": v(2.08, -0.64) * mm, "end": v(2.04, -0.7) * mm});
            skLineSegment(sketch, "E1304", {"start": v(2.04, -0.7) * mm, "end": v(2.03, -0.7) * mm});
            skLineSegment(sketch, "E1305", {"start": v(2.03, -0.7) * mm, "end": v(2.01, -0.72) * mm});
            skLineSegment(sketch, "E1306", {"start": v(2.01, -0.72) * mm, "end": v(1.93, -0.78) * mm});
            skLineSegment(sketch, "E1307", {"start": v(1.93, -0.78) * mm, "end": v(1.84, -0.84) * mm});
            skLineSegment(sketch, "E1308", {"start": v(1.84, -0.84) * mm, "end": v(1.82, -0.85) * mm});
            skLineSegment(sketch, "E1309", {"start": v(2.26, -0.77) * mm, "end": v(2.26, -0.75) * mm});
            skLineSegment(sketch, "E1310", {"start": v(2.26, -0.75) * mm, "end": v(2.28, -0.69) * mm});
            skLineSegment(sketch, "E1311", {"start": v(2.28, -0.69) * mm, "end": v(2.3, -0.63) * mm});
            skLineSegment(sketch, "E1312", {"start": v(2.3, -0.63) * mm, "end": v(2.32, -0.59) * mm});
            skLineSegment(sketch, "E1313", {"start": v(2.32, -0.59) * mm, "end": v(2.35, -0.56) * mm});
            skLineSegment(sketch, "E1314", {"start": v(2.35, -0.56) * mm, "end": v(2.37, -0.56) * mm});
            skLineSegment(sketch, "E1315", {"start": v(2.37, -0.56) * mm, "end": v(2.39, -0.56) * mm});
            skLineSegment(sketch, "E1316", {"start": v(2.39, -0.56) * mm, "end": v(2.4, -0.57) * mm});
            skLineSegment(sketch, "E1317", {"start": v(2.4, -0.57) * mm, "end": v(2.41, -0.6) * mm});
            skLineSegment(sketch, "E1318", {"start": v(2.41, -0.6) * mm, "end": v(2.42, -0.63) * mm});
            skLineSegment(sketch, "E1319", {"start": v(2.42, -0.63) * mm, "end": v(2.42, -0.66) * mm});
            skLineSegment(sketch, "E1320", {"start": v(2.42, -0.66) * mm, "end": v(2.42, -0.7) * mm});
            skLineSegment(sketch, "E1321", {"start": v(2.42, -0.7) * mm, "end": v(2.4, -0.72) * mm});
            skLineSegment(sketch, "E1322", {"start": v(2.4, -0.72) * mm, "end": v(2.38, -0.76) * mm});
            skLineSegment(sketch, "E1323", {"start": v(2.38, -0.76) * mm, "end": v(2.34, -0.78) * mm});
            skLineSegment(sketch, "E1324", {"start": v(2.34, -0.78) * mm, "end": v(2.3, -0.8) * mm});
            skLineSegment(sketch, "E1325", {"start": v(2.3, -0.8) * mm, "end": v(2.26, -0.8) * mm});
            skLineSegment(sketch, "E1326", {"start": v(2.26, -0.8) * mm, "end": v(2.24, -0.8) * mm});
            skLineSegment(sketch, "E1327", {"start": v(2.24, -0.8) * mm, "end": v(2.26, -0.77) * mm});
            skLineSegment(sketch, "E1328", {"start": v(1.35, -0.78) * mm, "end": v(1.35, -0.77) * mm});
            skLineSegment(sketch, "E1329", {"start": v(1.35, -0.77) * mm, "end": v(1.36, -0.73) * mm});
            skLineSegment(sketch, "E1330", {"start": v(1.36, -0.73) * mm, "end": v(1.39, -0.68) * mm});
            skLineSegment(sketch, "E1331", {"start": v(1.39, -0.68) * mm, "end": v(1.42, -0.64) * mm});
            skLineSegment(sketch, "E1332", {"start": v(1.42, -0.64) * mm, "end": v(1.46, -0.6) * mm});
            skLineSegment(sketch, "E1333", {"start": v(1.46, -0.6) * mm, "end": v(1.5, -0.55) * mm});
            skLineSegment(sketch, "E1334", {"start": v(1.5, -0.55) * mm, "end": v(1.54, -0.51) * mm});
            skLineSegment(sketch, "E1335", {"start": v(1.54, -0.51) * mm, "end": v(1.58, -0.48) * mm});
            skLineSegment(sketch, "E1336", {"start": v(1.58, -0.48) * mm, "end": v(1.62, -0.46) * mm});
            skLineSegment(sketch, "E1337", {"start": v(1.62, -0.46) * mm, "end": v(1.66, -0.44) * mm});
            skLineSegment(sketch, "E1338", {"start": v(1.66, -0.44) * mm, "end": v(1.69, -0.43) * mm});
            skLineSegment(sketch, "E1339", {"start": v(1.69, -0.43) * mm, "end": v(1.7, -0.44) * mm});
            skLineSegment(sketch, "E1340", {"start": v(1.7, -0.44) * mm, "end": v(1.72, -0.45) * mm});
            skLineSegment(sketch, "E1341", {"start": v(1.72, -0.45) * mm, "end": v(1.72, -0.48) * mm});
            skLineSegment(sketch, "E1342", {"start": v(1.72, -0.48) * mm, "end": v(1.7, -0.52) * mm});
            skLineSegment(sketch, "E1343", {"start": v(1.7, -0.52) * mm, "end": v(1.67, -0.58) * mm});
            skLineSegment(sketch, "E1344", {"start": v(1.67, -0.58) * mm, "end": v(1.63, -0.63) * mm});
            skLineSegment(sketch, "E1345", {"start": v(1.63, -0.63) * mm, "end": v(1.61, -0.65) * mm});
            skLineSegment(sketch, "E1346", {"start": v(1.61, -0.65) * mm, "end": v(1.6, -0.67) * mm});
            skLineSegment(sketch, "E1347", {"start": v(1.6, -0.67) * mm, "end": v(1.49, -0.74) * mm});
            skLineSegment(sketch, "E1348", {"start": v(1.49, -0.74) * mm, "end": v(1.37, -0.78) * mm});
            skLineSegment(sketch, "E1349", {"start": v(1.37, -0.78) * mm, "end": v(1.35, -0.78) * mm});
            skLineSegment(sketch, "E1350", {"start": v(-0.06, -0.77) * mm, "end": v(-0.06, -0.76) * mm});
            skLineSegment(sketch, "E1351", {"start": v(-0.06, -0.76) * mm, "end": v(-0.06, -0.72) * mm});
            skLineSegment(sketch, "E1352", {"start": v(-0.06, -0.72) * mm, "end": v(-0.06, -0.69) * mm});
            skLineSegment(sketch, "E1353", {"start": v(-0.06, -0.69) * mm, "end": v(-0.04, -0.66) * mm});
            skLineSegment(sketch, "E1354", {"start": v(-0.04, -0.66) * mm, "end": v(-0.03, -0.64) * mm});
            skLineSegment(sketch, "E1355", {"start": v(-0.03, -0.64) * mm, "end": v(0, -0.63) * mm});
            skLineSegment(sketch, "E1356", {"start": v(0, -0.63) * mm, "end": v(0.02, -0.62) * mm});
            skLineSegment(sketch, "E1357", {"start": v(0.02, -0.62) * mm, "end": v(0.04, -0.62) * mm});
            skLineSegment(sketch, "E1358", {"start": v(0.04, -0.62) * mm, "end": v(0.07, -0.63) * mm});
            skLineSegment(sketch, "E1359", {"start": v(0.07, -0.63) * mm, "end": v(0.08, -0.64) * mm});
            skLineSegment(sketch, "E1360", {"start": v(0.08, -0.64) * mm, "end": v(0.1, -0.65) * mm});
            skLineSegment(sketch, "E1361", {"start": v(0.1, -0.65) * mm, "end": v(0.1, -0.67) * mm});
            skLineSegment(sketch, "E1362", {"start": v(0.1, -0.67) * mm, "end": v(0.1, -0.69) * mm});
            skLineSegment(sketch, "E1363", {"start": v(0.1, -0.69) * mm, "end": v(0.08, -0.7) * mm});
            skLineSegment(sketch, "E1364", {"start": v(0.08, -0.7) * mm, "end": v(0.05, -0.73) * mm});
            skLineSegment(sketch, "E1365", {"start": v(0.05, -0.73) * mm, "end": v(0, -0.75) * mm});
            skLineSegment(sketch, "E1366", {"start": v(0, -0.75) * mm, "end": v(-0.04, -0.76) * mm});
            skLineSegment(sketch, "E1367", {"start": v(-0.04, -0.76) * mm, "end": v(-0.06, -0.77) * mm});
            skLineSegment(sketch, "E1368", {"start": v(1.2, -0.74) * mm, "end": v(1.2, -0.73) * mm});
            skLineSegment(sketch, "E1369", {"start": v(1.2, -0.73) * mm, "end": v(1.2, -0.7) * mm});
            skLineSegment(sketch, "E1370", {"start": v(1.2, -0.7) * mm, "end": v(1.22, -0.64) * mm});
            skLineSegment(sketch, "E1371", {"start": v(1.22, -0.64) * mm, "end": v(1.24, -0.59) * mm});
            skLineSegment(sketch, "E1372", {"start": v(1.24, -0.59) * mm, "end": v(1.27, -0.54) * mm});
            skLineSegment(sketch, "E1373", {"start": v(1.27, -0.54) * mm, "end": v(1.3, -0.5) * mm});
            skLineSegment(sketch, "E1374", {"start": v(1.3, -0.5) * mm, "end": v(1.35, -0.46) * mm});
            skLineSegment(sketch, "E1375", {"start": v(1.35, -0.46) * mm, "end": v(1.39, -0.42) * mm});
            skLineSegment(sketch, "E1376", {"start": v(1.39, -0.42) * mm, "end": v(1.42, -0.4) * mm});
            skLineSegment(sketch, "E1377", {"start": v(1.42, -0.4) * mm, "end": v(1.45, -0.38) * mm});
            skLineSegment(sketch, "E1378", {"start": v(1.45, -0.38) * mm, "end": v(1.48, -0.37) * mm});
            skLineSegment(sketch, "E1379", {"start": v(1.48, -0.37) * mm, "end": v(1.5, -0.37) * mm});
            skLineSegment(sketch, "E1380", {"start": v(1.5, -0.37) * mm, "end": v(1.5, -0.39) * mm});
            skLineSegment(sketch, "E1381", {"start": v(1.5, -0.39) * mm, "end": v(1.5, -0.42) * mm});
            skLineSegment(sketch, "E1382", {"start": v(1.5, -0.42) * mm, "end": v(1.48, -0.46) * mm});
            skLineSegment(sketch, "E1383", {"start": v(1.48, -0.46) * mm, "end": v(1.44, -0.51) * mm});
            skLineSegment(sketch, "E1384", {"start": v(1.44, -0.51) * mm, "end": v(1.4, -0.57) * mm});
            skLineSegment(sketch, "E1385", {"start": v(1.4, -0.57) * mm, "end": v(1.39, -0.58) * mm});
            skLineSegment(sketch, "E1386", {"start": v(1.39, -0.58) * mm, "end": v(1.38, -0.6) * mm});
            skLineSegment(sketch, "E1387", {"start": v(1.38, -0.6) * mm, "end": v(1.34, -0.63) * mm});
            skLineSegment(sketch, "E1388", {"start": v(1.34, -0.63) * mm, "end": v(1.3, -0.67) * mm});
            skLineSegment(sketch, "E1389", {"start": v(1.3, -0.67) * mm, "end": v(1.25, -0.71) * mm});
            skLineSegment(sketch, "E1390", {"start": v(1.25, -0.71) * mm, "end": v(1.2, -0.74) * mm});
            skLineSegment(sketch, "E1391", {"start": v(1.2, -0.74) * mm, "end": v(1.2, -0.74) * mm});
            skLineSegment(sketch, "E1392", {"start": v(1.08, -0.6) * mm, "end": v(1.08, -0.59) * mm});
            skLineSegment(sketch, "E1393", {"start": v(1.08, -0.59) * mm, "end": v(1.08, -0.55) * mm});
            skLineSegment(sketch, "E1394", {"start": v(1.08, -0.55) * mm, "end": v(1.1, -0.5) * mm});
            skLineSegment(sketch, "E1395", {"start": v(1.1, -0.5) * mm, "end": v(1.1, -0.45) * mm});
            skLineSegment(sketch, "E1396", {"start": v(1.1, -0.45) * mm, "end": v(1.13, -0.41) * mm});
            skLineSegment(sketch, "E1397", {"start": v(1.13, -0.41) * mm, "end": v(1.16, -0.37) * mm});
            skLineSegment(sketch, "E1398", {"start": v(1.16, -0.37) * mm, "end": v(1.2, -0.34) * mm});
            skLineSegment(sketch, "E1399", {"start": v(1.2, -0.34) * mm, "end": v(1.23, -0.32) * mm});
            skLineSegment(sketch, "E1400", {"start": v(1.23, -0.32) * mm, "end": v(1.26, -0.3) * mm});
            skLineSegment(sketch, "E1401", {"start": v(1.26, -0.3) * mm, "end": v(1.3, -0.29) * mm});
            skLineSegment(sketch, "E1402", {"start": v(1.3, -0.29) * mm, "end": v(1.32, -0.29) * mm});
            skLineSegment(sketch, "E1403", {"start": v(1.32, -0.29) * mm, "end": v(1.34, -0.3) * mm});
            skLineSegment(sketch, "E1404", {"start": v(1.34, -0.3) * mm, "end": v(1.34, -0.3) * mm});
            skLineSegment(sketch, "E1405", {"start": v(1.34, -0.3) * mm, "end": v(1.34, -0.33) * mm});
            skLineSegment(sketch, "E1406", {"start": v(1.34, -0.33) * mm, "end": v(1.33, -0.37) * mm});
            skLineSegment(sketch, "E1407", {"start": v(1.33, -0.37) * mm, "end": v(1.3, -0.42) * mm});
            skLineSegment(sketch, "E1408", {"start": v(1.3, -0.42) * mm, "end": v(1.26, -0.47) * mm});
            skLineSegment(sketch, "E1409", {"start": v(1.26, -0.47) * mm, "end": v(1.25, -0.48) * mm});
            skLineSegment(sketch, "E1410", {"start": v(1.25, -0.48) * mm, "end": v(1.24, -0.5) * mm});
            skLineSegment(sketch, "E1411", {"start": v(1.24, -0.5) * mm, "end": v(1.17, -0.55) * mm});
            skLineSegment(sketch, "E1412", {"start": v(1.17, -0.55) * mm, "end": v(1.1, -0.6) * mm});
            skLineSegment(sketch, "E1413", {"start": v(1.1, -0.6) * mm, "end": v(1.08, -0.6) * mm});
            skLineSegment(sketch, "E1414", {"start": v(1.02, -0.35) * mm, "end": v(1.04, -0.33) * mm});
            skLineSegment(sketch, "E1415", {"start": v(1.04, -0.33) * mm, "end": v(1.09, -0.27) * mm});
            skLineSegment(sketch, "E1416", {"start": v(1.09, -0.27) * mm, "end": v(1.13, -0.22) * mm});
            skLineSegment(sketch, "E1417", {"start": v(1.13, -0.22) * mm, "end": v(1.16, -0.2) * mm});
            skLineSegment(sketch, "E1418", {"start": v(1.16, -0.2) * mm, "end": v(1.18, -0.2) * mm});
            skLineSegment(sketch, "E1419", {"start": v(1.18, -0.2) * mm, "end": v(1.18, -0.2) * mm});
            skLineSegment(sketch, "E1420", {"start": v(1.18, -0.2) * mm, "end": v(1.18, -0.22) * mm});
            skLineSegment(sketch, "E1421", {"start": v(1.18, -0.22) * mm, "end": v(1.16, -0.25) * mm});
            skLineSegment(sketch, "E1422", {"start": v(1.16, -0.25) * mm, "end": v(1.14, -0.3) * mm});
            skLineSegment(sketch, "E1423", {"start": v(1.14, -0.3) * mm, "end": v(1.12, -0.33) * mm});
            skLineSegment(sketch, "E1424", {"start": v(1.12, -0.33) * mm, "end": v(1.1, -0.37) * mm});
            skLineSegment(sketch, "E1425", {"start": v(1.1, -0.37) * mm, "end": v(1.07, -0.4) * mm});
            skLineSegment(sketch, "E1426", {"start": v(1.07, -0.4) * mm, "end": v(1.05, -0.42) * mm});
            skLineSegment(sketch, "E1427", {"start": v(1.05, -0.42) * mm, "end": v(1.03, -0.43) * mm});
            skLineSegment(sketch, "E1428", {"start": v(1.03, -0.43) * mm, "end": v(1.02, -0.42) * mm});
            skLineSegment(sketch, "E1429", {"start": v(1.02, -0.42) * mm, "end": v(1.01, -0.4) * mm});
            skLineSegment(sketch, "E1430", {"start": v(1.01, -0.4) * mm, "end": v(1.02, -0.36) * mm});
            skLineSegment(sketch, "E1431", {"start": v(1.02, -0.36) * mm, "end": v(1.02, -0.35) * mm});
            skLineSegment(sketch, "E1432", {"start": v(0.92, -0.25) * mm, "end": v(0.93, -0.24) * mm});
            skLineSegment(sketch, "E1433", {"start": v(0.93, -0.24) * mm, "end": v(0.95, -0.2) * mm});
            skLineSegment(sketch, "E1434", {"start": v(0.95, -0.2) * mm, "end": v(0.97, -0.16) * mm});
            skLineSegment(sketch, "E1435", {"start": v(0.97, -0.16) * mm, "end": v(0.99, -0.13) * mm});
            skLineSegment(sketch, "E1436", {"start": v(0.99, -0.13) * mm, "end": v(1, -0.11) * mm});
            skLineSegment(sketch, "E1437", {"start": v(1, -0.11) * mm, "end": v(1.02, -0.1) * mm});
            skLineSegment(sketch, "E1438", {"start": v(1.02, -0.1) * mm, "end": v(1.03, -0.1) * mm});
            skLineSegment(sketch, "E1439", {"start": v(1.03, -0.1) * mm, "end": v(1.04, -0.1) * mm});
            skLineSegment(sketch, "E1440", {"start": v(1.04, -0.1) * mm, "end": v(1.05, -0.12) * mm});
            skLineSegment(sketch, "E1441", {"start": v(1.05, -0.12) * mm, "end": v(1.05, -0.14) * mm});
            skLineSegment(sketch, "E1442", {"start": v(1.05, -0.14) * mm, "end": v(1.05, -0.16) * mm});
            skLineSegment(sketch, "E1443", {"start": v(1.05, -0.16) * mm, "end": v(1.04, -0.18) * mm});
            skLineSegment(sketch, "E1444", {"start": v(1.04, -0.18) * mm, "end": v(1.03, -0.2) * mm});
            skLineSegment(sketch, "E1445", {"start": v(1.03, -0.2) * mm, "end": v(1.01, -0.22) * mm});
            skLineSegment(sketch, "E1446", {"start": v(1.01, -0.22) * mm, "end": v(1, -0.24) * mm});
            skLineSegment(sketch, "E1447", {"start": v(1, -0.24) * mm, "end": v(0.96, -0.25) * mm});
            skLineSegment(sketch, "E1448", {"start": v(0.96, -0.25) * mm, "end": v(0.93, -0.25) * mm});
            skLineSegment(sketch, "E1449", {"start": v(0.93, -0.25) * mm, "end": v(0.92, -0.25) * mm});
            skLineSegment(sketch, "E1450", {"start": v(-4.06, -1.5) * mm, "end": v(-4.06, -1.47) * mm});
            skLineSegment(sketch, "E1451", {"start": v(-4.06, -1.47) * mm, "end": v(-4.05, -1.4) * mm});
            skLineSegment(sketch, "E1452", {"start": v(-4.05, -1.4) * mm, "end": v(-4.04, -1.33) * mm});
            skLineSegment(sketch, "E1453", {"start": v(-4.04, -1.33) * mm, "end": v(-4.05, -1.28) * mm});
            skLineSegment(sketch, "E1454", {"start": v(-4.05, -1.28) * mm, "end": v(-4.06, -1.26) * mm});
            skLineSegment(sketch, "E1455", {"start": v(-4.06, -1.26) * mm, "end": v(-4.07, -1.25) * mm});
            skLineSegment(sketch, "E1456", {"start": v(-4.07, -1.25) * mm, "end": v(-4.09, -1.26) * mm});
            skLineSegment(sketch, "E1457", {"start": v(-4.09, -1.26) * mm, "end": v(-4.1, -1.28) * mm});
            skLineSegment(sketch, "E1458", {"start": v(-4.1, -1.28) * mm, "end": v(-4.12, -1.3) * mm});
            skLineSegment(sketch, "E1459", {"start": v(-4.12, -1.3) * mm, "end": v(-4.14, -1.34) * mm});
            skLineSegment(sketch, "E1460", {"start": v(-4.14, -1.34) * mm, "end": v(-4.15, -1.38) * mm});
            skLineSegment(sketch, "E1461", {"start": v(-4.15, -1.38) * mm, "end": v(-4.15, -1.41) * mm});
            skLineSegment(sketch, "E1462", {"start": v(-4.15, -1.41) * mm, "end": v(-4.16, -1.45) * mm});
            skLineSegment(sketch, "E1463", {"start": v(-4.16, -1.45) * mm, "end": v(-4.15, -1.48) * mm});
            skLineSegment(sketch, "E1464", {"start": v(-4.15, -1.48) * mm, "end": v(-4.13, -1.5) * mm});
            skLineSegment(sketch, "E1465", {"start": v(-4.13, -1.5) * mm, "end": v(-4.1, -1.5) * mm});
            skLineSegment(sketch, "E1466", {"start": v(-4.1, -1.5) * mm, "end": v(-4.07, -1.5) * mm});
            skLineSegment(sketch, "E1467", {"start": v(-4.07, -1.5) * mm, "end": v(-4.06, -1.5) * mm});
            skLineSegment(sketch, "E1468", {"start": v(2.18, 0.34) * mm, "end": v(2.18, 0.36) * mm});
            skLineSegment(sketch, "E1469", {"start": v(2.18, 0.36) * mm, "end": v(2.16, 0.42) * mm});
            skLineSegment(sketch, "E1470", {"start": v(2.16, 0.42) * mm, "end": v(2.13, 0.48) * mm});
            skLineSegment(sketch, "E1471", {"start": v(2.13, 0.48) * mm, "end": v(2.08, 0.51) * mm});
            skLineSegment(sketch, "E1472", {"start": v(2.08, 0.51) * mm, "end": v(2.03, 0.53) * mm});
            skLineSegment(sketch, "E1473", {"start": v(2.03, 0.53) * mm, "end": v(1.97, 0.53) * mm});
            skLineSegment(sketch, "E1474", {"start": v(1.97, 0.53) * mm, "end": v(1.91, 0.52) * mm});
            skLineSegment(sketch, "E1475", {"start": v(1.91, 0.52) * mm, "end": v(1.85, 0.5) * mm});
            skLineSegment(sketch, "E1476", {"start": v(1.85, 0.5) * mm, "end": v(1.8, 0.48) * mm});
            skLineSegment(sketch, "E1477", {"start": v(1.8, 0.48) * mm, "end": v(1.75, 0.44) * mm});
            skLineSegment(sketch, "E1478", {"start": v(1.75, 0.44) * mm, "end": v(1.71, 0.4) * mm});
            skLineSegment(sketch, "E1479", {"start": v(1.71, 0.4) * mm, "end": v(1.7, 0.38) * mm});
            skLineSegment(sketch, "E1480", {"start": v(1.7, 0.38) * mm, "end": v(1.69, 0.35) * mm});
            skLineSegment(sketch, "E1481", {"start": v(1.69, 0.35) * mm, "end": v(1.7, 0.32) * mm});
            skLineSegment(sketch, "E1482", {"start": v(1.7, 0.32) * mm, "end": v(1.75, 0.3) * mm});
            skLineSegment(sketch, "E1483", {"start": v(1.75, 0.3) * mm, "end": v(1.82, 0.3) * mm});
            skLineSegment(sketch, "E1484", {"start": v(1.82, 0.3) * mm, "end": v(1.9, 0.3) * mm});
            skLineSegment(sketch, "E1485", {"start": v(1.9, 0.3) * mm, "end": v(1.93, 0.3) * mm});
            skLineSegment(sketch, "E1486", {"start": v(1.93, 0.3) * mm, "end": v(1.94, 0.31) * mm});
            skLineSegment(sketch, "E1487", {"start": v(1.94, 0.31) * mm, "end": v(2, 0.31) * mm});
            skLineSegment(sketch, "E1488", {"start": v(2, 0.31) * mm, "end": v(2.07, 0.3) * mm});
            skLineSegment(sketch, "E1489", {"start": v(2.07, 0.3) * mm, "end": v(2.13, 0.3) * mm});
            skLineSegment(sketch, "E1490", {"start": v(2.13, 0.3) * mm, "end": v(2.17, 0.33) * mm});
            skLineSegment(sketch, "E1491", {"start": v(2.17, 0.33) * mm, "end": v(2.18, 0.34) * mm});
            skLineSegment(sketch, "E1492", {"start": v(1.3, 0.44) * mm, "end": v(1.33, 0.45) * mm});
            skLineSegment(sketch, "E1493", {"start": v(1.33, 0.45) * mm, "end": v(1.4, 0.5) * mm});
            skLineSegment(sketch, "E1494", {"start": v(1.4, 0.5) * mm, "end": v(1.49, 0.56) * mm});
            skLineSegment(sketch, "E1495", {"start": v(1.49, 0.56) * mm, "end": v(1.54, 0.63) * mm});
            skLineSegment(sketch, "E1496", {"start": v(1.54, 0.63) * mm, "end": v(1.57, 0.7) * mm});
            skLineSegment(sketch, "E1497", {"start": v(1.57, 0.7) * mm, "end": v(1.58, 0.78) * mm});
            skLineSegment(sketch, "E1498", {"start": v(1.58, 0.78) * mm, "end": v(1.57, 0.87) * mm});
            skLineSegment(sketch, "E1499", {"start": v(1.57, 0.87) * mm, "end": v(1.54, 0.95) * mm});
            skLineSegment(sketch, "E1500", {"start": v(1.54, 0.95) * mm, "end": v(1.5, 1.04) * mm});
            skLineSegment(sketch, "E1501", {"start": v(1.5, 1.04) * mm, "end": v(1.45, 1.13) * mm});
            skLineSegment(sketch, "E1502", {"start": v(1.45, 1.13) * mm, "end": v(1.4, 1.21) * mm});
            skLineSegment(sketch, "E1503", {"start": v(1.4, 1.21) * mm, "end": v(1.33, 1.3) * mm});
            skLineSegment(sketch, "E1504", {"start": v(1.33, 1.3) * mm, "end": v(1.26, 1.38) * mm});
            skLineSegment(sketch, "E1505", {"start": v(1.26, 1.38) * mm, "end": v(1.19, 1.45) * mm});
            skLineSegment(sketch, "E1506", {"start": v(1.19, 1.45) * mm, "end": v(1.12, 1.52) * mm});
            skLineSegment(sketch, "E1507", {"start": v(1.12, 1.52) * mm, "end": v(1.05, 1.58) * mm});
            skLineSegment(sketch, "E1508", {"start": v(1.05, 1.58) * mm, "end": v(1, 1.62) * mm});
            skLineSegment(sketch, "E1509", {"start": v(1, 1.62) * mm, "end": v(0.99, 1.64) * mm});
            skLineSegment(sketch, "E1510", {"start": v(0.99, 1.64) * mm, "end": v(0.97, 1.63) * mm});
            skLineSegment(sketch, "E1511", {"start": v(0.97, 1.63) * mm, "end": v(0.91, 1.6) * mm});
            skLineSegment(sketch, "E1512", {"start": v(0.91, 1.6) * mm, "end": v(0.88, 1.52) * mm});
            skLineSegment(sketch, "E1513", {"start": v(0.88, 1.52) * mm, "end": v(0.88, 1.41) * mm});
            skLineSegment(sketch, "E1514", {"start": v(0.88, 1.41) * mm, "end": v(0.9, 1.3) * mm});
            skLineSegment(sketch, "E1515", {"start": v(0.9, 1.3) * mm, "end": v(0.91, 1.16) * mm});
            skLineSegment(sketch, "E1516", {"start": v(0.91, 1.16) * mm, "end": v(0.91, 1.05) * mm});
            skLineSegment(sketch, "E1517", {"start": v(0.91, 1.05) * mm, "end": v(0.88, 0.95) * mm});
            skLineSegment(sketch, "E1518", {"start": v(0.88, 0.95) * mm, "end": v(0.83, 0.89) * mm});
            skLineSegment(sketch, "E1519", {"start": v(0.83, 0.89) * mm, "end": v(0.8, 0.87) * mm});
            skLineSegment(sketch, "E1520", {"start": v(0.8, 0.87) * mm, "end": v(0.81, 0.86) * mm});
            skLineSegment(sketch, "E1521", {"start": v(0.81, 0.86) * mm, "end": v(0.84, 0.8) * mm});
            skLineSegment(sketch, "E1522", {"start": v(0.84, 0.8) * mm, "end": v(0.88, 0.72) * mm});
            skLineSegment(sketch, "E1523", {"start": v(0.88, 0.72) * mm, "end": v(0.94, 0.65) * mm});
            skLineSegment(sketch, "E1524", {"start": v(0.94, 0.65) * mm, "end": v(1, 0.58) * mm});
            skLineSegment(sketch, "E1525", {"start": v(1, 0.58) * mm, "end": v(1.07, 0.53) * mm});
            skLineSegment(sketch, "E1526", {"start": v(1.07, 0.53) * mm, "end": v(1.14, 0.48) * mm});
            skLineSegment(sketch, "E1527", {"start": v(1.14, 0.48) * mm, "end": v(1.22, 0.45) * mm});
            skLineSegment(sketch, "E1528", {"start": v(1.22, 0.45) * mm, "end": v(1.28, 0.44) * mm});
            skLineSegment(sketch, "E1529", {"start": v(1.28, 0.44) * mm, "end": v(1.3, 0.44) * mm});
            skLineSegment(sketch, "E1530", {"start": v(0.13, 1.03) * mm, "end": v(0.17, 1.05) * mm});
            skLineSegment(sketch, "E1531", {"start": v(0.17, 1.05) * mm, "end": v(0.26, 1.15) * mm});
            skLineSegment(sketch, "E1532", {"start": v(0.26, 1.15) * mm, "end": v(0.35, 1.3) * mm});
            skLineSegment(sketch, "E1533", {"start": v(0.35, 1.3) * mm, "end": v(0.42, 1.48) * mm});
            skLineSegment(sketch, "E1534", {"start": v(0.42, 1.48) * mm, "end": v(0.44, 1.66) * mm});
            skLineSegment(sketch, "E1535", {"start": v(0.44, 1.66) * mm, "end": v(0.43, 1.83) * mm});
            skLineSegment(sketch, "E1536", {"start": v(0.43, 1.83) * mm, "end": v(0.37, 2) * mm});
            skLineSegment(sketch, "E1537", {"start": v(0.37, 2) * mm, "end": v(0.27, 2.12) * mm});
            skLineSegment(sketch, "E1538", {"start": v(0.27, 2.12) * mm, "end": v(0.16, 2.19) * mm});
            skLineSegment(sketch, "E1539", {"start": v(0.16, 2.19) * mm, "end": v(0.12, 2.2) * mm});
            skLineSegment(sketch, "E1540", {"start": v(0.12, 2.2) * mm, "end": v(0.1, 2.2) * mm});
            skLineSegment(sketch, "E1541", {"start": v(0.1, 2.2) * mm, "end": v(0.08, 2.15) * mm});
            skLineSegment(sketch, "E1542", {"start": v(0.08, 2.15) * mm, "end": v(0.05, 2.1) * mm});
            skLineSegment(sketch, "E1543", {"start": v(0.05, 2.1) * mm, "end": v(0.05, 2.04) * mm});
            skLineSegment(sketch, "E1544", {"start": v(0.05, 2.04) * mm, "end": v(0.05, 1.98) * mm});
            skLineSegment(sketch, "E1545", {"start": v(0.05, 1.98) * mm, "end": v(0.06, 1.92) * mm});
            skLineSegment(sketch, "E1546", {"start": v(0.06, 1.92) * mm, "end": v(0.08, 1.85) * mm});
            skLineSegment(sketch, "E1547", {"start": v(0.08, 1.85) * mm, "end": v(0.1, 1.8) * mm});
            skLineSegment(sketch, "E1548", {"start": v(0.1, 1.8) * mm, "end": v(0.11, 1.73) * mm});
            skLineSegment(sketch, "E1549", {"start": v(0.11, 1.73) * mm, "end": v(0.13, 1.66) * mm});
            skLineSegment(sketch, "E1550", {"start": v(0.13, 1.66) * mm, "end": v(0.14, 1.6) * mm});
            skLineSegment(sketch, "E1551", {"start": v(0.14, 1.6) * mm, "end": v(0.14, 1.54) * mm});
            skLineSegment(sketch, "E1552", {"start": v(0.14, 1.54) * mm, "end": v(0.12, 1.49) * mm});
            skLineSegment(sketch, "E1553", {"start": v(0.12, 1.49) * mm, "end": v(0.1, 1.43) * mm});
            skLineSegment(sketch, "E1554", {"start": v(0.1, 1.43) * mm, "end": v(0.05, 1.38) * mm});
            skLineSegment(sketch, "E1555", {"start": v(0.05, 1.38) * mm, "end": v(-0.01, 1.34) * mm});
            skLineSegment(sketch, "E1556", {"start": v(-0.01, 1.34) * mm, "end": v(-0.08, 1.3) * mm});
            skLineSegment(sketch, "E1557", {"start": v(-0.08, 1.3) * mm, "end": v(-0.1, 1.3) * mm});
            skLineSegment(sketch, "E1558", {"start": v(-0.1, 1.3) * mm, "end": v(-0.1, 1.29) * mm});
            skLineSegment(sketch, "E1559", {"start": v(-0.1, 1.29) * mm, "end": v(-0.1, 1.25) * mm});
            skLineSegment(sketch, "E1560", {"start": v(-0.1, 1.25) * mm, "end": v(-0.1, 1.2) * mm});
            skLineSegment(sketch, "E1561", {"start": v(-0.1, 1.2) * mm, "end": v(-0.08, 1.15) * mm});
            skLineSegment(sketch, "E1562", {"start": v(-0.08, 1.15) * mm, "end": v(-0.05, 1.1) * mm});
            skLineSegment(sketch, "E1563", {"start": v(-0.05, 1.1) * mm, "end": v(-0.01, 1.06) * mm});
            skLineSegment(sketch, "E1564", {"start": v(-0.01, 1.06) * mm, "end": v(0.03, 1.03) * mm});
            skLineSegment(sketch, "E1565", {"start": v(0.03, 1.03) * mm, "end": v(0.08, 1.02) * mm});
            skLineSegment(sketch, "E1566", {"start": v(0.08, 1.02) * mm, "end": v(0.12, 1.02) * mm});
            skLineSegment(sketch, "E1567", {"start": v(0.12, 1.02) * mm, "end": v(0.13, 1.03) * mm});
            skSolve(sketch);
        }
        {
            var Q0;
            Q0=qCreatedBy(makeId("Top.planeOp"),FACE);
            var sketch = newSketch(context, id + "F1", { "sketchPlane" : qUnion([Q0])});
            skCircle(sketch, "E1568", {"center": v(0, 0) * mm, "radius": 5.53 * mm});
            skCircle(sketch, "E1569", {"center": v(0, 5.96) * mm, "radius": 0.5 * mm});
            skCircle(sketch, "E1570.0", {"center": v(0, 5.96) * mm, "radius": 1 * mm});
            skSolve(sketch);
        }
        {
            var Q0;
            Q0 = qSketchRegion(id + "F1", true);
            extrude(context, id + "F2", {"entities" : qUnion([Q0]), "oppositeDirection" : true, "depth" : 0.5 * mm});
        }
        {
            var Q0;
            Q0=makeQuery(id+"F0.imprint","IMPRINT",FACE,{"disambiguationData":[TD([[makeQuery(id+"F0.imprint","IMPRINT",EDGE,{"derivedFrom":sQuery(id+"F0.wireOp",EDGE,"E0")}),-1.0]])]});
            extrude(context, id + "F3", {"entities" : qUnion([Q0]), "operationType" : NewBodyOperationType.ADD, "depth" : 0.5 * mm});
        }
        {
            var Q0;
            Q0=makeQuery(id+"F0.imprint","IMPRINT",FACE,{"disambiguationData":[TD([[makeQuery(id+"F0.imprint","IMPRINT",EDGE,{"derivedFrom":sQuery(id+"F0.wireOp",EDGE,"E828")}),-1.0]])]});
            var Q1;
            {var subQ0=sQuery(id+"F0.wireOp",EDGE,"E900");Q1=makeQuery(id+"F0.imprint","IMPRINT",FACE,{"disambiguationData":[TD([[makeQuery(id+"F0.imprint","IMPRINT",EDGE,{"derivedFrom":subQ0}),1.0]])]});}
            var Q2;
            Q2=makeQuery(id+"F0.imprint","IMPRINT",FACE,{"disambiguationData":[TD([[makeQuery(id+"F0.imprint","IMPRINT",EDGE,{"derivedFrom":sQuery(id+"F0.wireOp",EDGE,"E918")}),-1.0]])]});
            var Q3;
            Q3=makeQuery(id+"F0.imprint","IMPRINT",FACE,{"disambiguationData":[TD([[makeQuery(id+"F0.imprint","IMPRINT",EDGE,{"derivedFrom":sQuery(id+"F0.wireOp",EDGE,"E974")}),-1.0]])]});
            var Q4;
            Q4=makeQuery(id+"F0.imprint","IMPRINT",FACE,{"disambiguationData":[TD([[makeQuery(id+"F0.imprint","IMPRINT",EDGE,{"derivedFrom":sQuery(id+"F0.wireOp",EDGE,"E866")}),-1.0]])]});
            var Q5;
            Q5=makeQuery(id+"F0.imprint","IMPRINT",FACE,{"disambiguationData":[TD([[makeQuery(id+"F0.imprint","IMPRINT",EDGE,{"derivedFrom":sQuery(id+"F0.wireOp",EDGE,"E1002")}),-1.0]])]});
            var Q6;
            Q6=makeQuery(id+"F0.imprint","IMPRINT",FACE,{"disambiguationData":[TD([[makeQuery(id+"F0.imprint","IMPRINT",EDGE,{"derivedFrom":sQuery(id+"F0.wireOp",EDGE,"E1030")}),-1.0]])]});
            var Q7;
            Q7=makeQuery(id+"F0.imprint","IMPRINT",FACE,{"disambiguationData":[TD([[makeQuery(id+"F0.imprint","IMPRINT",EDGE,{"derivedFrom":sQuery(id+"F0.wireOp",EDGE,"E1049")}),-1.0]])]});
            var Q8;
            Q8=makeQuery(id+"F0.imprint","IMPRINT",FACE,{"disambiguationData":[TD([[makeQuery(id+"F0.imprint","IMPRINT",EDGE,{"derivedFrom":sQuery(id+"F0.wireOp",EDGE,"E1077")}),-1.0]])]});
            var Q9;
            Q9=makeQuery(id+"F0.imprint","IMPRINT",FACE,{"disambiguationData":[TD([[makeQuery(id+"F0.imprint","IMPRINT",EDGE,{"derivedFrom":sQuery(id+"F0.wireOp",EDGE,"E1097")}),-1.0]])]});
            var Q10;
            Q10=makeQuery(id+"F0.imprint","IMPRINT",FACE,{"disambiguationData":[TD([[makeQuery(id+"F0.imprint","IMPRINT",EDGE,{"derivedFrom":sQuery(id+"F0.wireOp",EDGE,"E1219")}),-1.0]])]});
            var Q11;
            Q11=makeQuery(id+"F0.imprint","IMPRINT",FACE,{"disambiguationData":[TD([[makeQuery(id+"F0.imprint","IMPRINT",EDGE,{"derivedFrom":sQuery(id+"F0.wireOp",EDGE,"E1350")}),-1.0]])]});
            var Q12;
            Q12=makeQuery(id+"F0.imprint","IMPRINT",FACE,{"disambiguationData":[TD([[makeQuery(id+"F0.imprint","IMPRINT",EDGE,{"derivedFrom":sQuery(id+"F0.wireOp",EDGE,"E1115")}),-1.0]])]});
            var Q13;
            Q13=makeQuery(id+"F0.imprint","IMPRINT",FACE,{"disambiguationData":[TD([[makeQuery(id+"F0.imprint","IMPRINT",EDGE,{"derivedFrom":sQuery(id+"F0.wireOp",EDGE,"E1167")}),-1.0]])]});
            var Q14;
            Q14=makeQuery(id+"F0.imprint","IMPRINT",FACE,{"disambiguationData":[TD([[makeQuery(id+"F0.imprint","IMPRINT",EDGE,{"derivedFrom":sQuery(id+"F0.wireOp",EDGE,"E1139")}),-1.0]])]});
            var Q15;
            Q15=makeQuery(id+"F0.imprint","IMPRINT",FACE,{"disambiguationData":[TD([[makeQuery(id+"F0.imprint","IMPRINT",EDGE,{"derivedFrom":sQuery(id+"F0.wireOp",EDGE,"E1195")}),-1.0]])]});
            var Q16;
            Q16=makeQuery(id+"F0.imprint","IMPRINT",FACE,{"disambiguationData":[TD([[makeQuery(id+"F0.imprint","IMPRINT",EDGE,{"derivedFrom":sQuery(id+"F0.wireOp",EDGE,"E1237")}),-1.0]])]});
            var Q17;
            Q17=makeQuery(id+"F0.imprint","IMPRINT",FACE,{"disambiguationData":[TD([[makeQuery(id+"F0.imprint","IMPRINT",EDGE,{"derivedFrom":sQuery(id+"F0.wireOp",EDGE,"E1287")}),-1.0]])]});
            var Q18;
            Q18=makeQuery(id+"F0.imprint","IMPRINT",FACE,{"disambiguationData":[TD([[makeQuery(id+"F0.imprint","IMPRINT",EDGE,{"derivedFrom":sQuery(id+"F0.wireOp",EDGE,"E1265")}),-1.0]])]});
            var Q19;
            Q19=makeQuery(id+"F0.imprint","IMPRINT",FACE,{"disambiguationData":[TD([[makeQuery(id+"F0.imprint","IMPRINT",EDGE,{"derivedFrom":sQuery(id+"F0.wireOp",EDGE,"E1328")}),-1.0]])]});
            var Q20;
            Q20=makeQuery(id+"F0.imprint","IMPRINT",FACE,{"disambiguationData":[TD([[makeQuery(id+"F0.imprint","IMPRINT",EDGE,{"derivedFrom":sQuery(id+"F0.wireOp",EDGE,"E1368")}),-1.0]])]});
            var Q21;
            Q21=makeQuery(id+"F0.imprint","IMPRINT",FACE,{"disambiguationData":[TD([[makeQuery(id+"F0.imprint","IMPRINT",EDGE,{"derivedFrom":sQuery(id+"F0.wireOp",EDGE,"E1392")}),-1.0]])]});
            var Q22;
            Q22=makeQuery(id+"F0.imprint","IMPRINT",FACE,{"disambiguationData":[TD([[makeQuery(id+"F0.imprint","IMPRINT",EDGE,{"derivedFrom":sQuery(id+"F0.wireOp",EDGE,"E1414")}),-1.0]])]});
            var Q23;
            Q23=makeQuery(id+"F0.imprint","IMPRINT",FACE,{"disambiguationData":[TD([[makeQuery(id+"F0.imprint","IMPRINT",EDGE,{"derivedFrom":sQuery(id+"F0.wireOp",EDGE,"E1432")}),-1.0]])]});
            extrude(context, id + "F4", {"entities" : qUnion([Q0, Q1, Q2, Q3, Q4, Q5, Q6, Q7, Q8, Q9, Q10, Q11, Q12, Q13, Q14, Q15, Q16, Q17, Q18, Q19, Q20, Q21, Q22, Q23]), "operationType" : NewBodyOperationType.ADD, "depth" : 0.5 * mm});
        }
        {
            var Q0;
            Q0=makeQuery(id+"F0.imprint","IMPRINT",FACE,{"disambiguationData":[TD([[makeQuery(id+"F0.imprint","IMPRINT",EDGE,{"derivedFrom":sQuery(id+"F0.wireOp",EDGE,"E96")}),1.0]])]});
            var sketch = newSketch(context, id + "F5", { "sketchPlane" : qUnion([Q0])});
            skText(sketch, "E1571", { "text": "EDZHAR", "fontName": "DroidSansMono.ttf"});
            const initialGuessF5  = {"E1571": [-0.00164, 0.00361, 0.93574, -0.35268, 0.00108]};
            skSetInitialGuess(sketch, initialGuessF5);
            skSolve(sketch);
        }
        {
            var Q0;
            Q0 = qSketchRegion(id + "F5", true);
            extrude(context, id + "F6", {"entities" : qUnion([Q0]), "operationType" : NewBodyOperationType.REMOVE, "oppositeDirection" : true, "depth" : 0.4 * mm});
        }
    });
